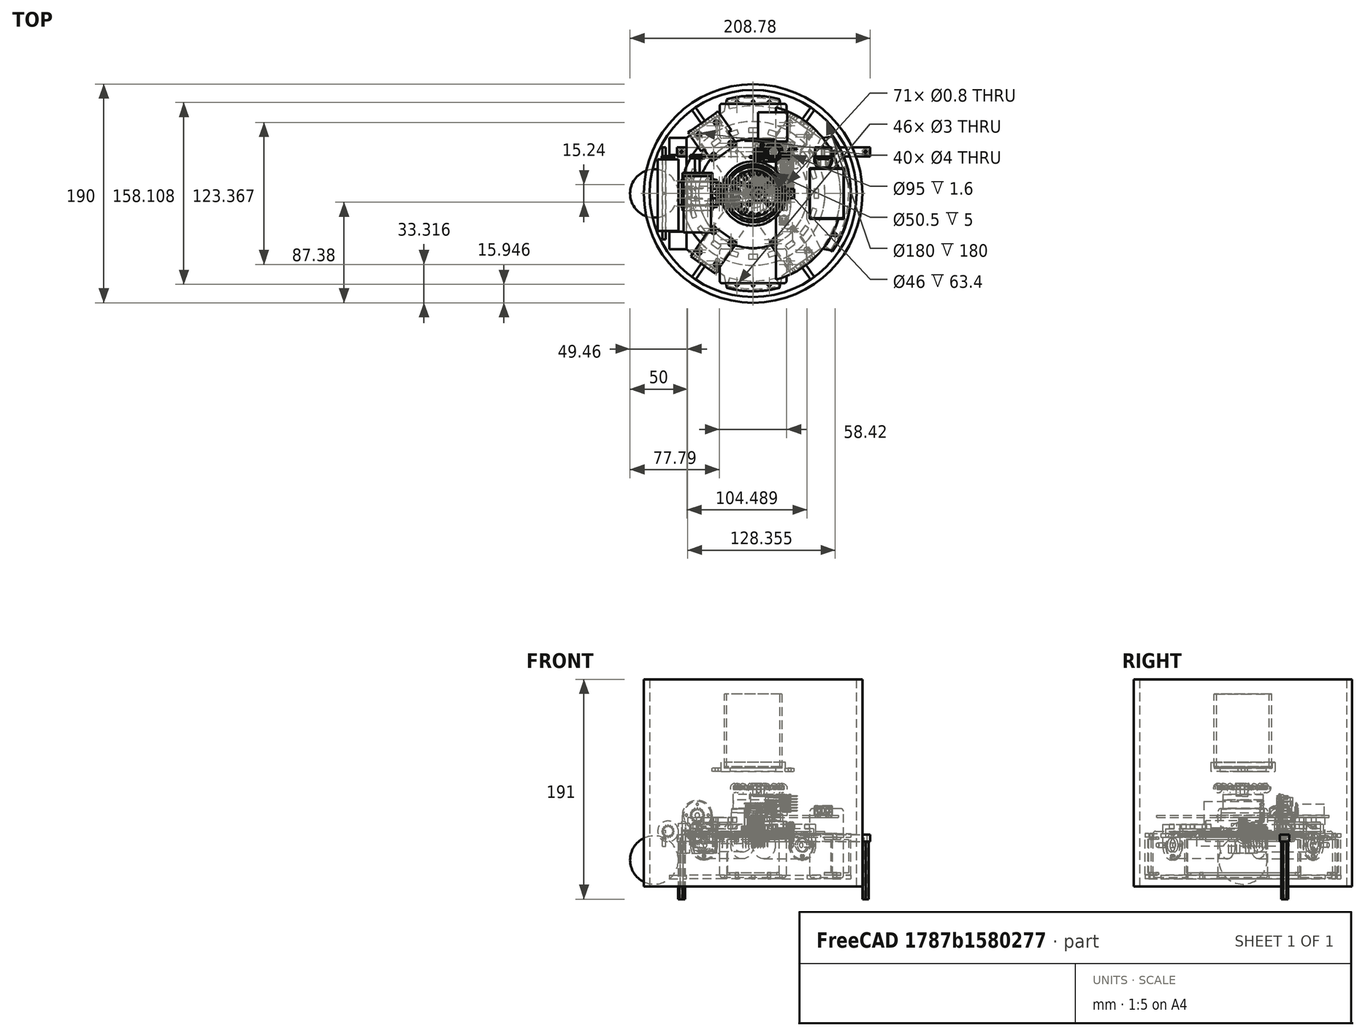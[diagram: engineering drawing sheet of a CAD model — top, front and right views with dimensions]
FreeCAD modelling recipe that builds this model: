
FCSTD DOCUMENT  (FreeCAD 0.21R33668 +7 (Git))
Label: SN8 model 3
License: All rights reserved
LicenseURL: https://en.wikipedia.org/wiki/All_rights_reserved
objects: Part::Feature×480, Sketcher::SketchObject×82, App::Part×79, PartDesign::Pad×55, PartDesign::Pocket×47, PartDesign::Body×37, PartDesign::SubShapeBinder×25, PartDesign::PolarPattern×12, PartDesign::Revolution×4, PartDesign::Fillet×3, Part::Part2DObjectPython×2, Part::Sphere×1
note: 857 computed .brp shape members not serialized (recipe doc carries the construction recipe); baked Part::Feature solids carry a one-line shape summary decoded from their .brp

FEATURE [Part::Feature] Part__Feature  label="base_® 㬮«砭¨"
  shape: bbox 35.56 x 44.45 x 1.6 mm, 428 faces (baked)
FEATURE [Part::Feature] Part__Feature022  label="960240-6202-AR Body8"
  Placement = pos=(10.16,-1.27,8.5) rot=(0,0,1;0rad)
  shape: bbox 20.32 x 2.54 x 8.5 mm, 114 faces (baked)
FEATURE [Part::Feature] Part__Feature023  label="960240-6202-AR Pin Long"
  Placement = pos=(8.89,0.039993,-0.757199) rot=(1,0,0;1.5708rad)
  shape: bbox 2 x 0.4 x 16.99 mm, 25 faces (baked)
FEATURE [Part::Feature] Part__Feature024  label="960240-6202-AR Pin Long001"
  Placement = pos=(6.35,0.039993,-0.757199) rot=(1,0,0;1.5708rad)
  shape: bbox 2 x 0.4 x 16.99 mm, 25 faces (baked)
FEATURE [Part::Feature] Part__Feature025  label="960240-6202-AR Pin Long002"
  Placement = pos=(3.81,0.039993,-0.757199) rot=(1,0,0;1.5708rad)
  shape: bbox 2 x 0.4 x 16.99 mm, 25 faces (baked)
FEATURE [Part::Feature] Part__Feature026  label="960240-6202-AR Pin Long003"
  Placement = pos=(1.27,0.039993,-0.757199) rot=(1,0,0;1.5708rad)
  shape: bbox 2 x 0.4 x 16.99 mm, 25 faces (baked)
FEATURE [Part::Feature] Part__Feature027  label="960240-6202-AR Pin Long004"
  Placement = pos=(-1.27,0.039993,-0.757199) rot=(1,0,0;1.5708rad)
  shape: bbox 2 x 0.4 x 16.99 mm, 25 faces (baked)
FEATURE [Part::Feature] Part__Feature028  label="960240-6202-AR Pin Long005"
  Placement = pos=(-3.81,0.039993,-0.757199) rot=(1,0,0;1.5708rad)
  shape: bbox 2 x 0.4 x 16.99 mm, 25 faces (baked)
FEATURE [Part::Feature] Part__Feature029  label="960240-6202-AR Pin Long006"
  Placement = pos=(-6.35,0.039993,-0.757199) rot=(1,0,0;1.5708rad)
  shape: bbox 2 x 0.4 x 16.99 mm, 25 faces (baked)
FEATURE [Part::Feature] Part__Feature030  label="960240-6202-AR Pin Long007"
  Placement = pos=(-8.89,0.039993,-0.757199) rot=(1,0,0;1.5708rad)
  shape: bbox 2 x 0.4 x 16.99 mm, 25 faces (baked)
FEATURE [App::Part] _60240_6202_AR_1x8_long  label="Right side I/O pins long"
  Group = -> [Part__Feature022,Part__Feature023,Part__Feature024,Part__Feature025,Part__Feature026,Part__Feature027,Part__Feature028,Part__Feature029,Part__Feature030]
  Origin = -> Origin
  Placement = pos=(33.909,10.414,1.6) rot=(0,0,1;1.5708rad)
FEATURE [Part::Feature] Part__Feature031  label="960240-6202-AR Body009"
  Placement = pos=(10.16,-1.27,8.5) rot=(0,0,1;0rad)
  shape: bbox 20.32 x 2.54 x 8.5 mm, 114 faces (baked)
FEATURE [Part::Feature] Part__Feature032  label="960240-6202-AR Pin Long008"
  Placement = pos=(8.89,0.039993,-0.757199) rot=(1,0,0;1.5708rad)
  shape: bbox 2 x 0.4 x 16.99 mm, 25 faces (baked)
FEATURE [Part::Feature] Part__Feature033  label="960240-6202-AR Pin Long009"
  Placement = pos=(6.35,0.039993,-0.757199) rot=(1,0,0;1.5708rad)
  shape: bbox 2 x 0.4 x 16.99 mm, 25 faces (baked)
FEATURE [Part::Feature] Part__Feature034  label="960240-6202-AR Pin Long010"
  Placement = pos=(3.81,0.039993,-0.757199) rot=(1,0,0;1.5708rad)
  shape: bbox 2 x 0.4 x 16.99 mm, 25 faces (baked)
FEATURE [Part::Feature] Part__Feature035  label="960240-6202-AR Pin Long011"
  Placement = pos=(1.27,0.039993,-0.757199) rot=(1,0,0;1.5708rad)
  shape: bbox 2 x 0.4 x 16.99 mm, 25 faces (baked)
FEATURE [Part::Feature] Part__Feature036  label="960240-6202-AR Pin Long012"
  Placement = pos=(-1.27,0.039993,-0.757199) rot=(1,0,0;1.5708rad)
  shape: bbox 2 x 0.4 x 16.99 mm, 25 faces (baked)
FEATURE [Part::Feature] Part__Feature037  label="960240-6202-AR Pin Long013"
  Placement = pos=(-3.81,0.039993,-0.757199) rot=(1,0,0;1.5708rad)
  shape: bbox 2 x 0.4 x 16.99 mm, 25 faces (baked)
FEATURE [Part::Feature] Part__Feature038  label="960240-6202-AR Pin Long014"
  Placement = pos=(-6.35,0.039993,-0.757199) rot=(1,0,0;1.5708rad)
  shape: bbox 2 x 0.4 x 16.99 mm, 25 faces (baked)
FEATURE [Part::Feature] Part__Feature039  label="960240-6202-AR Pin Long015"
  Placement = pos=(-8.89,0.039993,-0.757199) rot=(1,0,0;1.5708rad)
  shape: bbox 2 x 0.4 x 16.99 mm, 25 faces (baked)
FEATURE [App::Part] _60240_6202_AR_1x8_long001  label="Left side I/O pins"
  Group = -> [Part__Feature031,Part__Feature032,Part__Feature033,Part__Feature034,Part__Feature035,Part__Feature036,Part__Feature037,Part__Feature038,Part__Feature039]
  Origin = -> Origin001
  Placement = pos=(1.651,10.414,1.6) rot=(0,0,1;1.5708rad)
FEATURE [Part::Feature] Part__Feature040  label="960240-6202-AR Body6"
  Placement = pos=(7.62,-1.27,8.5) rot=(0,0,1;0rad)
  shape: bbox 15.24 x 2.54 x 8.5 mm, 88 faces (baked)
FEATURE [Part::Feature] Part__Feature041  label="960240-6202-AR Pin Long016"
  Placement = pos=(6.35,0.039993,-0.757199) rot=(1,0,0;1.5708rad)
  shape: bbox 2 x 0.4 x 16.99 mm, 25 faces (baked)
FEATURE [Part::Feature] Part__Feature042  label="960240-6202-AR Pin Long017"
  Placement = pos=(3.81,0.039993,-0.757199) rot=(1,0,0;1.5708rad)
  shape: bbox 2 x 0.4 x 16.99 mm, 25 faces (baked)
FEATURE [Part::Feature] Part__Feature043  label="960240-6202-AR Pin Long018"
  Placement = pos=(1.27,0.039993,-0.757199) rot=(1,0,0;1.5708rad)
  shape: bbox 2 x 0.4 x 16.99 mm, 25 faces (baked)
FEATURE [Part::Feature] Part__Feature044  label="960240-6202-AR Pin Long019"
  Placement = pos=(-1.27,0.039993,-0.757199) rot=(1,0,0;1.5708rad)
  shape: bbox 2 x 0.4 x 16.99 mm, 25 faces (baked)
FEATURE [Part::Feature] Part__Feature045  label="960240-6202-AR Pin Long020"
  Placement = pos=(-3.81,0.039993,-0.757199) rot=(1,0,0;1.5708rad)
  shape: bbox 2 x 0.4 x 16.99 mm, 25 faces (baked)
FEATURE [Part::Feature] Part__Feature046  label="960240-6202-AR Pin Long021"
  Placement = pos=(-6.35,0.039993,-0.757199) rot=(1,0,0;1.5708rad)
  shape: bbox 2 x 0.4 x 16.99 mm, 25 faces (baked)
FEATURE [App::Part] _60240_6202_AR_1x6_long  label="Right side I/O pins short"
  Group = -> [Part__Feature040,Part__Feature041,Part__Feature042,Part__Feature043,Part__Feature044,Part__Feature045,Part__Feature046]
  Origin = -> Origin002
  Placement = pos=(30.099,12.954,1.6) rot=(0,0,-1;1.5708rad)
FEATURE [Part::Feature] Part__Feature050  label="LED SMD RGB"
  Placement = pos=(3.559,28.499,1.75) rot=(0.57735,0.57735,0.57735;2.0944rad)
  shape: bbox 2.8 x 3.5 x 1.9 mm, 85 faces (baked)
FEATURE [Part::Feature] Part__Feature051  label="LED 1206 IR"
  Placement = pos=(28.321,41.91,1.6) rot=(0,0.707107,0.707107;3.14159rad)
  shape: bbox 1.6 x 3.2 x 1.095 mm, 42 faces, 2 solids (baked)
FEATURE [Part::Feature] Part__Feature052  label="LED 1206 IR001"
  Placement = pos=(7.239,41.91,1.6) rot=(1,0,0;1.5708rad)
  shape: bbox 1.6 x 3.2 x 1.095 mm, 42 faces, 2 solids (baked)
FEATURE [Part::Feature] Part__Feature053  label="SOT 23"
  Placement = pos=(3.429,25.019,2.15) rot=(0,0.707107,0.707107;3.14159rad)
  shape: bbox 3 x 2.5 x 1.1 mm, 49 faces (baked)
FEATURE [Part::Feature] Part__Feature054  label="SOT 024"
  Placement = pos=(20.193,4.064,2.15) rot=(0,0.707107,0.707107;3.14159rad)
  shape: bbox 3 x 2.5 x 1.1 mm, 49 faces (baked)
FEATURE [Part::Feature] Part__Feature062  label="EXBV8V"
  Placement = pos=(6.4748,30.1505,1.59) rot=(0,0,1;1.5708rad)
  shape: bbox 1.6 x 3.2 x 0.52 mm, 170 faces (baked)
FEATURE [Part::Feature] Part__Feature063  label="EXBV8V001"
  Placement = pos=(28.448,31.496,1.6) rot=(0,0,1;0rad)
  shape: bbox 3.2 x 1.6 x 0.52 mm, 170 faces (baked)
FEATURE [Part::Feature] Part__Feature064  label="EXBV8V002"
  Placement = pos=(28.448,25.019,1.6) rot=(0,0,1;0rad)
  shape: bbox 3.2 x 1.6 x 0.52 mm, 170 faces (baked)
FEATURE [Part::Feature] Part__Feature065  label="User Library-LQFP100-3_case"
  Placement = pos=(0,0.92,0) rot=(0,0,1;0rad)
  shape: bbox 13.97 x 1.4 x 13.97 mm, 31 faces (baked)
FEATURE [App::Part] User_Library_LQFP100_3  label="Microprocessor"
  Group = -> [Part__Feature065]
  Origin = -> Origin003
  Placement = pos=(17.78,16.383,1.6) rot=(1,0,0;1.5708rad)
FEATURE [Part::Feature] Part__Feature167  label="SOT 23-5"
  Placement = pos=(26.67,36.83,2.15) rot=(0.57735,-0.57735,-0.57735;2.0944rad)
  shape: bbox 2.5 x 3 x 1.1 mm, 75 faces (baked)
FEATURE [Part::Feature] Part__Feature168  label="SOT 23-006"
  Placement = pos=(15.113,4.572,2.15) rot=(0,0.707107,0.707107;3.14159rad)
  shape: bbox 3 x 2.5 x 1.1 mm, 75 faces (baked)
FEATURE [Part::Feature] Part__Feature169  label="UJ2-MIBH2-4-SMT_01_Defaut"
  shape: bbox 5.297 x 7.502 x 3.412 mm, 268 faces (baked)
FEATURE [App::Part] UJ2_MIBH2_4_SMT_Defaut  label="USB port"
  Group = -> [Part__Feature169]
  Origin = -> Origin004
  Placement = pos=(30.42,-1.4925,3.54996) rot=(0,0,1;1.5708rad)
FEATURE [Part::Feature] Part__Feature171  label="1040310811_USD1040310811_® 㬮«砭¨쥀«?"
  Placement = pos=(27.5125,71.8621,-0.6) rot=(0.707107,-0.707107,0;3.14159rad)
  shape: bbox 11.43 x 11.98 x 1.48 mm, 410 faces (baked)
FEATURE [Part::Feature] Part__Feature172  label="DF12-36DS-0.5V_® 㬮«砭¨"
  Placement = pos=(15.63,42.14,1.6) rot=(0,0,1;3.14159rad)
  shape: bbox 12.11 x 4.614 x 3.314 mm, 836 faces (baked)
FEATURE [Part::Feature] Part__Feature173  label="S2B-PH-K-S(LF)(SN)_® 㬮«砭¨"
  Placement = pos=(7.112,7.7,1.6) rot=(1,0,0;1.5708rad)
  shape: bbox 5.9 x 7.6 x 8.183 mm, 100 faces, 3 solids (baked)
FEATURE [Part::Feature] Part__Feature174  label="Crystal-SM2520-4"
  Placement = pos=(5.969,16.764,1.6) rot=(0,0,1;0rad)
  shape: bbox 2.5 x 2 x 0.825 mm, 72 faces, 5 solids (baked)
FEATURE [Part::Feature] Part__Feature175  label="Standoff metal 5x2.5mm_® 㬮«砭¨"
  Placement = pos=(33.02,36.2,1.6) rot=(1,0,0;1.5708rad)
  shape: bbox 5 x 5 x 5 mm, 6 faces (baked)
FEATURE [Part::Feature] Part__Feature176  label="Standoff metal 5x2.5mm_® 㬮«砭¨001"
  Placement = pos=(2.54,36.2,6.6) rot=(-1,0,0;1.5708rad)
  shape: bbox 5 x 5 x 5 mm, 6 faces (baked)
FEATURE [App::Part] openmv4_h7_base________________  label="PCB "
  Group = -> [Part__Feature,_60240_6202_AR_1x8_long,_60240_6202_AR_1x8_long001,_60240_6202_AR_1x6_long,Part__Feature050,Part__Feature051,Part__Feature052,Part__Feature053,Part__Feature054,Part__Feature062,Part__Feature063,Part__Feature064,User_Library_LQFP100_3,Part__Feature167,Part__Feature168,UJ2_MIBH2_4_SMT_Defaut,Part__Feature171,Part__Feature172,Part__Feature173,Part__Feature174,Part__Feature175,+1 more]
  Origin = -> Origin005
FEATURE [Part::Feature] Part__Feature177  label="ov7725_® 㬮«砭¨"
  shape: bbox 35.56 x 16.51 x 1.6 mm, 134 faces (baked)
FEATURE [Part::Feature] Part__Feature178  label="mount_lens"
  Placement = pos=(8.255,8.255,1.6) rot=(0,0,1;0rad)
  shape: bbox 23.8 x 17 x 14.3 mm, 58 faces (baked)
FEATURE [Part::Feature] Part__Feature179  label="DF1236"
  Placement = pos=(37.855,-65.4,0) rot=(0,1,0;3.14159rad)
  shape: bbox 12.1 x 4.6 x 4.9 mm, 1562 faces (baked)
FEATURE [App::Part] openmv4_ov7725________________  label="Lens mount"
  Group = -> [Part__Feature177,Part__Feature178,Part__Feature179]
  Origin = -> Origin006
  Placement = pos=(9.525,27.945,6.6) rot=(0,0,1;0rad)
FEATURE [Part::Feature] Part__Feature181  label="pan head cross recess screw_iso_ISO 7045 - M2.5 x 5 - Z - 5N"
  Placement = pos=(33.02,36.2,12.1) rot=(0,1,0;1.5708rad)
  shape: bbox 5.412 x 5.412 x 7.1 mm, 43 faces (baked)
FEATURE [Part::Feature] Part__Feature182  label="pan head cross recess screw_iso_ISO 7045 - M2.5 x 5 - Z - 5N001"
  Placement = pos=(2.54,36.2,12.1) rot=(0,1,0;1.5708rad)
  shape: bbox 5.412 x 5.412 x 7.1 mm, 43 faces (baked)
FEATURE [Part::Feature] Part__Feature183  label="microsd card"
  Placement = pos=(48.2048,51.1529,-0.388376) rot=(-0.707107,0.707107,0;3.14159rad)
  shape: bbox 15 x 11.07 x 1 mm, 19 faces (baked)
FEATURE [Part::Feature] Part__Feature184  label="LENS_Standard_® 㬮«砭¨"
  Placement = pos=(17.78,36.2,16.7534) rot=(1,0,0;1.5708rad)
  shape: bbox 14 x 14 x 16.7 mm, 16 faces (baked)
FEATURE [Part::Feature] Part__Feature186  label="Micro USB connector"
  Placement = pos=(26.6352,-11.6075,-1.10004) rot=(0.57735,0.57735,0.57735;4.18879rad)
  shape: bbox 12.26 x 29.6 x 16 mm, 326 faces (baked)
FEATURE [Part::Feature] Part__Feature187  label="pan head cross recess screw_iso_ISO 7045 - M1 x 4 - Z - 4S"
  Placement = pos=(17.78,47.3586,20.3) rot=(0.004126,-0.004126,-0.999983;1.57081rad)
  shape: bbox 2.165 x 5 x 2.165 mm, 92 faces (baked)
FEATURE [App::Part] openmv4_h7  label="OpenMV H7"
  Group = -> [openmv4_h7_base________________,openmv4_ov7725________________,Part__Feature181,Part__Feature182,Part__Feature183,Part__Feature184,Part__Feature186,Part__Feature187]
  Origin = -> Origin007
  Placement = pos=(36.22,-17.79,57) rot=(0,0,1;1.5708rad)
FEATURE [Sketcher::SketchObject] Sketch
  FullyConstrained = true
  MapMode = 5
  Support = -> [XY_Plane008]
  sketch-geometry (1):
    g0: Circle CenterX=0 CenterY=0 CenterZ=0 NormalX=0 NormalY=0 NormalZ=1 AngleXU=0 Radius=85
  constraints (2):
    c: Coincident(g0,g-1)
    c: Diameter(g0) = 170
FEATURE [Sketcher::SketchObject] Sketch005
  FullyConstrained = true
  MapMode = 5
  Placement = pos=(0,0,0) rot=(1,0,0;1.5708rad)
  Support = -> [XZ_Plane009]
  sketch-geometry (6):
    g0: ArcOfHyperbola CenterX=0 CenterY=94.5 CenterZ=0 NormalX=0 NormalY=0 NormalZ=1 MajorRadius=17.5 MinorRadius=15.6742 AngleXU=1.5708 StartAngle=0 EndAngle=1.02375
    g1: LineSegment StartX=5e-16 StartY=112 StartZ=0 EndX=-5e-16 EndY=77 EndZ=0
    g2: LineSegment StartX=-15.6742 StartY=112 StartZ=0 EndX=15.6742 EndY=112 EndZ=0
    g3: GeomPoint X=2.6e-15 Y=117.993 Z=0
    g4: LineSegment StartX=-19 StartY=122 StartZ=0 EndX=0 EndY=122 EndZ=0
    g5: LineSegment StartX=0 StartY=112 StartZ=0 EndX=0 EndY=122 EndZ=0
  constraints (15):
    c: InternalAlignment(g1,g0)
    c: InternalAlignment(g2,g0)
    c: InternalAlignment(g3,g0)
    c: Horizontal(g2)
    c: PointOnObject(g0,g-2)
    c: PointOnObject(g0,g-2)
    c: DistanceY(g0,g0) = 10
    c: DistanceX(g0,g0) = 19
    c: DistanceY(g1,g0) = 35
    c: Coincident(g4,g0)
    c: Coincident(g5,g0)
    c: Coincident(g5,g4)
    c: Vertical(g5)
    c: Horizontal(g4)
    c: DistanceY(g-1,g0) = 112
FEATURE [PartDesign::Pad] Pad  label="Structural layer"
  Direction = (0,0,1)
  Length = 3
  Length2 = 10
  Profile = -> Sketch
  ReferenceAxis = -> Sketch [N_Axis]
  Type = 0
FEATURE [Sketcher::SketchObject] Sketch001
  ExternalGeometry = -> [Pad]
  FullyConstrained = false
  MapMode = 5
  Placement = pos=(0,0,3) rot=(0,0,1;0rad)
  Support = -> [Pad]
  sketch-geometry (7):
    g0: LineSegment StartX=-10.6686 StartY=100.741 StartZ=0 EndX=44.4806 EndY=91.0164 EndZ=0
    g1: LineSegment StartX=44.4806 StartY=91.0164 StartZ=0 EndX=41.5109 EndY=74.1744 EndZ=0
    g2: LineSegment StartX=32.942 StartY=68.1744 StartZ=0 EndX=-7.63834 EndY=75.3298 EndZ=0
    g3: LineSegment StartX=-13.6383 StartY=83.8987 StartZ=0 EndX=-10.6686 EndY=100.741 EndZ=0
    g4: LineSegment StartX=32.942 StartY=68.1744 StartZ=0 EndX=41.5109 EndY=74.1744 EndZ=0
    g5: LineSegment StartX=-13.6383 StartY=83.8987 StartZ=0 EndX=-7.63834 EndY=75.3298 EndZ=0
    g6: LineSegment StartX=-98.5042 StartY=90.5189 StartZ=0 EndX=89.0462 EndY=57.4487 EndZ=0
  constraints (18):
    c: Coincident(g0,g1)
    c: Coincident(g3,g0)
    c: Coincident(g4,g2)
    c: Coincident(g4,g1)
    c: Coincident(g5,g3)
    c: Coincident(g5,g2)
    c: Angle(g4,g2) = 2.35619
    c: Angle(g2,g5) = 2.35619
    c: DistanceX(g3,g2) = 6
    c: Angle(g6,g-1) = 0.174533
    c: Parallel(g2,g6)
    c: Parallel(g0,g2)
    c: Perpendicular(g6,g1)
    c: Equal(g1,g3)
    c: Parallel(g1,g3)
    c: PointOnObject(g3,g-3)
    c: PointOnObject(g1,g-3)
    c: Distance(g0) = 56
FEATURE [PartDesign::Pocket] Pocket
  BaseFeature = -> Pad
  Direction = (0,0,-1)
  Length = 5
  Length2 = 5
  Profile = -> Sketch001
  ReferenceAxis = -> Sketch001 [N_Axis]
  Type = 1
FEATURE [PartDesign::PolarPattern] PolarPattern
  Angle = 110
  Axis = -> Sketch001 [N_Axis]
  BaseFeature = -> Pocket
  Occurrences = 2
  Originals = -> [Pocket]
FEATURE [PartDesign::Revolution] Revolution
  Angle = 360
  Axis = (0,-2e-16,1)
  Base = (0,0,0)
  Placement = pos=(0,0,0) rot=(1,0,0;1.5708rad)
  Profile = -> Sketch005
  ReferenceAxis = -> Sketch005 [V_Axis]
FEATURE [Sketcher::SketchObject] Sketch015
  FullyConstrained = true
  MapMode = 5
  Placement = pos=(0,0,3) rot=(0,0,1;0rad)
  Support = -> [PolarPattern]
  sketch-geometry (4):
    g0: LineSegment StartX=-111 StartY=31 StartZ=0 EndX=-31 EndY=111 EndZ=0
    g1: LineSegment StartX=-31 StartY=111 StartZ=0 EndX=-1 EndY=81 EndZ=0
    g2: LineSegment StartX=-1 StartY=81 StartZ=0 EndX=-81 EndY=1 EndZ=0
    g3: LineSegment StartX=-81 StartY=1 StartZ=0 EndX=-111 EndY=31 EndZ=0
  constraints (12):
    c: Coincident(g0,g1)
    c: Coincident(g1,g2)
    c: Coincident(g2,g3)
    c: Coincident(g3,g0)
    c: Equal(g3,g1)
    c: Equal(g0,g2)
    c: Angle(g3,g0) = 1.5708
    c: DistanceX(g2,g-1) = 81
    c: DistanceY(g-1,g1) = 81
    c: DistanceX(g0,g1) = 30
    c: DistanceX(g2,g1) = 80
    c: Angle(g-1,g2) = 0.785398
FEATURE [PartDesign::Pocket] Pocket004
  BaseFeature = -> PolarPattern
  Direction = (0,0,-1)
  Length = 5
  Length2 = 5
  Profile = -> Sketch015
  ReferenceAxis = -> Sketch015 [N_Axis]
  Type = 1
FEATURE [Sketcher::SketchObject] Sketch016
  FullyConstrained = true
  MapMode = 5
  Placement = pos=(0,0,0) rot=(1,0,0;1.5708rad)
  Support = -> [XZ_Plane016]
  sketch-geometry (8):
    g0: LineSegment StartX=-88 StartY=-1 StartZ=0 EndX=-79 EndY=-1 EndZ=0
    g1: LineSegment StartX=-79 StartY=-34 StartZ=0 EndX=-88 EndY=-34 EndZ=0
    g2: LineSegment StartX=-88 StartY=-34 StartZ=0 EndX=-88 EndY=-1 EndZ=0
    g3: LineSegment StartX=-79 StartY=-1 StartZ=0 EndX=-79 EndY=-3 EndZ=0
    g4: LineSegment StartX=-79 StartY=-3 StartZ=0 EndX=-86 EndY=-3 EndZ=0
    g5: LineSegment StartX=-86 StartY=-3 StartZ=0 EndX=-86 EndY=-32 EndZ=0
    g6: LineSegment StartX=-86 StartY=-32 StartZ=0 EndX=-79 EndY=-32 EndZ=0
    g7: LineSegment StartX=-79 StartY=-32 StartZ=0 EndX=-79 EndY=-34 EndZ=0
  constraints (24):
    c: Coincident(g1,g2)
    c: Coincident(g2,g0)
    c: Horizontal(g0)
    c: Horizontal(g1)
    c: Vertical(g2)
    c: DistanceY(g1,g0) = 33
    c: DistanceX(g1,g1) = 9
    c: DistanceX(g0,g-1) = 88
    c: DistanceY(g1,g-1) = 34
    c: Equal(g1,g0)
    c: Coincident(g3,g0)
    c: Vertical(g3)
    c: Coincident(g4,g3)
    c: Horizontal(g4)
    c: Coincident(g5,g4)
    c: Vertical(g5)
    c: Coincident(g6,g5)
    c: Horizontal(g6)
    c: Coincident(g7,g6)
    c: Coincident(g7,g1)
    c: Vertical(g7)
    c: Equal(g3,g7)
    c: DistanceY(g3,g3) = 2
    c: DistanceX(g0,g4) = 2
FEATURE [PartDesign::Revolution] Revolution001
  Angle = 30
  Axis = (1e-16,1e-16,1)
  Base = (0,0,0)
  Midplane = true
  Placement = pos=(0,0,0) rot=(1,0,0;1.5708rad)
  Profile = -> Sketch016
  ReferenceAxis = -> Z_Axis016
  Reversed = true
FEATURE [Part::Feature] Part__Feature268  label="OmniBase_Predeterminado004"
  Placement = pos=(4.80373,-0.638646,40.5) rot=(0,0,1;0rad)
  shape: bbox 44 x 43.9 x 9 mm, 104 faces (baked)
FEATURE [Part::Feature] Part__Feature269  label="Roller_Predeterminado072"
  Placement = pos=(4.80373,20.3614,41.6192) rot=(0,0,1;0rad)
  shape: bbox 2.6 x 8.659 x 8.659 mm, 10 faces (baked)
FEATURE [Part::Feature] Part__Feature270  label="Roller_Predeterminado073"
  Placement = pos=(-2.3787,19.0949,41.6192) rot=(0,0,1;0.349066rad)
  shape: bbox 4.664 x 8.342 x 8.659 mm, 10 faces (baked)
FEATURE [Part::Feature] Part__Feature271  label="Roller_Predeterminado074"
  Placement = pos=(-8.69481,15.4483,41.6192) rot=(0,0,1;0.698132rad)
  shape: bbox 6.71 x 7.451 x 8.659 mm, 10 faces (baked)
FEATURE [Part::Feature] Part__Feature272  label="Roller_Predeterminado075"
  Placement = pos=(-13.3828,9.86135,41.6192) rot=(0,0,1;1.0472rad)
  shape: bbox 7.965 x 5.765 x 8.659 mm, 10 faces (baked)
FEATURE [Part::Feature] Part__Feature273  label="Roller_Predeterminado076"
  Placement = pos=(-15.8772,3.00797,41.6192) rot=(0,0,1;1.39626rad)
  shape: bbox 8.632 x 3.688 x 8.659 mm, 10 faces (baked)
FEATURE [Part::Feature] Part__Feature274  label="Roller_Predeterminado077"
  Placement = pos=(-15.8772,-4.28526,41.6192) rot=(0,0,1;1.74533rad)
  shape: bbox 8.632 x 3.688 x 8.659 mm, 10 faces (baked)
FEATURE [Part::Feature] Part__Feature275  label="Roller_Predeterminado078"
  Placement = pos=(-13.3828,-11.1386,41.6192) rot=(0,0,1;2.0944rad)
  shape: bbox 7.965 x 5.765 x 8.659 mm, 10 faces (baked)
FEATURE [Part::Feature] Part__Feature276  label="Roller_Predeterminado079"
  Placement = pos=(-8.69481,-16.7256,41.6192) rot=(0,0,1;2.44346rad)
  shape: bbox 6.71 x 7.451 x 8.659 mm, 10 faces (baked)
FEATURE [Part::Feature] Part__Feature277  label="Roller_Predeterminado080"
  Placement = pos=(-2.3787,-20.3722,41.6192) rot=(0,0,1;2.79253rad)
  shape: bbox 4.664 x 8.342 x 8.659 mm, 10 faces (baked)
FEATURE [Part::Feature] Part__Feature278  label="Roller_Predeterminado081"
  Placement = pos=(4.80373,-21.6386,41.6192) rot=(0,0,1;3.14159rad)
  shape: bbox 2.6 x 8.659 x 8.659 mm, 10 faces (baked)
FEATURE [Part::Feature] Part__Feature279  label="Roller_Predeterminado082"
  Placement = pos=(11.9862,-20.3722,41.6192) rot=(0,0,1;3.49066rad)
  shape: bbox 4.664 x 8.342 x 8.659 mm, 10 faces (baked)
FEATURE [Part::Feature] Part__Feature280  label="Roller_Predeterminado083"
  Placement = pos=(18.3023,-16.7256,41.6192) rot=(0,0,1;3.83972rad)
  shape: bbox 6.71 x 7.451 x 8.659 mm, 10 faces (baked)
FEATURE [Part::Feature] Part__Feature281  label="Roller_Predeterminado084"
  Placement = pos=(22.9903,-11.1386,41.6192) rot=(0,0,-1;2.0944rad)
  shape: bbox 7.965 x 5.765 x 8.659 mm, 10 faces (baked)
FEATURE [Part::Feature] Part__Feature282  label="Roller_Predeterminado085"
  Placement = pos=(25.4847,-4.28526,41.6192) rot=(0,0,-1;1.74533rad)
  shape: bbox 8.632 x 3.688 x 8.659 mm, 10 faces (baked)
FEATURE [Part::Feature] Part__Feature283  label="Roller_Predeterminado086"
  Placement = pos=(25.4847,3.00797,41.6192) rot=(0,0,-1;1.39626rad)
  shape: bbox 8.632 x 3.688 x 8.659 mm, 10 faces (baked)
FEATURE [Part::Feature] Part__Feature284  label="Roller_Predeterminado087"
  Placement = pos=(22.9903,9.86135,41.6192) rot=(0,0,-1;1.0472rad)
  shape: bbox 7.965 x 5.765 x 8.659 mm, 10 faces (baked)
FEATURE [Part::Feature] Part__Feature285  label="Roller_Predeterminado088"
  Placement = pos=(18.3023,15.4483,41.6192) rot=(0,0,-1;0.698132rad)
  shape: bbox 6.71 x 7.451 x 8.659 mm, 10 faces (baked)
FEATURE [Part::Feature] Part__Feature286  label="Roller_Predeterminado089"
  Placement = pos=(11.9862,19.0949,41.6192) rot=(0,0,-1;0.349066rad)
  shape: bbox 4.664 x 8.342 x 8.659 mm, 10 faces (baked)
FEATURE [Part::Feature] Part__Feature287  label="Nut_Predeterminado004"
  Placement = pos=(4.80373,-0.638646,43.5) rot=(0,0,1;1.0472rad)
  shape: bbox 13.86 x 12.93 x 2 mm, 24 faces (baked)
FEATURE [App::Part] OmniWheel054  label="OmniWheel 1"
  Group = -> [Part__Feature268,Part__Feature269,Part__Feature270,Part__Feature271,Part__Feature272,Part__Feature273,Part__Feature274,Part__Feature275,Part__Feature276,Part__Feature277,Part__Feature278,Part__Feature279,Part__Feature280,Part__Feature281,Part__Feature282,Part__Feature283,Part__Feature284,Part__Feature285,Part__Feature286,Part__Feature287]
  Origin = -> Origin019
  Placement = pos=(-23.8855,35.1581,-6.8) rot=(-0.419215,-0.805305,-0.419215;1.78566rad)
FEATURE [Sketcher::SketchObject] Sketch023
  FullyConstrained = true
  MapMode = 5
  Support = -> [XY_Plane024]
  sketch-geometry (9):
    g0: Circle CenterX=0 CenterY=0 CenterZ=0 NormalX=0 NormalY=0 NormalZ=1 AngleXU=0 Radius=20
    g1: LineSegment StartX=27.7128 StartY=-4 StartZ=0 EndX=35.7128 EndY=-4 EndZ=0
    g2: LineSegment StartX=35.7128 StartY=-4 StartZ=0 EndX=35.7128 EndY=4 EndZ=0
    g3: LineSegment StartX=35.7128 StartY=4 StartZ=0 EndX=27.7128 EndY=4 EndZ=0
    g4: LineSegment StartX=-27.7128 StartY=-4 StartZ=0 EndX=-35.7128 EndY=-4 EndZ=0
    g5: LineSegment StartX=-35.7128 StartY=-4 StartZ=0 EndX=-35.7128 EndY=4 EndZ=0
    g6: LineSegment StartX=-35.7128 StartY=4 StartZ=0 EndX=-27.7128 EndY=4 EndZ=0
    g7: ArcOfCircle CenterX=0 CenterY=0 CenterZ=0 NormalX=0 NormalY=0 NormalZ=1 AngleXU=0 Radius=28 StartAngle=0.143348 EndAngle=2.99825
    g8: ArcOfCircle CenterX=0 CenterY=0 CenterZ=0 NormalX=0 NormalY=0 NormalZ=1 AngleXU=0 Radius=28 StartAngle=3.28494 EndAngle=6.13984
  constraints (25):
    c: Coincident(g0,g-1)
    c: Diameter(g0) = 40
    c: Horizontal(g1)
    c: Coincident(g2,g1)
    c: Coincident(g3,g2)
    c: Horizontal(g3)
    c: Horizontal(g4)
    c: Coincident(g5,g4)
    c: Vertical(g5)
    c: Coincident(g6,g5)
    c: Horizontal(g6)
    c: Coincident(g7,g0)
    c: Coincident(g7,g6)
    c: Coincident(g7,g3)
    c: Coincident(g8,g0)
    c: Coincident(g8,g4)
    c: Coincident(g8,g1)
    c: Diameter(g7) = 56
    c: Diameter(g8) = 56
    c: Symmetric(g1,g2,g-1)
    c: Equal(g5,g2)
    c: Equal(g6,g3)
    c: Equal(g4,g1)
    c: DistanceY(g2,g2) = 8
    c: DistanceX(g6,g6) = 8
FEATURE [PartDesign::Pad] Pad007
  Direction = (0,0,1)
  Length = 3
  Length2 = 10
  Profile = -> Sketch023
  ReferenceAxis = -> Sketch023 [N_Axis]
  Type = 0
FEATURE [Sketcher::SketchObject] Sketch025
  FullyConstrained = true
  MapMode = 5
  Support = -> [XY_Plane026]
  sketch-geometry (2):
    g0: Circle CenterX=0 CenterY=0 CenterZ=0 NormalX=0 NormalY=0 NormalZ=1 AngleXU=0 Radius=90
    g1: Circle CenterX=0 CenterY=0 CenterZ=0 NormalX=0 NormalY=0 NormalZ=1 AngleXU=0 Radius=95
  constraints (4):
    c: Diameter(g0) = 180
    c: Coincident(g1,g-1)
    c: Diameter(g1) = 190
    c: Coincident(g0,g-1)
FEATURE [PartDesign::Pad] Pad008
  Direction = (0,0,1)
  Length = 180
  Length2 = 10
  Profile = -> Sketch025
  ReferenceAxis = -> Sketch025 [N_Axis]
  Type = 0
FEATURE [PartDesign::Body] Body008  label="Cylinder"
  Group = -> [Sketch025,Pad008]
  Origin = -> Origin026
  Placement = pos=(0,0,-44) rot=(0,0,1;0rad)
  Tip = -> Pad008
FEATURE [Sketcher::SketchObject] Sketch030
  FullyConstrained = true
  MapMode = 5
  Support = -> [XY_Plane032]
  sketch-geometry (4):
    g0: LineSegment StartX=-29 StartY=-50 StartZ=0 EndX=29 EndY=-50 EndZ=0
    g1: LineSegment StartX=29 StartY=-50 StartZ=0 EndX=29 EndY=-80 EndZ=0
    g2: LineSegment StartX=29 StartY=-80 StartZ=0 EndX=-29 EndY=-80 EndZ=0
    g3: LineSegment StartX=-29 StartY=-80 StartZ=0 EndX=-29 EndY=-50 EndZ=0
  constraints (11):
    c: Coincident(g0,g1)
    c: Coincident(g1,g2)
    c: Coincident(g2,g3)
    c: Coincident(g3,g0)
    c: Horizontal(g0)
    c: Vertical(g1)
    c: Vertical(g3)
    c: DistanceX(g0,g0) = 58
    c: DistanceY(g1,g1) = 30
    c: Symmetric(g2,g1,g-2)
    c: DistanceY(g0,g-1) = 50
FEATURE [PartDesign::Pad] Pad013
  Direction = (0,0,1)
  Length = 40
  Length2 = 10
  Profile = -> Sketch030
  ReferenceAxis = -> Sketch030 [N_Axis]
  Type = 0
FEATURE [PartDesign::Fillet] Fillet001
  Base = -> Pad013 [Edge4,Edge12,Edge10,Edge7,Edge2,Edge3,Edge1,Edge11,Edge8,Edge5,Edge6,Edge9]
  BaseFeature = -> Pad013
  Radius = 2
  SupportTransform = false
  UseAllEdges = false
FEATURE [PartDesign::Body] Body013  label="Battery 1"
  Group = -> [Sketch030,Pad013,Fillet001]
  Origin = -> Origin032
  Placement = pos=(0,2,-36) rot=(0,0,1;0rad)
  Tip = -> Fillet001
FEATURE [Sketcher::SketchObject] Sketch031
  FullyConstrained = true
  MapMode = 5
  Support = -> [XY_Plane033]
  sketch-geometry (4):
    g0: LineSegment StartX=-29 StartY=80 StartZ=0 EndX=29 EndY=80 EndZ=0
    g1: LineSegment StartX=29 StartY=80 StartZ=0 EndX=29 EndY=50 EndZ=0
    g2: LineSegment StartX=29 StartY=50 StartZ=0 EndX=-29 EndY=50 EndZ=0
    g3: LineSegment StartX=-29 StartY=50 StartZ=0 EndX=-29 EndY=80 EndZ=0
  constraints (11):
    c: Coincident(g0,g1)
    c: Coincident(g1,g2)
    c: Coincident(g2,g3)
    c: Coincident(g3,g0)
    c: Horizontal(g0)
    c: Vertical(g1)
    c: Vertical(g3)
    c: DistanceX(g0,g0) = 58
    c: DistanceY(g1,g1) = 30
    c: Symmetric(g2,g1,g-2)
    c: DistanceY(g-1,g1) = 50
FEATURE [PartDesign::Pad] Pad014
  Direction = (0,0,1)
  Length = 40
  Length2 = 10
  Profile = -> Sketch031
  ReferenceAxis = -> Sketch031 [N_Axis]
  Type = 0
FEATURE [PartDesign::Fillet] Fillet002
  Base = -> Pad014 [Edge4,Edge12,Edge10,Edge7,Edge2,Edge3,Edge1,Edge11,Edge8,Edge5,Edge6,Edge9]
  BaseFeature = -> Pad014
  Radius = 2
  SupportTransform = false
  UseAllEdges = false
FEATURE [PartDesign::Body] Body014  label="Battery 2"
  Group = -> [Sketch031,Pad014,Fillet002]
  Origin = -> Origin033
  Placement = pos=(0,-2,-36) rot=(0,0,1;0rad)
  Tip = -> Fillet002
FEATURE [Sketcher::SketchObject] Sketch061
  FullyConstrained = true
  MapMode = 5
  Placement = pos=(0,0,2) rot=(0,0,1;0rad)
  sketch-geometry (1):
    g0: Circle CenterX=0 CenterY=0 CenterZ=0 NormalX=0 NormalY=0 NormalZ=1 AngleXU=0 Radius=12.5
  constraints (2):
    c: Coincident(g0,g-1)
    c: Diameter(g0) = 25
FEATURE [PartDesign::Pocket] Pocket019
  BaseFeature = -> Pocket004
  Direction = (0,0,-1)
  Length = 5
  Length2 = 5
  Profile = -> Sketch061
  ReferenceAxis = -> Sketch061 [N_Axis]
  Type = 4
FEATURE [Part::Feature] Part__Feature439  label="114-00841-68--3DModel-STEP-56544 v1"
  Placement = pos=(24.0935,-0.00012972,0.814608) rot=(0.57735,0.57735,0.57735;2.0944rad)
  shape: bbox 11.35 x 11.95 x 1.68 mm, 239 faces (baked)
FEATURE [Part::Feature] Part__Feature440  label="114-00841-68--3DModel-STEP-56544 v002"
  Placement = pos=(24.0935,-0.00012972,0.814608) rot=(0.57735,0.57735,0.57735;2.0944rad)
  shape: bbox 0.7165 x 3.441 x 0.555 mm, 26 faces (baked)
FEATURE [Part::Feature] Part__Feature441  label="114-00841-68--3DModel-STEP-56544 v003"
  Placement = pos=(24.0935,-0.00012972,0.814608) rot=(0.57735,0.57735,0.57735;2.0944rad)
  shape: bbox 1.24 x 4.945 x 0.625 mm, 28 faces (baked)
FEATURE [Part::Feature] Part__Feature442  label="114-00841-68--3DModel-STEP-56544 v004"
  Placement = pos=(24.0935,-0.00012972,0.814608) rot=(0.57735,0.57735,0.57735;2.0944rad)
  shape: bbox 10 x 11.95 x 1.48 mm, 267 faces (baked)
FEATURE [Part::Feature] Part__Feature443  label="114-00841-68--3DModel-STEP-56544 v005"
  Placement = pos=(24.0935,-0.00012972,0.814608) rot=(0.57735,0.57735,0.57735;2.0944rad)
  shape: bbox 1.25 x 0.5 x 0.6 mm, 14 faces (baked)
FEATURE [Part::Feature] Part__Feature444  label="114-00841-68--3DModel-STEP-56544 v006"
  Placement = pos=(24.0935,-0.00012972,0.814608) rot=(0.57735,0.57735,0.57735;2.0944rad)
  shape: bbox 0.5 x 0.55 x 0.6 mm, 14 faces (baked)
FEATURE [Part::Feature] Part__Feature445  label="114-00841-68--3DModel-STEP-56544 v007"
  Placement = pos=(24.0935,-0.00012972,0.814608) rot=(0.57735,0.57735,0.57735;2.0944rad)
  shape: bbox 8.245 x 0.8521 x 1.179 mm, 52 faces (baked)
FEATURE [Part::Feature] Part__Feature446  label="114-00841-68--3DModel-STEP-56544 v008"
  Placement = pos=(24.0935,-0.00012972,0.814608) rot=(0.57735,0.57735,0.57735;2.0944rad)
  shape: bbox 8.254 x 0.8613 x 1.188 mm, 52 faces (baked)
FEATURE [Part::Feature] Part__Feature447  label="114-00841-68--3DModel-STEP-56544 v009"
  Placement = pos=(24.0935,-0.00012972,0.814608) rot=(0.57735,0.57735,0.57735;2.0944rad)
  shape: bbox 8.245 x 0.8521 x 1.179 mm, 52 faces (baked)
FEATURE [Part::Feature] Part__Feature448  label="114-00841-68--3DModel-STEP-56544 v010"
  Placement = pos=(24.0935,-0.00012972,0.814608) rot=(0.57735,0.57735,0.57735;2.0944rad)
  shape: bbox 8.245 x 0.8521 x 1.179 mm, 52 faces (baked)
FEATURE [Part::Feature] Part__Feature449  label="114-00841-68--3DModel-STEP-56544 v011"
  Placement = pos=(24.0935,-0.00012972,0.814608) rot=(0.57735,0.57735,0.57735;2.0944rad)
  shape: bbox 8.245 x 0.8521 x 1.179 mm, 52 faces (baked)
FEATURE [Part::Feature] Part__Feature450  label="114-00841-68--3DModel-STEP-56544 v012"
  Placement = pos=(24.0935,-0.00012972,0.814608) rot=(0.57735,0.57735,0.57735;2.0944rad)
  shape: bbox 8.065 x 0.8522 x 1.179 mm, 52 faces (baked)
FEATURE [Part::Feature] Part__Feature451  label="114-00841-68--3DModel-STEP-56544 v013"
  Placement = pos=(24.0935,-0.00012972,0.814608) rot=(0.57735,0.57735,0.57735;2.0944rad)
  shape: bbox 8.065 x 0.8521 x 1.179 mm, 52 faces (baked)
FEATURE [Part::Feature] Part__Feature452  label="114-00841-68--3DModel-STEP-56544 v014"
  Placement = pos=(24.0935,-0.00012972,0.814608) rot=(0.57735,0.57735,0.57735;2.0944rad)
  shape: bbox 8.665 x 0.8521 x 1.179 mm, 52 faces (baked)
FEATURE [App::Part] _14_00841_68__3DModel_STEP_56544_v1  label="114-00841-68--3DModel-STEP-56544 v015"
  Group = -> [Part__Feature439,Part__Feature440,Part__Feature441,Part__Feature442,Part__Feature443,Part__Feature444,Part__Feature445,Part__Feature446,Part__Feature447,Part__Feature448,Part__Feature449,Part__Feature450,Part__Feature451,Part__Feature452]
  Origin = -> Origin052
FEATURE [Part::Feature] Part__Feature453  label="MIMXRT1052CVJ5B v1"
  Placement = pos=(1.30183,-0.0809243,0.815) rot=(0,0.707107,0.707107;3.14159rad)
  shape: bbox 12 x 12 x 1.27 mm, 6 faces (baked)
FEATURE [App::Part] MIMXRT1052CVJ5B_v1  label="MIMXRT1052CVJ5B v198"
  Group = -> [Part__Feature453]
  Origin = -> Origin053
FEATURE [Part::Feature] Part__Feature589  label="MicroUSB Molex 473460001 v1"
  Placement = pos=(-28.9499,0.13174,2.07033) rot=(0.57735,-0.57735,-0.57735;2.0944rad)
  shape: bbox 5.43 x 7.98 x 2.94 mm, 406 faces (baked)
FEATURE [Part::Feature] Part__Feature590  label="COMPOUND"
  shape: bbox 2.54 x 2.54 x 2.799 mm, 22 faces, 0 solids (baked)
FEATURE [Part::Feature] Part__Feature591  label="COMPOUND001"
  shape: bbox 2.54 x 2.54 x 2.799 mm, 22 faces, 0 solids (baked)
FEATURE [Part::Feature] Part__Feature592  label="COMPOUND002"
  shape: bbox 2.54 x 2.54 x 2.799 mm, 23 faces, 0 solids (baked)
FEATURE [Part::Feature] Part__Feature593  label="COMPOUND003"
  shape: bbox 2.54 x 2.54 x 2.799 mm, 22 faces, 0 solids (baked)
FEATURE [Part::Feature] Part__Feature594  label="COMPOUND004"
  shape: bbox 2.54 x 2.54 x 2.799 mm, 22 faces, 0 solids (baked)
FEATURE [Part::Feature] Part__Feature595  label="COMPOUND005"
  shape: bbox 2.54 x 2.54 x 2.799 mm, 23 faces, 0 solids (baked)
FEATURE [App::Part] COMPOUND  label="COMPOUND006"
  Group = -> [Part__Feature590,Part__Feature591,Part__Feature592,Part__Feature593,Part__Feature594,Part__Feature595]
  Origin = -> Origin055
FEATURE [Part::Feature] Part__Feature596  label="COMPOUND007"
  shape: bbox 0.6304 x 0.63 x 12.7 mm, 14 faces (baked)
FEATURE [Part::Feature] Part__Feature597  label="COMPOUND008"
  shape: bbox 0.6304 x 0.63 x 12.7 mm, 14 faces (baked)
FEATURE [Part::Feature] Part__Feature598  label="COMPOUND009"
  shape: bbox 0.6304 x 0.63 x 12.7 mm, 14 faces (baked)
FEATURE [Part::Feature] Part__Feature599  label="COMPOUND010"
  shape: bbox 0.6304 x 0.63 x 12.7 mm, 14 faces (baked)
FEATURE [Part::Feature] Part__Feature600  label="COMPOUND011"
  shape: bbox 0.6304 x 0.63 x 12.7 mm, 14 faces (baked)
FEATURE [Part::Feature] Part__Feature601  label="COMPOUND012"
  shape: bbox 0.6304 x 0.63 x 12.7 mm, 14 faces (baked)
FEATURE [App::Part] COMPOUND001  label="COMPOUND013"
  Group = -> [Part__Feature596,Part__Feature597,Part__Feature598,Part__Feature599,Part__Feature600,Part__Feature601]
  Origin = -> Origin056
FEATURE [App::Part] Pin_Header_1x6_TH_Pitch_2_54mm_v1  label="Pin Header 1x6 TH Pitch 2.54mm v1"
  Group = -> [COMPOUND,COMPOUND001]
  Origin = -> Origin054
  Placement = pos=(-16.51,-7.62,-0.814) rot=(0,1,0;3.14159rad)
FEATURE [Part::Feature] Part__Feature602  label="COMPOUND014"
  shape: bbox 2.54 x 2.54 x 2.799 mm, 22 faces, 0 solids (baked)
FEATURE [Part::Feature] Part__Feature603  label="COMPOUND015"
  shape: bbox 2.54 x 2.54 x 2.799 mm, 22 faces, 0 solids (baked)
FEATURE [Part::Feature] Part__Feature604  label="COMPOUND016"
  shape: bbox 2.54 x 2.54 x 2.799 mm, 23 faces, 0 solids (baked)
FEATURE [Part::Feature] Part__Feature605  label="COMPOUND017"
  shape: bbox 2.54 x 2.54 x 2.799 mm, 22 faces, 0 solids (baked)
FEATURE [Part::Feature] Part__Feature606  label="COMPOUND018"
  shape: bbox 2.54 x 2.54 x 2.799 mm, 22 faces, 0 solids (baked)
FEATURE [Part::Feature] Part__Feature607  label="COMPOUND019"
  shape: bbox 2.54 x 2.54 x 2.799 mm, 23 faces, 0 solids (baked)
FEATURE [App::Part] COMPOUND002  label="COMPOUND020"
  Group = -> [Part__Feature602,Part__Feature603,Part__Feature604,Part__Feature605,Part__Feature606,Part__Feature607]
  Origin = -> Origin058
FEATURE [Part::Feature] Part__Feature608  label="COMPOUND021"
  shape: bbox 0.6304 x 0.63 x 12.7 mm, 14 faces (baked)
FEATURE [Part::Feature] Part__Feature609  label="COMPOUND022"
  shape: bbox 0.6304 x 0.63 x 12.7 mm, 14 faces (baked)
FEATURE [Part::Feature] Part__Feature610  label="COMPOUND023"
  shape: bbox 0.6304 x 0.63 x 12.7 mm, 14 faces (baked)
FEATURE [Part::Feature] Part__Feature611  label="COMPOUND024"
  shape: bbox 0.6304 x 0.63 x 12.7 mm, 14 faces (baked)
FEATURE [Part::Feature] Part__Feature612  label="COMPOUND025"
  shape: bbox 0.6304 x 0.63 x 12.7 mm, 14 faces (baked)
FEATURE [Part::Feature] Part__Feature613  label="COMPOUND026"
  shape: bbox 0.6304 x 0.63 x 12.7 mm, 14 faces (baked)
FEATURE [App::Part] COMPOUND003  label="COMPOUND027"
  Group = -> [Part__Feature608,Part__Feature609,Part__Feature610,Part__Feature611,Part__Feature612,Part__Feature613]
  Origin = -> Origin059
FEATURE [App::Part] Pin_Header_1x6_TH_Pitch_2_54mm_v002  label="Pin Header 1x6 TH Pitch 2.54mm v002"
  Group = -> [COMPOUND002,COMPOUND003]
  Origin = -> Origin057
  Placement = pos=(-1.27,-7.62,-0.814) rot=(0,1,0;3.14159rad)
FEATURE [Part::Feature] Part__Feature614  label="COMPOUND028"
  shape: bbox 2.54 x 2.54 x 2.799 mm, 22 faces, 0 solids (baked)
FEATURE [Part::Feature] Part__Feature615  label="COMPOUND029"
  shape: bbox 2.54 x 2.54 x 2.799 mm, 22 faces, 0 solids (baked)
FEATURE [Part::Feature] Part__Feature616  label="COMPOUND030"
  shape: bbox 2.54 x 2.54 x 2.799 mm, 23 faces, 0 solids (baked)
FEATURE [Part::Feature] Part__Feature617  label="COMPOUND031"
  shape: bbox 2.54 x 2.54 x 2.799 mm, 22 faces, 0 solids (baked)
FEATURE [Part::Feature] Part__Feature618  label="COMPOUND032"
  shape: bbox 2.54 x 2.54 x 2.799 mm, 22 faces, 0 solids (baked)
FEATURE [Part::Feature] Part__Feature619  label="COMPOUND033"
  shape: bbox 2.54 x 2.54 x 2.799 mm, 23 faces, 0 solids (baked)
FEATURE [App::Part] COMPOUND004  label="COMPOUND034"
  Group = -> [Part__Feature614,Part__Feature615,Part__Feature616,Part__Feature617,Part__Feature618,Part__Feature619]
  Origin = -> Origin060
FEATURE [Part::Feature] Part__Feature620  label="COMPOUND035"
  shape: bbox 0.6304 x 0.63 x 12.7 mm, 14 faces (baked)
FEATURE [Part::Feature] Part__Feature621  label="COMPOUND036"
  shape: bbox 0.6304 x 0.63 x 12.7 mm, 14 faces (baked)
FEATURE [Part::Feature] Part__Feature622  label="COMPOUND037"
  shape: bbox 0.6304 x 0.63 x 12.7 mm, 14 faces (baked)
FEATURE [Part::Feature] Part__Feature623  label="COMPOUND038"
  shape: bbox 0.6304 x 0.63 x 12.7 mm, 14 faces (baked)
FEATURE [Part::Feature] Part__Feature624  label="COMPOUND039"
  shape: bbox 0.6304 x 0.63 x 12.7 mm, 14 faces (baked)
FEATURE [Part::Feature] Part__Feature625  label="COMPOUND040"
  shape: bbox 0.6304 x 0.63 x 12.7 mm, 14 faces (baked)
FEATURE [App::Part] COMPOUND005  label="COMPOUND041"
  Group = -> [Part__Feature620,Part__Feature621,Part__Feature622,Part__Feature623,Part__Feature624,Part__Feature625]
  Origin = -> Origin010
FEATURE [App::Part] Pin_Header_1x6_TH_Pitch_2_54mm_v003  label="Pin Header 1x6 TH Pitch 2.54mm v003"
  Group = -> [COMPOUND004,COMPOUND005]
  Origin = -> Origin011
  Placement = pos=(13.97,-7.62,-0.814) rot=(0,1,0;3.14159rad)
FEATURE [Part::Feature] Part__Feature626  label="COMPOUND042"
  shape: bbox 2.54 x 2.54 x 2.799 mm, 22 faces, 0 solids (baked)
FEATURE [Part::Feature] Part__Feature627  label="COMPOUND043"
  shape: bbox 2.54 x 2.54 x 2.799 mm, 22 faces, 0 solids (baked)
FEATURE [Part::Feature] Part__Feature628  label="COMPOUND044"
  shape: bbox 2.54 x 2.54 x 2.799 mm, 23 faces, 0 solids (baked)
FEATURE [Part::Feature] Part__Feature629  label="COMPOUND045"
  shape: bbox 2.54 x 2.54 x 2.799 mm, 22 faces, 0 solids (baked)
FEATURE [Part::Feature] Part__Feature630  label="COMPOUND046"
  shape: bbox 2.54 x 2.54 x 2.799 mm, 22 faces, 0 solids (baked)
FEATURE [Part::Feature] Part__Feature631  label="COMPOUND047"
  shape: bbox 2.54 x 2.54 x 2.799 mm, 23 faces, 0 solids (baked)
FEATURE [App::Part] COMPOUND006  label="COMPOUND048"
  Group = -> [Part__Feature626,Part__Feature627,Part__Feature628,Part__Feature629,Part__Feature630,Part__Feature631]
  Origin = -> Origin012
FEATURE [Part::Feature] Part__Feature632  label="COMPOUND049"
  shape: bbox 0.6304 x 0.63 x 12.7 mm, 14 faces (baked)
FEATURE [Part::Feature] Part__Feature633  label="COMPOUND050"
  shape: bbox 0.6304 x 0.63 x 12.7 mm, 14 faces (baked)
FEATURE [Part::Feature] Part__Feature634  label="COMPOUND051"
  shape: bbox 0.6304 x 0.63 x 12.7 mm, 14 faces (baked)
FEATURE [Part::Feature] Part__Feature635  label="COMPOUND052"
  shape: bbox 0.6304 x 0.63 x 12.7 mm, 14 faces (baked)
FEATURE [Part::Feature] Part__Feature636  label="COMPOUND053"
  shape: bbox 0.6304 x 0.63 x 12.7 mm, 14 faces (baked)
FEATURE [Part::Feature] Part__Feature637  label="COMPOUND054"
  shape: bbox 0.6304 x 0.63 x 12.7 mm, 14 faces (baked)
FEATURE [App::Part] COMPOUND007  label="COMPOUND055"
  Group = -> [Part__Feature632,Part__Feature633,Part__Feature634,Part__Feature635,Part__Feature636,Part__Feature637]
  Origin = -> Origin013
FEATURE [App::Part] Pin_Header_1x6_TH_Pitch_2_54mm_v004  label="Pin Header 1x6 TH Pitch 2.54mm v004"
  Group = -> [COMPOUND006,COMPOUND007]
  Origin = -> Origin014
  Placement = pos=(29.21,-7.62,-0.814) rot=(0,1,0;3.14159rad)
FEATURE [Part::Feature] Part__Feature638  label="COMPOUND056"
  shape: bbox 2.54 x 2.54 x 2.799 mm, 22 faces, 0 solids (baked)
FEATURE [Part::Feature] Part__Feature639  label="COMPOUND057"
  shape: bbox 2.54 x 2.54 x 2.799 mm, 22 faces, 0 solids (baked)
FEATURE [Part::Feature] Part__Feature640  label="COMPOUND058"
  shape: bbox 2.54 x 2.54 x 2.799 mm, 23 faces, 0 solids (baked)
FEATURE [Part::Feature] Part__Feature641  label="COMPOUND059"
  shape: bbox 2.54 x 2.54 x 2.799 mm, 22 faces, 0 solids (baked)
FEATURE [Part::Feature] Part__Feature642  label="COMPOUND060"
  shape: bbox 2.54 x 2.54 x 2.799 mm, 22 faces, 0 solids (baked)
FEATURE [Part::Feature] Part__Feature643  label="COMPOUND061"
  shape: bbox 2.54 x 2.54 x 2.799 mm, 23 faces, 0 solids (baked)
FEATURE [App::Part] COMPOUND008  label="COMPOUND062"
  Group = -> [Part__Feature638,Part__Feature639,Part__Feature640,Part__Feature641,Part__Feature642,Part__Feature643]
  Origin = -> Origin061
FEATURE [Part::Feature] Part__Feature644  label="COMPOUND063"
  shape: bbox 0.6304 x 0.63 x 12.7 mm, 14 faces (baked)
FEATURE [Part::Feature] Part__Feature645  label="COMPOUND064"
  shape: bbox 0.6304 x 0.63 x 12.7 mm, 14 faces (baked)
FEATURE [Part::Feature] Part__Feature646  label="COMPOUND065"
  shape: bbox 0.6304 x 0.63 x 12.7 mm, 14 faces (baked)
FEATURE [Part::Feature] Part__Feature647  label="COMPOUND066"
  shape: bbox 0.6304 x 0.63 x 12.7 mm, 14 faces (baked)
FEATURE [Part::Feature] Part__Feature648  label="COMPOUND067"
  shape: bbox 0.6304 x 0.63 x 12.7 mm, 14 faces (baked)
FEATURE [Part::Feature] Part__Feature649  label="COMPOUND068"
  shape: bbox 0.6304 x 0.63 x 12.7 mm, 14 faces (baked)
FEATURE [App::Part] COMPOUND009  label="COMPOUND069"
  Group = -> [Part__Feature644,Part__Feature645,Part__Feature646,Part__Feature647,Part__Feature648,Part__Feature649]
  Origin = -> Origin062
FEATURE [App::Part] Pin_Header_1x6_TH_Pitch_2_54mm_v1_Mirror_  label="Pin Header 1x6 TH Pitch 2.54mm v1(Mirror)"
  Group = -> [COMPOUND008,COMPOUND009]
  Origin = -> Origin017
  Placement = pos=(-16.51,7.62,-0.814) rot=(0,0,1;3.14159rad)
FEATURE [Part::Feature] Part__Feature650  label="COMPOUND070"
  shape: bbox 2.54 x 2.54 x 2.799 mm, 22 faces, 0 solids (baked)
FEATURE [Part::Feature] Part__Feature651  label="COMPOUND071"
  shape: bbox 2.54 x 2.54 x 2.799 mm, 22 faces, 0 solids (baked)
FEATURE [Part::Feature] Part__Feature652  label="COMPOUND072"
  shape: bbox 2.54 x 2.54 x 2.799 mm, 23 faces, 0 solids (baked)
FEATURE [Part::Feature] Part__Feature653  label="COMPOUND073"
  shape: bbox 2.54 x 2.54 x 2.799 mm, 22 faces, 0 solids (baked)
FEATURE [Part::Feature] Part__Feature654  label="COMPOUND074"
  shape: bbox 2.54 x 2.54 x 2.799 mm, 22 faces, 0 solids (baked)
FEATURE [Part::Feature] Part__Feature655  label="COMPOUND075"
  shape: bbox 2.54 x 2.54 x 2.799 mm, 23 faces, 0 solids (baked)
FEATURE [App::Part] COMPOUND010  label="COMPOUND076"
  Group = -> [Part__Feature650,Part__Feature651,Part__Feature652,Part__Feature653,Part__Feature654,Part__Feature655]
  Origin = -> Origin064
FEATURE [Part::Feature] Part__Feature656  label="COMPOUND077"
  shape: bbox 0.6304 x 0.63 x 12.7 mm, 14 faces (baked)
FEATURE [Part::Feature] Part__Feature657  label="COMPOUND078"
  shape: bbox 0.6304 x 0.63 x 12.7 mm, 14 faces (baked)
FEATURE [Part::Feature] Part__Feature658  label="COMPOUND079"
  shape: bbox 0.6304 x 0.63 x 12.7 mm, 14 faces (baked)
FEATURE [Part::Feature] Part__Feature659  label="COMPOUND080"
  shape: bbox 0.6304 x 0.63 x 12.7 mm, 14 faces (baked)
FEATURE [Part::Feature] Part__Feature660  label="COMPOUND081"
  shape: bbox 0.6304 x 0.63 x 12.7 mm, 14 faces (baked)
FEATURE [Part::Feature] Part__Feature661  label="COMPOUND082"
  shape: bbox 0.6304 x 0.63 x 12.7 mm, 14 faces (baked)
FEATURE [App::Part] COMPOUND011  label="COMPOUND083"
  Group = -> [Part__Feature656,Part__Feature657,Part__Feature658,Part__Feature659,Part__Feature660,Part__Feature661]
  Origin = -> Origin065
FEATURE [App::Part] Pin_Header_1x6_TH_Pitch_2_54mm_v1_Mirror_001  label="Pin Header 1x6 TH Pitch 2.54mm v1(Mirror)001"
  Group = -> [COMPOUND010,COMPOUND011]
  Origin = -> Origin063
  Placement = pos=(-1.27,7.62,-0.814) rot=(0,0,1;3.14159rad)
FEATURE [Part::Feature] Part__Feature662  label="COMPOUND084"
  shape: bbox 2.54 x 2.54 x 2.799 mm, 22 faces, 0 solids (baked)
FEATURE [Part::Feature] Part__Feature663  label="COMPOUND085"
  shape: bbox 2.54 x 2.54 x 2.799 mm, 22 faces, 0 solids (baked)
FEATURE [Part::Feature] Part__Feature664  label="COMPOUND086"
  shape: bbox 2.54 x 2.54 x 2.799 mm, 23 faces, 0 solids (baked)
FEATURE [Part::Feature] Part__Feature665  label="COMPOUND087"
  shape: bbox 2.54 x 2.54 x 2.799 mm, 22 faces, 0 solids (baked)
FEATURE [Part::Feature] Part__Feature666  label="COMPOUND088"
  shape: bbox 2.54 x 2.54 x 2.799 mm, 22 faces, 0 solids (baked)
FEATURE [Part::Feature] Part__Feature667  label="COMPOUND089"
  shape: bbox 2.54 x 2.54 x 2.799 mm, 23 faces, 0 solids (baked)
FEATURE [App::Part] COMPOUND012  label="COMPOUND090"
  Group = -> [Part__Feature662,Part__Feature663,Part__Feature664,Part__Feature665,Part__Feature666,Part__Feature667]
  Origin = -> Origin067
FEATURE [Part::Feature] Part__Feature668  label="COMPOUND091"
  shape: bbox 0.6304 x 0.63 x 12.7 mm, 14 faces (baked)
FEATURE [Part::Feature] Part__Feature669  label="COMPOUND092"
  shape: bbox 0.6304 x 0.63 x 12.7 mm, 14 faces (baked)
FEATURE [Part::Feature] Part__Feature670  label="COMPOUND093"
  shape: bbox 0.6304 x 0.63 x 12.7 mm, 14 faces (baked)
FEATURE [Part::Feature] Part__Feature671  label="COMPOUND094"
  shape: bbox 0.6304 x 0.63 x 12.7 mm, 14 faces (baked)
FEATURE [Part::Feature] Part__Feature672  label="COMPOUND095"
  shape: bbox 0.6304 x 0.63 x 12.7 mm, 14 faces (baked)
FEATURE [Part::Feature] Part__Feature673  label="COMPOUND096"
  shape: bbox 0.6304 x 0.63 x 12.7 mm, 14 faces (baked)
FEATURE [App::Part] COMPOUND013  label="COMPOUND097"
  Group = -> [Part__Feature668,Part__Feature669,Part__Feature670,Part__Feature671,Part__Feature672,Part__Feature673]
  Origin = -> Origin022
FEATURE [App::Part] Pin_Header_1x6_TH_Pitch_2_54mm_v1_Mirror_002  label="Pin Header 1x6 TH Pitch 2.54mm v1(Mirror)002"
  Group = -> [COMPOUND012,COMPOUND013]
  Origin = -> Origin066
  Placement = pos=(13.97,7.62,-0.814) rot=(0,0,1;3.14159rad)
FEATURE [Part::Feature] Part__Feature674  label="COMPOUND098"
  shape: bbox 2.54 x 2.54 x 2.799 mm, 22 faces, 0 solids (baked)
FEATURE [Part::Feature] Part__Feature675  label="COMPOUND099"
  shape: bbox 2.54 x 2.54 x 2.799 mm, 22 faces, 0 solids (baked)
FEATURE [Part::Feature] Part__Feature676  label="COMPOUND100"
  shape: bbox 2.54 x 2.54 x 2.799 mm, 23 faces, 0 solids (baked)
FEATURE [Part::Feature] Part__Feature677  label="COMPOUND101"
  shape: bbox 2.54 x 2.54 x 2.799 mm, 22 faces, 0 solids (baked)
FEATURE [Part::Feature] Part__Feature678  label="COMPOUND102"
  shape: bbox 2.54 x 2.54 x 2.799 mm, 22 faces, 0 solids (baked)
FEATURE [Part::Feature] Part__Feature679  label="COMPOUND103"
  shape: bbox 2.54 x 2.54 x 2.799 mm, 23 faces, 0 solids (baked)
FEATURE [App::Part] COMPOUND014  label="COMPOUND104"
  Group = -> [Part__Feature674,Part__Feature675,Part__Feature676,Part__Feature677,Part__Feature678,Part__Feature679]
  Origin = -> Origin069
FEATURE [Part::Feature] Part__Feature680  label="COMPOUND105"
  shape: bbox 0.6304 x 0.63 x 12.7 mm, 14 faces (baked)
FEATURE [Part::Feature] Part__Feature681  label="COMPOUND106"
  shape: bbox 0.6304 x 0.63 x 12.7 mm, 14 faces (baked)
FEATURE [Part::Feature] Part__Feature682  label="COMPOUND107"
  shape: bbox 0.6304 x 0.63 x 12.7 mm, 14 faces (baked)
FEATURE [Part::Feature] Part__Feature683  label="COMPOUND108"
  shape: bbox 0.6304 x 0.63 x 12.7 mm, 14 faces (baked)
FEATURE [Part::Feature] Part__Feature684  label="COMPOUND109"
  shape: bbox 0.6304 x 0.63 x 12.7 mm, 14 faces (baked)
FEATURE [Part::Feature] Part__Feature685  label="COMPOUND110"
  shape: bbox 0.6304 x 0.63 x 12.7 mm, 14 faces (baked)
FEATURE [App::Part] COMPOUND015  label="COMPOUND111"
  Group = -> [Part__Feature680,Part__Feature681,Part__Feature682,Part__Feature683,Part__Feature684,Part__Feature685]
  Origin = -> Origin070
FEATURE [App::Part] Pin_Header_1x6_TH_Pitch_2_54mm_v1_Mirror_003  label="Pin Header 1x6 TH Pitch 2.54mm v1(Mirror)003"
  Group = -> [COMPOUND014,COMPOUND015]
  Origin = -> Origin068
  Placement = pos=(29.21,7.62,-0.814) rot=(0,0,1;3.14159rad)
FEATURE [Part::Feature] Part__Feature686  label="COMPOUND112"
  shape: bbox 2.54 x 2.54 x 2.799 mm, 22 faces, 0 solids (baked)
FEATURE [Part::Feature] Part__Feature687  label="COMPOUND113"
  shape: bbox 2.54 x 2.54 x 2.799 mm, 22 faces, 0 solids (baked)
FEATURE [Part::Feature] Part__Feature688  label="COMPOUND114"
  shape: bbox 2.54 x 2.54 x 2.799 mm, 23 faces, 0 solids (baked)
FEATURE [Part::Feature] Part__Feature689  label="COMPOUND115"
  shape: bbox 2.54 x 2.54 x 2.799 mm, 22 faces, 0 solids (baked)
FEATURE [Part::Feature] Part__Feature690  label="COMPOUND116"
  shape: bbox 2.54 x 2.54 x 2.799 mm, 23 faces, 0 solids (baked)
FEATURE [App::Part] COMPOUND016  label="COMPOUND117"
  Group = -> [Part__Feature686,Part__Feature687,Part__Feature688,Part__Feature689,Part__Feature690]
  Origin = -> Origin027
FEATURE [Part::Feature] Part__Feature691  label="COMPOUND118"
  shape: bbox 0.6304 x 0.63 x 12.7 mm, 14 faces (baked)
FEATURE [Part::Feature] Part__Feature692  label="COMPOUND119"
  shape: bbox 0.6304 x 0.63 x 12.7 mm, 14 faces (baked)
FEATURE [Part::Feature] Part__Feature693  label="COMPOUND120"
  shape: bbox 0.6304 x 0.63 x 12.7 mm, 14 faces (baked)
FEATURE [Part::Feature] Part__Feature694  label="COMPOUND121"
  shape: bbox 0.6304 x 0.63 x 12.7 mm, 14 faces (baked)
FEATURE [Part::Feature] Part__Feature695  label="COMPOUND122"
  shape: bbox 0.6304 x 0.63 x 12.7 mm, 14 faces (baked)
FEATURE [App::Part] COMPOUND017  label="COMPOUND123"
  Group = -> [Part__Feature691,Part__Feature692,Part__Feature693,Part__Feature694,Part__Feature695]
  Origin = -> Origin028
FEATURE [App::Part] Pin_Header_1x5_TH_Pitch_2_54mm_v1  label="Pin Header 1x5 TH Pitch 2.54mm v1"
  Group = -> [COMPOUND016,COMPOUND017]
  Origin = -> Origin029
  Placement = pos=(-22.86,-4.7,-0.814) rot=(1,0,0;3.14159rad)
FEATURE [Part::Feature] Part__Feature696  label="COMPOUND124"
  shape: bbox 2.54 x 2.54 x 2.799 mm, 22 faces, 0 solids (baked)
FEATURE [Part::Feature] Part__Feature697  label="COMPOUND125"
  shape: bbox 2.54 x 2.54 x 2.799 mm, 22 faces, 0 solids (baked)
FEATURE [Part::Feature] Part__Feature698  label="COMPOUND126"
  shape: bbox 2.54 x 2.54 x 2.799 mm, 23 faces, 0 solids (baked)
FEATURE [Part::Feature] Part__Feature699  label="COMPOUND127"
  shape: bbox 2.54 x 2.54 x 2.799 mm, 22 faces, 0 solids (baked)
FEATURE [Part::Feature] Part__Feature700  label="COMPOUND128"
  shape: bbox 2.54 x 2.54 x 2.799 mm, 23 faces, 0 solids (baked)
FEATURE [App::Part] COMPOUND018  label="COMPOUND129"
  Group = -> [Part__Feature696,Part__Feature697,Part__Feature698,Part__Feature699,Part__Feature700]
  Origin = -> Origin030
FEATURE [Part::Feature] Part__Feature701  label="COMPOUND130"
  shape: bbox 0.6304 x 0.63 x 12.7 mm, 14 faces (baked)
FEATURE [Part::Feature] Part__Feature702  label="COMPOUND131"
  shape: bbox 0.6304 x 0.63 x 12.7 mm, 14 faces (baked)
FEATURE [Part::Feature] Part__Feature703  label="COMPOUND132"
  shape: bbox 0.6304 x 0.63 x 12.7 mm, 14 faces (baked)
FEATURE [Part::Feature] Part__Feature704  label="COMPOUND133"
  shape: bbox 0.6304 x 0.63 x 12.7 mm, 14 faces (baked)
FEATURE [Part::Feature] Part__Feature705  label="COMPOUND134"
  shape: bbox 0.6304 x 0.63 x 12.7 mm, 14 faces (baked)
FEATURE [App::Part] COMPOUND019  label="COMPOUND135"
  Group = -> [Part__Feature701,Part__Feature702,Part__Feature703,Part__Feature704,Part__Feature705]
  Origin = -> Origin031
FEATURE [App::Part] Pin_Header_1x5_TH_Pitch_2_54mm_v002  label="Pin Header 1x5 TH Pitch 2.54mm v002"
  Group = -> [COMPOUND018,COMPOUND019]
  Origin = -> Origin071
  Placement = pos=(16.51,-5.08,-0.814) rot=(0.707107,0.707107,0;3.14159rad)
FEATURE [Part::Feature] Part__Feature706  label="Pin Header 1x1 TH Pitch 2.54mm v1"
  Placement = pos=(-26.67,5.08,-0.814) rot=(0,1,0;3.14159rad)
  shape: bbox 2.54 x 2.54 x 2.799 mm, 24 faces (baked)
FEATURE [Part::Feature] Part__Feature707  label="Pin Header 1x1 TH Pitch 2.54mm v002"
  Placement = pos=(-26.67,5.08,-0.814) rot=(0,1,0;3.14159rad)
  shape: bbox 0.6304 x 0.63 x 12.7 mm, 14 faces (baked)
FEATURE [App::Part] Pin_Header_1x1_TH_Pitch_2_54mm_v1  label="Pin Header 1x1 TH Pitch 2.54mm v003"
  Group = -> [Part__Feature706,Part__Feature707]
  Origin = -> Origin072
FEATURE [Part::Feature] Part__Feature708  label="pin header 1x3 pitch 2mm heigth 5mm v1"
  Placement = pos=(128.76,5.04,-0.805) rot=(0.707107,-0.707107,0;3.14159rad)
  shape: bbox 0.5 x 0.5 x 8.7 mm, 14 faces (baked)
FEATURE [Part::Feature] Part__Feature709  label="pin header 1x3 pitch 2mm heigth 5mm v002"
  Placement = pos=(128.76,5.04,-0.805) rot=(0.707107,-0.707107,0;3.14159rad)
  shape: bbox 0.5 x 0.5 x 8.7 mm, 14 faces (baked)
FEATURE [Part::Feature] Part__Feature710  label="pin header 1x3 pitch 2mm heigth 5mm v003"
  Placement = pos=(128.76,5.04,-0.805) rot=(0.707107,-0.707107,0;3.14159rad)
  shape: bbox 0.5 x 0.5 x 8.7 mm, 14 faces (baked)
FEATURE [Part::Feature] Part__Feature711  label="pin header 1x3 pitch 2mm heigth 5mm v004"
  Placement = pos=(128.76,5.04,-0.805) rot=(0.707107,-0.707107,0;3.14159rad)
  shape: bbox 2 x 6 x 2 mm, 44 faces (baked)
FEATURE [App::Part] pin_header_1x3_pitch_2mm_heigth_5mm_v1  label="pin header 1x3 pitch 2mm heigth 5mm v005"
  Group = -> [Part__Feature708,Part__Feature709,Part__Feature710,Part__Feature711]
  Origin = -> Origin073
FEATURE [Part::Feature] Part__Feature712  label="pin header 1x3 pitch 2mm heigth 5mm v006"
  Placement = pos=(130.76,5.04,-0.805) rot=(0.707107,-0.707107,0;3.14159rad)
  shape: bbox 0.5 x 0.5 x 8.7 mm, 14 faces (baked)
FEATURE [Part::Feature] Part__Feature713  label="pin header 1x3 pitch 2mm heigth 5mm v007"
  Placement = pos=(130.76,5.04,-0.805) rot=(0.707107,-0.707107,0;3.14159rad)
  shape: bbox 0.5 x 0.5 x 8.7 mm, 14 faces (baked)
FEATURE [Part::Feature] Part__Feature714  label="pin header 1x3 pitch 2mm heigth 5mm v008"
  Placement = pos=(130.76,5.04,-0.805) rot=(0.707107,-0.707107,0;3.14159rad)
  shape: bbox 0.5 x 0.5 x 8.7 mm, 14 faces (baked)
FEATURE [Part::Feature] Part__Feature715  label="pin header 1x3 pitch 2mm heigth 5mm v009"
  Placement = pos=(130.76,5.04,-0.805) rot=(0.707107,-0.707107,0;3.14159rad)
  shape: bbox 2 x 6 x 2 mm, 44 faces (baked)
FEATURE [App::Part] pin_header_1x3_pitch_2mm_heigth_5mm_v002  label="pin header 1x3 pitch 2mm heigth 5mm v010"
  Group = -> [Part__Feature712,Part__Feature713,Part__Feature714,Part__Feature715]
  Origin = -> Origin074
FEATURE [Part::Feature] Part__Feature716  label="PTS810 SJK 250 SMTR LFS v1"
  Placement = pos=(12.85,-0.068585,1.06859) rot=(1,0,0;1.5708rad)
  shape: bbox 4.2 x 3.2 x 2 mm, 27 faces (baked)
FEATURE [Part::Feature] Part__Feature717  label="PTS810 SJK 250 SMTR LFS v002"
  Placement = pos=(12.85,-0.068585,1.06859) rot=(1,0,0;1.5708rad)
  shape: bbox 3.181 x 2.381 x 1.2 mm, 10 faces (baked)
FEATURE [Part::Feature] Part__Feature718  label="PTS810 SJK 250 SMTR LFS v003"
  Placement = pos=(12.85,-0.068585,1.06859) rot=(1,0,0;1.5708rad)
  shape: bbox 0.2 x 0.55 x 0.5 mm, 7 faces (baked)
FEATURE [Part::Feature] Part__Feature719  label="PTS810 SJK 250 SMTR LFS v004"
  Placement = pos=(12.85,-0.068585,1.06859) rot=(1,0,0;1.5708rad)
  shape: bbox 0.2 x 0.55 x 0.5 mm, 7 faces (baked)
FEATURE [Part::Feature] Part__Feature720  label="PTS810 SJK 250 SMTR LFS v005"
  Placement = pos=(12.85,-0.068585,1.06859) rot=(1,0,0;1.5708rad)
  shape: bbox 0.2 x 0.55 x 0.5 mm, 7 faces (baked)
FEATURE [Part::Feature] Part__Feature721  label="PTS810 SJK 250 SMTR LFS v006"
  Placement = pos=(12.85,-0.068585,1.06859) rot=(1,0,0;1.5708rad)
  shape: bbox 0.2 x 0.55 x 0.5 mm, 7 faces (baked)
FEATURE [App::Part] PTS810_SJK_250_SMTR_LFS_v1  label="PTS810 SJK 250 SMTR LFS v007"
  Group = -> [Part__Feature716,Part__Feature717,Part__Feature718,Part__Feature719,Part__Feature720,Part__Feature721]
  Origin = -> Origin075
FEATURE [Part::Feature] Part__Feature722  label="COMPOUND136"
  shape: bbox 60.96 x 17.78 x 1.63 mm, 71 faces (baked)
FEATURE [Part::Feature] Part__Feature723  label="COMPOUND137"
  shape: bbox 1.31 x 1.31 x 0.035 mm, 4 faces (baked)
FEATURE [Part::Feature] Part__Feature724  label="COMPOUND138"
  shape: bbox 1.31 x 1.31 x 0.035 mm, 4 faces (baked)
FEATURE [Part::Feature] Part__Feature725  label="COMPOUND139"
  shape: bbox 1.31 x 1.31 x 0.035 mm, 4 faces (baked)
FEATURE [Part::Feature] Part__Feature726  label="COMPOUND140"
  shape: bbox 1.31 x 1.31 x 0.035 mm, 4 faces (baked)
FEATURE [Part::Feature] Part__Feature727  label="COMPOUND141"
  shape: bbox 1.31 x 1.31 x 0.035 mm, 4 faces (baked)
FEATURE [Part::Feature] Part__Feature728  label="COMPOUND142"
  shape: bbox 1.31 x 1.31 x 0.035 mm, 4 faces (baked)
FEATURE [Part::Feature] Part__Feature729  label="COMPOUND143"
  shape: bbox 1.31 x 1.31 x 0.035 mm, 4 faces (baked)
FEATURE [Part::Feature] Part__Feature730  label="COMPOUND144"
  shape: bbox 1.31 x 1.31 x 0.035 mm, 4 faces (baked)
FEATURE [Part::Feature] Part__Feature731  label="COMPOUND145"
  shape: bbox 1.31 x 1.31 x 0.035 mm, 4 faces (baked)
FEATURE [Part::Feature] Part__Feature732  label="COMPOUND146"
  shape: bbox 1.31 x 1.31 x 0.035 mm, 4 faces (baked)
FEATURE [Part::Feature] Part__Feature733  label="COMPOUND147"
  shape: bbox 1.21 x 1.21 x 0.035 mm, 4 faces (baked)
FEATURE [Part::Feature] Part__Feature734  label="COMPOUND148"
  shape: bbox 1.21 x 1.21 x 0.035 mm, 4 faces (baked)
FEATURE [Part::Feature] Part__Feature735  label="COMPOUND149"
  shape: bbox 1.21 x 1.21 x 0.035 mm, 4 faces (baked)
FEATURE [Part::Feature] Part__Feature736  label="COMPOUND150"
  shape: bbox 1.21 x 1.21 x 0.035 mm, 4 faces (baked)
FEATURE [Part::Feature] Part__Feature737  label="COMPOUND151"
  shape: bbox 1.21 x 1.21 x 0.035 mm, 4 faces (baked)
FEATURE [Part::Feature] Part__Feature738  label="COMPOUND152"
  shape: bbox 1.21 x 1.21 x 0.035 mm, 4 faces (baked)
FEATURE [Part::Feature] Part__Feature739  label="COMPOUND153"
  shape: bbox 1.21 x 1.21 x 0.035 mm, 4 faces (baked)
FEATURE [Part::Feature] Part__Feature740  label="COMPOUND154"
  shape: bbox 1.21 x 1.21 x 0.035 mm, 4 faces (baked)
FEATURE [Part::Feature] Part__Feature741  label="COMPOUND155"
  shape: bbox 1.21 x 1.21 x 0.035 mm, 4 faces (baked)
FEATURE [Part::Feature] Part__Feature742  label="COMPOUND156"
  shape: bbox 1.21 x 1.21 x 0.035 mm, 4 faces (baked)
FEATURE [Part::Feature] Part__Feature743  label="COMPOUND157"
  shape: bbox 1.21 x 1.21 x 0.035 mm, 4 faces (baked)
FEATURE [Part::Feature] Part__Feature744  label="COMPOUND158"
  shape: bbox 1.21 x 1.21 x 0.035 mm, 4 faces (baked)
FEATURE [App::Part] COMPOUND020  label="COMPOUND159"
  Group = -> [Part__Feature722,Part__Feature723,Part__Feature724,Part__Feature725,Part__Feature726,Part__Feature727,Part__Feature728,Part__Feature729,Part__Feature730,Part__Feature731,Part__Feature732,Part__Feature733,Part__Feature734,Part__Feature735,Part__Feature736,Part__Feature737,Part__Feature738,Part__Feature739,Part__Feature740,Part__Feature741,Part__Feature742,Part__Feature743,Part__Feature744]
  Origin = -> Origin076
FEATURE [App::Part] Teensy4_1_v22  label="Teensy 4.1 "
  Group = -> [_14_00841_68__3DModel_STEP_56544_v1,MIMXRT1052CVJ5B_v1,Part__Feature589,Pin_Header_1x6_TH_Pitch_2_54mm_v1,Pin_Header_1x6_TH_Pitch_2_54mm_v002,Pin_Header_1x6_TH_Pitch_2_54mm_v003,Pin_Header_1x6_TH_Pitch_2_54mm_v004,Pin_Header_1x6_TH_Pitch_2_54mm_v1_Mirror_,Pin_Header_1x6_TH_Pitch_2_54mm_v1_Mirror_001,Pin_Header_1x6_TH_Pitch_2_54mm_v1_Mirror_002,Pin_Header_1x6_TH_Pitch_2_54mm_v1_Mirror_003,+7 more]
  Origin = -> Origin050
  Placement = pos=(33.7332,-0.281902,31) rot=(0,0,-1;4.71239rad)
FEATURE [Part::Sphere] Sphere  label="Ball"
  Angle1 = -90
  Angle2 = 90
  Angle3 = 360
  AttacherType = Attacher::AttachEngine3D
  Placement = pos=(-86,0,-21) rot=(0,1,0;1.5708rad)
  Radius = 21
FEATURE [Sketcher::SketchObject] Sketch065
  FullyConstrained = true
  MapMode = 5
  Support = -> [XY_Plane226]
  sketch-geometry (12):
    g0: LineSegment StartX=101.78 StartY=40.22 StartZ=0 EndX=101.78 EndY=32.22 EndZ=0
    g1: LineSegment StartX=-66.22 StartY=32.22 StartZ=0 EndX=-66.22 EndY=40.22 EndZ=0
    g2: LineSegment StartX=-66.22 StartY=32.22 StartZ=0 EndX=7.78 EndY=32.22 EndZ=0
    g3: LineSegment StartX=7.78 StartY=32.22 StartZ=0 EndX=7.78 EndY=0 EndZ=0
    g4: LineSegment StartX=7.78 StartY=0 StartZ=0 EndX=27.78 EndY=0 EndZ=0
    g5: LineSegment StartX=27.78 StartY=0 StartZ=0 EndX=27.78 EndY=32.22 EndZ=0
    g6: LineSegment StartX=27.78 StartY=32.22 StartZ=0 EndX=101.78 EndY=32.22 EndZ=0
    g7: LineSegment StartX=-66.22 StartY=40.22 StartZ=0 EndX=0 EndY=40.22 EndZ=0
    g8: LineSegment StartX=101.78 StartY=40.22 StartZ=0 EndX=35.56 EndY=40.22 EndZ=0
    g9: LineSegment StartX=0 StartY=40.22 StartZ=0 EndX=0 EndY=44.52 EndZ=0
    g10: LineSegment StartX=0 StartY=44.52 StartZ=0 EndX=35.56 EndY=44.52 EndZ=0
    g11: LineSegment StartX=35.56 StartY=44.52 StartZ=0 EndX=35.56 EndY=40.22 EndZ=0
  constraints (36):
    c: Vertical(g0)
    c: Vertical(g1)
    c: DistanceY(g0,g0) = 8
    c: Coincident(g2,g1)
    c: Horizontal(g2)
    c: Vertical(g3)
    c: Coincident(g4,g3)
    c: Horizontal(g4)
    c: Coincident(g5,g4)
    c: Vertical(g5)
    c: Coincident(g6,g5)
    c: Coincident(g6,g0)
    c: Horizontal(g6)
    c: Equal(g2,g6)
    c: Horizontal(g2,g5)
    c: DistanceX(g1,g0) = 168
    c: Coincident(g7,g1)
    c: PointOnObject(g7,g-2)
    c: Horizontal(g7)
    c: Coincident(g8,g0)
    c: Horizontal(g8)
    c: DistanceX(g7,g8) = 35.56
    c: Equal(g1,g0)
    c: Coincident(g9,g7)
    c: Vertical(g9)
    c: Coincident(g10,g9)
    c: Horizontal(g10)
    c: Coincident(g11,g10)
    c: Coincident(g11,g8)
    c: Vertical(g11)
    c: DistanceY(g11,g11) = 4.3
    c: PointOnObject(g4,g-1)
    c: Coincident(g2,g3)
    c: DistanceX(g6,g6) = 74
    c: DistanceX(g1,g-1) = 66.22
    c: DistanceY(g-1,g1) = 32.22
FEATURE [PartDesign::Pad] Pad044
  Direction = (0,0,1)
  Length = 6
  Length2 = 10
  Profile = -> Sketch065
  ReferenceAxis = -> Sketch065 [N_Axis]
  Reversed = true
  Type = 0
FEATURE [Sketcher::SketchObject] Sketch074
  FullyConstrained = true
  MapMode = 5
  Support = -> [XY_Plane229]
  sketch-geometry (1):
    g0: Circle CenterX=0 CenterY=0 CenterZ=0 NormalX=0 NormalY=0 NormalZ=1 AngleXU=0 Radius=12
  constraints (2):
    c: Diameter(g0) = 24
    c: Coincident(g0,g-1)
FEATURE [PartDesign::Pad] Pad051
  Direction = (0,0,1)
  Length = 56.5
  Length2 = 10
  Profile = -> Sketch074
  ReferenceAxis = -> Sketch074 [N_Axis]
  Type = 0
FEATURE [Sketcher::SketchObject] Sketch075
  FullyConstrained = true
  MapMode = 5
  Support = -> [XY_Plane230]
  sketch-geometry (1):
    g0: Circle CenterX=0 CenterY=0 CenterZ=0 NormalX=0 NormalY=0 NormalZ=1 AngleXU=0 Radius=12
  constraints (2):
    c: Diameter(g0) = 24
    c: Coincident(g0,g-1)
FEATURE [PartDesign::Pad] Pad052
  Direction = (0,0,1)
  Length = 56.5
  Length2 = 10
  Profile = -> Sketch075
  ReferenceAxis = -> Sketch075 [N_Axis]
  Type = 0
FEATURE [Sketcher::SketchObject] Sketch079
  FullyConstrained = true
  MapMode = 5
  Support = -> [XY_Plane234]
  sketch-geometry (2):
    g0: Circle CenterX=0 CenterY=0 CenterZ=0 NormalX=0 NormalY=0 NormalZ=1 AngleXU=0 Radius=62.5
    g1: Circle CenterX=0 CenterY=0 CenterZ=0 NormalX=0 NormalY=0 NormalZ=1 AngleXU=0 Radius=47.5
  constraints (4):
    c: Coincident(g0,g-1)
    c: Coincident(g1,g0)
    c: Diameter(g1) = 95
    c: Diameter(g0) = 125
FEATURE [PartDesign::Pad] Pad055
  Direction = (0,0,1)
  Length = 1.6
  Length2 = 10
  Profile = -> Sketch079
  ReferenceAxis = -> Sketch079 [N_Axis]
  Type = 0
FEATURE [Sketcher::SketchObject] Sketch080
  FullyConstrained = true
  MapMode = 5
  Placement = pos=(0,0,0) rot=(1,0,0;3.14159rad)
  Support = -> [Pad055]
  sketch-geometry (4):
    g0: LineSegment StartX=-57 StartY=4 StartZ=0 EndX=-53 EndY=4 EndZ=0
    g1: LineSegment StartX=-53 StartY=4 StartZ=0 EndX=-53 EndY=-4 EndZ=0
    g2: LineSegment StartX=-53 StartY=-4 StartZ=0 EndX=-57 EndY=-4 EndZ=0
    g3: LineSegment StartX=-57 StartY=-4 StartZ=0 EndX=-57 EndY=4 EndZ=0
  constraints (11):
    c: Coincident(g0,g1)
    c: Coincident(g1,g2)
    c: Coincident(g2,g3)
    c: Coincident(g3,g0)
    c: Horizontal(g0)
    c: Horizontal(g2)
    c: Vertical(g3)
    c: DistanceX(g0,g0) = 4
    c: DistanceY(g3,g3) = 8
    c: Symmetric(g1,g0,g-1)
    c: DistanceX(g1,g-1) = 53
FEATURE [PartDesign::Pad] Pad056
  BaseFeature = -> Pad055
  Direction = (0,0,-1)
  Length = 1.5
  Length2 = 10
  Profile = -> Sketch080
  ReferenceAxis = -> Sketch080 [N_Axis]
  Type = 0
FEATURE [PartDesign::PolarPattern] PolarPattern011
  Angle = 360
  Axis = -> Sketch080 [N_Axis]
  BaseFeature = -> Pad056
  Occurrences = 20
  Originals = -> [Pad056]
FEATURE [PartDesign::Body] Body032  label="Line board"
  Group = -> [Sketch079,Pad055,Sketch080,Pad056,PolarPattern011]
  Origin = -> Origin234
  Placement = pos=(0,0,2) rot=(0,0,1;0rad)
  Tip = -> PolarPattern011
FEATURE [App::Part] Part010  label="Line PCB"
  Group = -> [Body032]
  Origin = -> Origin233
  Placement = pos=(0,0,-38) rot=(0,0,1;0rad)
FEATURE [Sketcher::SketchObject] Sketch081
  FullyConstrained = true
  MapMode = 5
  Support = -> [XY_Plane235]
  sketch-geometry (1):
    g0: Circle CenterX=0 CenterY=0 CenterZ=0 NormalX=0 NormalY=0 NormalZ=1 AngleXU=0 Radius=12
  constraints (2):
    c: Diameter(g0) = 24
    c: Coincident(g0,g-1)
FEATURE [PartDesign::Pad] Pad057
  Direction = (0,0,1)
  Length = 56.5
  Length2 = 10
  Profile = -> Sketch081
  ReferenceAxis = -> Sketch081 [N_Axis]
  Type = 0
FEATURE [Sketcher::SketchObject] Sketch082
  FullyConstrained = true
  MapMode = 5
  Placement = pos=(0,0,0) rot=(1,0,0;1.5708rad)
  Support = -> [XZ_Plane237]
  sketch-geometry (1):
    g0: Circle CenterX=0 CenterY=0 CenterZ=0 NormalX=0 NormalY=0 NormalZ=1 AngleXU=0 Radius=12
  constraints (2):
    c: Coincident(g0,g-1)
    c: Diameter(g0) = 24
FEATURE [PartDesign::Pad] Pad058
  Direction = (0,-1,-2e-16)
  Length = 50
  Length2 = 10
  Placement = pos=(0,0,0) rot=(1,0,0;1.5708rad)
  Profile = -> Sketch082
  ReferenceAxis = -> Sketch082 [N_Axis]
  Reversed = true
  Type = 0
FEATURE [Sketcher::SketchObject] Sketch083
  FullyConstrained = true
  MapMode = 5
  Placement = pos=(0,0,0) rot=(1,0,0;1.5708rad)
  Support = -> [XZ_Plane238]
  sketch-geometry (1):
    g0: Circle CenterX=0 CenterY=0 CenterZ=0 NormalX=0 NormalY=0 NormalZ=1 AngleXU=0 Radius=9
  constraints (2):
    c: Coincident(g0,g-1)
    c: Diameter(g0) = 18
FEATURE [PartDesign::Pad] Pad059
  Direction = (0,-1,-2e-16)
  Length = 62
  Length2 = 10
  Placement = pos=(0,0,0) rot=(1,0,0;1.5708rad)
  Profile = -> Sketch083
  ReferenceAxis = -> Sketch083 [N_Axis]
  Reversed = true
  Type = 0
FEATURE [PartDesign::Body] Body035  label="Dribbler roll"
  Group = -> [Sketch083,Pad059]
  Origin = -> Origin238
  Placement = pos=(-74,-32.5,4) rot=(0,1,0;3.14159rad)
  Tip = -> Pad059
FEATURE [Part::Part2DObjectPython] InvoluteGear009  # Draft 2D object (typed FeaturePython)
  AddendumCoefficient = 1
  DedendumCoefficient = 1.25
  ExternalGear = true
  HighPrecision = true
  Modules = 0.6
  NumberOfTeeth = 16
  PressureAngle = 20
  ProfileShiftCoefficient = 0
  RootFilletCoefficient = 0.38
FEATURE [PartDesign::Pad] Pad060
  Direction = (0,0,1)
  Length = 3
  Length2 = 10
  Profile = -> InvoluteGear009
  ReferenceAxis = -> InvoluteGear009 [N_Axis]
  Reversed = true
  Type = 0
FEATURE [PartDesign::Body] Body036  label="Dribbler gear 1"
  Group = -> [InvoluteGear009,Pad060]
  Origin = -> Origin239
  Placement = pos=(-74,29.5,4) rot=(1,0,0;1.5708rad)
  Tip = -> Pad060
FEATURE [Part::Part2DObjectPython] InvoluteGear010  # Draft 2D object (typed FeaturePython)
  AddendumCoefficient = 1
  DedendumCoefficient = 1.25
  ExternalGear = true
  HighPrecision = true
  Modules = 0.7
  NumberOfTeeth = 16
  PressureAngle = 20
  ProfileShiftCoefficient = 0
  RootFilletCoefficient = 0.38
FEATURE [PartDesign::Pad] Pad061
  Direction = (0,0,1)
  Length = 3
  Length2 = 10
  Profile = -> InvoluteGear010
  ReferenceAxis = -> InvoluteGear010 [N_Axis]
  Reversed = true
  Type = 0
FEATURE [PartDesign::Body] Body037  label="Dribbler gear 2"
  Group = -> [InvoluteGear010,Pad061]
  Origin = -> Origin240
  Placement = pos=(-48.5,30.5,17.9) rot=(1,0,0;1.5708rad)
  Tip = -> Pad061
FEATURE [Sketcher::SketchObject] Sketch084
  FullyConstrained = true
  MapMode = 5
  Placement = pos=(0,0,0) rot=(1,0,0;1.5708rad)
  Support = -> [XZ_Plane241]
  sketch-geometry (5):
    g0: Circle CenterX=0 CenterY=0 CenterZ=0 NormalX=0 NormalY=0 NormalZ=1 AngleXU=0 Radius=5
    g1: LineSegment StartX=-13 StartY=18 StartZ=0 EndX=13 EndY=18 EndZ=0
    g2: LineSegment StartX=-13 StartY=18 StartZ=0 EndX=-13 EndY=-3.6e-15 EndZ=0
    g3: LineSegment StartX=13 StartY=18 StartZ=0 EndX=13 EndY=-3.6e-15 EndZ=0
    g4: ArcOfCircle CenterX=0 CenterY=0 CenterZ=0 NormalX=0 NormalY=0 NormalZ=1 AngleXU=0 Radius=13 StartAngle=3.14159 EndAngle=6.28319
  constraints (13):
    c: Coincident(g0,g-1)
    c: Diameter(g0) = 10
    c: DistanceX(g1,g1) = 26
    c: Symmetric(g1,g1,g-2)
    c: DistanceY(g0,g1) = 18
    c: Coincident(g2,g1)
    c: PointOnObject(g2,g-1)
    c: Vertical(g2)
    c: Coincident(g3,g1)
    c: PointOnObject(g3,g-1)
    c: Coincident(g4,g0)
    c: Coincident(g4,g2)
    c: Coincident(g4,g3)
FEATURE [PartDesign::Pad] Pad062
  Direction = (0,-1,-2e-16)
  Length = 3
  Length2 = 10
  Placement = pos=(0,0,0) rot=(1,0,0;1.5708rad)
  Profile = -> Sketch084
  ReferenceAxis = -> Sketch084 [N_Axis]
  Type = 0
FEATURE [Sketcher::SketchObject] Sketch085
  ExternalGeometry = -> [Pad062]
  FullyConstrained = true
  MapMode = 5
  Placement = pos=(0,-3,0) rot=(1,0,0;1.5708rad)
  Support = -> [Pad062]
  sketch-geometry (4):
    g0: LineSegment StartX=-13 StartY=18 StartZ=0 EndX=-13 EndY=14 EndZ=0
    g1: LineSegment StartX=-13 StartY=14 StartZ=0 EndX=13 EndY=14 EndZ=0
    g2: LineSegment StartX=13 StartY=14 StartZ=0 EndX=13 EndY=18 EndZ=0
    g3: LineSegment StartX=13 StartY=18 StartZ=0 EndX=-13 EndY=18 EndZ=0
  constraints (10):
    c: Coincident(g0,g-3)
    c: Vertical(g0)
    c: Coincident(g1,g0)
    c: Horizontal(g1)
    c: Coincident(g2,g1)
    c: Coincident(g2,g-3)
    c: Vertical(g2)
    c: Coincident(g3,g2)
    c: Coincident(g3,g0)
    c: DistanceY(g0,g0) = 4
FEATURE [PartDesign::Pad] Pad063
  BaseFeature = -> Pad062
  Direction = (0,-1,-2e-16)
  Length = 30
  Length2 = 10
  Placement = pos=(0,0,0) rot=(1,0,0;1.5708rad)
  Profile = -> Sketch085
  ReferenceAxis = -> Sketch085 [N_Axis]
  Type = 0
FEATURE [Sketcher::SketchObject] Sketch086
  ExternalGeometry = -> [Pad063]
  FullyConstrained = true
  MapMode = 5
  Placement = pos=(0,4e-15,18) rot=(0,0,1;3.14159rad)
  Support = -> [Pad063]
  sketch-geometry (4):
    g0: Circle CenterX=-9 CenterY=7 CenterZ=0 NormalX=0 NormalY=0 NormalZ=1 AngleXU=0 Radius=2
    g1: Circle CenterX=9 CenterY=7 CenterZ=0 NormalX=0 NormalY=0 NormalZ=1 AngleXU=0 Radius=2
    g2: Circle CenterX=-9 CenterY=29 CenterZ=0 NormalX=0 NormalY=0 NormalZ=1 AngleXU=0 Radius=2
    g3: Circle CenterX=9 CenterY=29 CenterZ=0 NormalX=0 NormalY=0 NormalZ=1 AngleXU=0 Radius=2
  constraints (10):
    c: Diameter(g2) = 4
    c: Diameter(g3) = 4
    c: Diameter(g1) = 4
    c: Diameter(g0) = 4
    c: Symmetric(g2,g3,g-2)
    c: Symmetric(g0,g1,g-2)
    c: Vertical(g2,g0)
    c: DistanceX(g-4,g2) = 4
    c: DistanceY(g2,g-4) = 4
    c: DistanceY(g-4,g0) = 4
FEATURE [PartDesign::Pocket] Pocket029
  BaseFeature = -> Pad063
  Direction = (0,2e-16,-1)
  Length = 5
  Length2 = 5
  Placement = pos=(0,0,0) rot=(1,0,0;1.5708rad)
  Profile = -> Sketch086
  ReferenceAxis = -> Sketch086 [N_Axis]
  Type = 1
FEATURE [Sketcher::SketchObject] Sketch087
  FullyConstrained = true
  MapMode = 5
  Placement = pos=(0,0,0) rot=(-1,0,0;1.5708rad)
  Support = -> [Pocket029]
  sketch-geometry (1):
    g0: Circle CenterX=0 CenterY=9.5 CenterZ=0 NormalX=0 NormalY=0 NormalZ=1 AngleXU=0 Radius=1
  constraints (3):
    c: PointOnObject(g0,g-2)
    c: Diameter(g0) = 2
    c: DistanceY(g-1,g0) = 9.5
FEATURE [PartDesign::Pocket] Pocket030
  BaseFeature = -> Pocket029
  Direction = (0,-1,-2e-16)
  Length = 5
  Length2 = 5
  Placement = pos=(0,0,0) rot=(1,0,0;1.5708rad)
  Profile = -> Sketch087
  ReferenceAxis = -> Sketch087 [N_Axis]
  Type = 1
FEATURE [PartDesign::PolarPattern] PolarPattern012
  Angle = 360
  Axis = -> Sketch087 [N_Axis]
  BaseFeature = -> Pocket030
  Occurrences = 4
  Originals = -> [Pocket030]
  Placement = pos=(0,0,0) rot=(1,0,0;1.5708rad)
FEATURE [PartDesign::SubShapeBinder] Binder
  BindCopyOnChange = 0
  BindMode = 0
  ClaimChildren = false
  Context = -> Body [Binder.]
  Fuse = false
  MakeFace = true
  OffsetFill = false
  OffsetIntersection = false
  OffsetJoinType = 0
  OffsetOpenResult = false
  PartialLoad = false
  Relative = true
  Support = -> [Part003[Part005.Body038.Pocket029.Sketch086.]]
  _Version = 2
FEATURE [Sketcher::SketchObject] Sketch088
  FullyConstrained = true
  MapMode = 5
  Placement = pos=(0,0,0) rot=(1,0,0;1.5708rad)
  Support = -> [XZ_Plane242]
  sketch-geometry (5):
    g0: Circle CenterX=0 CenterY=0 CenterZ=0 NormalX=0 NormalY=0 NormalZ=1 AngleXU=0 Radius=6
    g1: LineSegment StartX=-13 StartY=18 StartZ=0 EndX=13 EndY=18 EndZ=0
    g2: LineSegment StartX=-13 StartY=18 StartZ=0 EndX=-13 EndY=0 EndZ=0
    g3: LineSegment StartX=13 StartY=18 StartZ=0 EndX=13 EndY=-3.6e-15 EndZ=0
    g4: ArcOfCircle CenterX=0 CenterY=0 CenterZ=0 NormalX=0 NormalY=0 NormalZ=1 AngleXU=0 Radius=13 StartAngle=3.14159 EndAngle=6.28319
  constraints (13):
    c: Coincident(g0,g-1)
    c: Diameter(g0) = 12
    c: DistanceX(g1,g1) = 26
    c: Symmetric(g1,g1,g-2)
    c: DistanceY(g0,g1) = 18
    c: Coincident(g2,g1)
    c: PointOnObject(g2,g-1)
    c: Vertical(g2)
    c: Coincident(g3,g1)
    c: PointOnObject(g3,g-1)
    c: Coincident(g4,g0)
    c: Coincident(g4,g2)
    c: Coincident(g4,g3)
FEATURE [PartDesign::Pad] Pad064
  Direction = (0,-1,-2e-16)
  Length = 3
  Length2 = 10
  Placement = pos=(0,0,0) rot=(1,0,0;1.5708rad)
  Profile = -> Sketch088
  ReferenceAxis = -> Sketch088 [N_Axis]
  Type = 0
FEATURE [Sketcher::SketchObject] Sketch089
  ExternalGeometry = -> [Pad064]
  FullyConstrained = true
  MapMode = 5
  Placement = pos=(0,-3,0) rot=(1,0,0;1.5708rad)
  Support = -> [Pad064]
  sketch-geometry (4):
    g0: LineSegment StartX=-13 StartY=18 StartZ=0 EndX=-13 EndY=14 EndZ=0
    g1: LineSegment StartX=-13 StartY=14 StartZ=0 EndX=13 EndY=14 EndZ=0
    g2: LineSegment StartX=13 StartY=14 StartZ=0 EndX=13 EndY=18 EndZ=0
    g3: LineSegment StartX=13 StartY=18 StartZ=0 EndX=-13 EndY=18 EndZ=0
  constraints (10):
    c: Coincident(g0,g-3)
    c: Vertical(g0)
    c: Coincident(g1,g0)
    c: Horizontal(g1)
    c: Coincident(g2,g1)
    c: Coincident(g2,g-3)
    c: Vertical(g2)
    c: Coincident(g3,g2)
    c: Coincident(g3,g0)
    c: DistanceY(g0,g0) = 4
FEATURE [PartDesign::Pad] Pad065
  BaseFeature = -> Pad064
  Direction = (0,-1,-2e-16)
  Length = 30
  Length2 = 10
  Placement = pos=(0,0,0) rot=(1,0,0;1.5708rad)
  Profile = -> Sketch089
  ReferenceAxis = -> Sketch089 [N_Axis]
  Type = 0
FEATURE [Sketcher::SketchObject] Sketch090
  ExternalGeometry = -> [Pad065]
  FullyConstrained = true
  MapMode = 5
  Placement = pos=(0,4e-15,18) rot=(0,0,1;3.14159rad)
  Support = -> [Pad065]
  sketch-geometry (4):
    g0: Circle CenterX=-9 CenterY=7 CenterZ=0 NormalX=0 NormalY=0 NormalZ=1 AngleXU=0 Radius=2
    g1: Circle CenterX=9 CenterY=7 CenterZ=0 NormalX=0 NormalY=0 NormalZ=1 AngleXU=0 Radius=2
    g2: Circle CenterX=-9 CenterY=29 CenterZ=0 NormalX=0 NormalY=0 NormalZ=1 AngleXU=0 Radius=2
    g3: Circle CenterX=9 CenterY=29 CenterZ=0 NormalX=0 NormalY=0 NormalZ=1 AngleXU=0 Radius=2
  constraints (10):
    c: Diameter(g2) = 4
    c: Diameter(g3) = 4
    c: Diameter(g1) = 4
    c: Diameter(g0) = 4
    c: Symmetric(g2,g3,g-2)
    c: Symmetric(g0,g1,g-2)
    c: Vertical(g2,g0)
    c: DistanceX(g-4,g2) = 4
    c: DistanceY(g2,g-4) = 4
    c: DistanceY(g-4,g0) = 4
FEATURE [PartDesign::Pocket] Pocket032
  BaseFeature = -> Pad065
  Direction = (0,2e-16,-1)
  Length = 5
  Length2 = 5
  Placement = pos=(0,0,0) rot=(1,0,0;1.5708rad)
  Profile = -> Sketch090
  ReferenceAxis = -> Sketch090 [N_Axis]
  Type = 1
FEATURE [Sketcher::SketchObject] Sketch091
  FullyConstrained = true
  MapMode = 5
  Placement = pos=(0,0,0) rot=(-1,0,0;1.5708rad)
  Support = -> [Pocket032]
  sketch-geometry (1):
    g0: Circle CenterX=0 CenterY=9.5 CenterZ=0 NormalX=0 NormalY=0 NormalZ=1 AngleXU=0 Radius=1
  constraints (3):
    c: PointOnObject(g0,g-2)
    c: Diameter(g0) = 2
    c: DistanceY(g-1,g0) = 9.5
FEATURE [PartDesign::Pocket] Pocket033
  BaseFeature = -> Pocket032
  Direction = (0,-1,-2e-16)
  Length = 5
  Length2 = 5
  Placement = pos=(0,0,0) rot=(1,0,0;1.5708rad)
  Profile = -> Sketch091
  ReferenceAxis = -> Sketch091 [N_Axis]
  Type = 1
FEATURE [PartDesign::PolarPattern] PolarPattern013
  Angle = 360
  Axis = -> Sketch091 [N_Axis]
  BaseFeature = -> Pocket033
  Occurrences = 4
  Originals = -> [Pocket033]
  Placement = pos=(0,0,0) rot=(1,0,0;1.5708rad)
FEATURE [PartDesign::Body] Body039  label="Moteur support 2"
  Group = -> [Sketch088,Pad064,Sketch089,Pad065,Sketch090,Pocket032,Sketch091,Pocket033,PolarPattern013]
  Origin = -> Origin242
  Placement = pos=(43.5918,62.2556,-8) rot=(0,0,-1;0.610865rad)
  Tip = -> PolarPattern013
FEATURE [Sketcher::SketchObject] Sketch092
  FullyConstrained = true
  MapMode = 5
  Placement = pos=(0,0,0) rot=(1,0,0;1.5708rad)
  Support = -> [XZ_Plane243]
  sketch-geometry (5):
    g0: Circle CenterX=0 CenterY=0 CenterZ=0 NormalX=0 NormalY=0 NormalZ=1 AngleXU=0 Radius=6
    g1: LineSegment StartX=-13 StartY=18 StartZ=0 EndX=13 EndY=18 EndZ=0
    g2: LineSegment StartX=-13 StartY=18 StartZ=0 EndX=-13 EndY=0 EndZ=0
    g3: LineSegment StartX=13 StartY=18 StartZ=0 EndX=13 EndY=-3.6e-15 EndZ=0
    g4: ArcOfCircle CenterX=0 CenterY=0 CenterZ=0 NormalX=0 NormalY=0 NormalZ=1 AngleXU=0 Radius=13 StartAngle=3.14159 EndAngle=6.28319
  constraints (13):
    c: Coincident(g0,g-1)
    c: Diameter(g0) = 12
    c: DistanceX(g1,g1) = 26
    c: Symmetric(g1,g1,g-2)
    c: DistanceY(g0,g1) = 18
    c: Coincident(g2,g1)
    c: PointOnObject(g2,g-1)
    c: Vertical(g2)
    c: Coincident(g3,g1)
    c: PointOnObject(g3,g-1)
    c: Coincident(g4,g0)
    c: Coincident(g4,g2)
    c: Coincident(g4,g3)
FEATURE [PartDesign::Pad] Pad066
  Direction = (0,-1,-2e-16)
  Length = 3
  Length2 = 10
  Placement = pos=(0,0,0) rot=(1,0,0;1.5708rad)
  Profile = -> Sketch092
  ReferenceAxis = -> Sketch092 [N_Axis]
  Type = 0
FEATURE [Sketcher::SketchObject] Sketch093
  ExternalGeometry = -> [Pad066]
  FullyConstrained = true
  MapMode = 5
  Placement = pos=(0,-3,0) rot=(1,0,0;1.5708rad)
  Support = -> [Pad066]
  sketch-geometry (4):
    g0: LineSegment StartX=-13 StartY=18 StartZ=0 EndX=-13 EndY=14 EndZ=0
    g1: LineSegment StartX=-13 StartY=14 StartZ=0 EndX=13 EndY=14 EndZ=0
    g2: LineSegment StartX=13 StartY=14 StartZ=0 EndX=13 EndY=18 EndZ=0
    g3: LineSegment StartX=13 StartY=18 StartZ=0 EndX=-13 EndY=18 EndZ=0
  constraints (10):
    c: Coincident(g0,g-3)
    c: Vertical(g0)
    c: Coincident(g1,g0)
    c: Horizontal(g1)
    c: Coincident(g2,g1)
    c: Coincident(g2,g-3)
    c: Vertical(g2)
    c: Coincident(g3,g2)
    c: Coincident(g3,g0)
    c: DistanceY(g0,g0) = 4
FEATURE [PartDesign::Pad] Pad067
  BaseFeature = -> Pad066
  Direction = (0,-1,-2e-16)
  Length = 30
  Length2 = 10
  Placement = pos=(0,0,0) rot=(1,0,0;1.5708rad)
  Profile = -> Sketch093
  ReferenceAxis = -> Sketch093 [N_Axis]
  Type = 0
FEATURE [Sketcher::SketchObject] Sketch094
  ExternalGeometry = -> [Pad067]
  FullyConstrained = true
  MapMode = 5
  Placement = pos=(0,4e-15,18) rot=(0,0,1;3.14159rad)
  Support = -> [Pad067]
  sketch-geometry (4):
    g0: Circle CenterX=-9 CenterY=7 CenterZ=0 NormalX=0 NormalY=0 NormalZ=1 AngleXU=0 Radius=2
    g1: Circle CenterX=9 CenterY=7 CenterZ=0 NormalX=0 NormalY=0 NormalZ=1 AngleXU=0 Radius=2
    g2: Circle CenterX=-9 CenterY=29 CenterZ=0 NormalX=0 NormalY=0 NormalZ=1 AngleXU=0 Radius=2
    g3: Circle CenterX=9 CenterY=29 CenterZ=0 NormalX=0 NormalY=0 NormalZ=1 AngleXU=0 Radius=2
  constraints (10):
    c: Diameter(g2) = 4
    c: Diameter(g3) = 4
    c: Diameter(g1) = 4
    c: Diameter(g0) = 4
    c: Symmetric(g2,g3,g-2)
    c: Symmetric(g0,g1,g-2)
    c: Vertical(g2,g0)
    c: DistanceX(g-4,g2) = 4
    c: DistanceY(g2,g-4) = 4
    c: DistanceY(g-4,g0) = 4
FEATURE [PartDesign::Pocket] Pocket034
  BaseFeature = -> Pad067
  Direction = (0,2e-16,-1)
  Length = 5
  Length2 = 5
  Placement = pos=(0,0,0) rot=(1,0,0;1.5708rad)
  Profile = -> Sketch094
  ReferenceAxis = -> Sketch094 [N_Axis]
  Type = 1
FEATURE [Sketcher::SketchObject] Sketch095
  FullyConstrained = true
  MapMode = 5
  Placement = pos=(0,0,0) rot=(-1,0,0;1.5708rad)
  Support = -> [Pocket034]
  sketch-geometry (1):
    g0: Circle CenterX=0 CenterY=9.5 CenterZ=0 NormalX=0 NormalY=0 NormalZ=1 AngleXU=0 Radius=1
  constraints (3):
    c: PointOnObject(g0,g-2)
    c: Diameter(g0) = 2
    c: DistanceY(g-1,g0) = 9.5
FEATURE [PartDesign::Pocket] Pocket035
  BaseFeature = -> Pocket034
  Direction = (0,-1,-2e-16)
  Length = 5
  Length2 = 5
  Placement = pos=(0,0,0) rot=(1,0,0;1.5708rad)
  Profile = -> Sketch095
  ReferenceAxis = -> Sketch095 [N_Axis]
  Type = 1
FEATURE [PartDesign::PolarPattern] PolarPattern014
  Angle = 360
  Axis = -> Sketch095 [N_Axis]
  BaseFeature = -> Pocket035
  Occurrences = 4
  Originals = -> [Pocket035]
  Placement = pos=(0,0,0) rot=(1,0,0;1.5708rad)
FEATURE [PartDesign::Body] Body040  label="Moteur support 3"
  Group = -> [Sketch092,Pad066,Sketch093,Pad067,Sketch094,Pocket034,Sketch095,Pocket035,PolarPattern014]
  Origin = -> Origin243
  Placement = pos=(43.5918,-62.2556,-8) rot=(0,0,1;3.75246rad)
  Tip = -> PolarPattern014
FEATURE [Sketcher::SketchObject] Sketch096
  FullyConstrained = true
  MapMode = 5
  Placement = pos=(0,0,0) rot=(1,0,0;1.5708rad)
  Support = -> [XZ_Plane244]
  sketch-geometry (5):
    g0: Circle CenterX=0 CenterY=0 CenterZ=0 NormalX=0 NormalY=0 NormalZ=1 AngleXU=0 Radius=6
    g1: LineSegment StartX=-13 StartY=18 StartZ=0 EndX=13 EndY=18 EndZ=0
    g2: LineSegment StartX=-13 StartY=18 StartZ=0 EndX=-13 EndY=0 EndZ=0
    g3: LineSegment StartX=13 StartY=18 StartZ=0 EndX=13 EndY=-3.6e-15 EndZ=0
    g4: ArcOfCircle CenterX=0 CenterY=0 CenterZ=0 NormalX=0 NormalY=0 NormalZ=1 AngleXU=0 Radius=13 StartAngle=3.14159 EndAngle=6.28319
  constraints (13):
    c: Coincident(g0,g-1)
    c: Diameter(g0) = 12
    c: DistanceX(g1,g1) = 26
    c: Symmetric(g1,g1,g-2)
    c: DistanceY(g0,g1) = 18
    c: Coincident(g2,g1)
    c: PointOnObject(g2,g-1)
    c: Vertical(g2)
    c: Coincident(g3,g1)
    c: PointOnObject(g3,g-1)
    c: Coincident(g4,g0)
    c: Coincident(g4,g2)
    c: Coincident(g4,g3)
FEATURE [PartDesign::Pad] Pad068
  Direction = (0,-1,-2e-16)
  Length = 3
  Length2 = 10
  Placement = pos=(0,0,0) rot=(1,0,0;1.5708rad)
  Profile = -> Sketch096
  ReferenceAxis = -> Sketch096 [N_Axis]
  Type = 0
FEATURE [Sketcher::SketchObject] Sketch097
  ExternalGeometry = -> [Pad068]
  FullyConstrained = true
  MapMode = 5
  Placement = pos=(0,-3,0) rot=(1,0,0;1.5708rad)
  Support = -> [Pad068]
  sketch-geometry (4):
    g0: LineSegment StartX=-13 StartY=18 StartZ=0 EndX=-13 EndY=14 EndZ=0
    g1: LineSegment StartX=-13 StartY=14 StartZ=0 EndX=13 EndY=14 EndZ=0
    g2: LineSegment StartX=13 StartY=14 StartZ=0 EndX=13 EndY=18 EndZ=0
    g3: LineSegment StartX=13 StartY=18 StartZ=0 EndX=-13 EndY=18 EndZ=0
  constraints (10):
    c: Coincident(g0,g-3)
    c: Vertical(g0)
    c: Coincident(g1,g0)
    c: Horizontal(g1)
    c: Coincident(g2,g1)
    c: Coincident(g2,g-3)
    c: Vertical(g2)
    c: Coincident(g3,g2)
    c: Coincident(g3,g0)
    c: DistanceY(g0,g0) = 4
FEATURE [PartDesign::Pad] Pad069
  BaseFeature = -> Pad068
  Direction = (0,-1,-2e-16)
  Length = 30
  Length2 = 10
  Placement = pos=(0,0,0) rot=(1,0,0;1.5708rad)
  Profile = -> Sketch097
  ReferenceAxis = -> Sketch097 [N_Axis]
  Type = 0
FEATURE [Sketcher::SketchObject] Sketch098
  ExternalGeometry = -> [Pad069]
  FullyConstrained = true
  MapMode = 5
  Placement = pos=(0,4e-15,18) rot=(0,0,1;3.14159rad)
  Support = -> [Pad069]
  sketch-geometry (4):
    g0: Circle CenterX=-9 CenterY=7 CenterZ=0 NormalX=0 NormalY=0 NormalZ=1 AngleXU=0 Radius=2
    g1: Circle CenterX=9 CenterY=7 CenterZ=0 NormalX=0 NormalY=0 NormalZ=1 AngleXU=0 Radius=2
    g2: Circle CenterX=-9 CenterY=29 CenterZ=0 NormalX=0 NormalY=0 NormalZ=1 AngleXU=0 Radius=2
    g3: Circle CenterX=9 CenterY=29 CenterZ=0 NormalX=0 NormalY=0 NormalZ=1 AngleXU=0 Radius=2
  constraints (10):
    c: Diameter(g2) = 4
    c: Diameter(g3) = 4
    c: Diameter(g1) = 4
    c: Diameter(g0) = 4
    c: Symmetric(g2,g3,g-2)
    c: Symmetric(g0,g1,g-2)
    c: Vertical(g2,g0)
    c: DistanceX(g-4,g2) = 4
    c: DistanceY(g2,g-4) = 4
    c: DistanceY(g-4,g0) = 4
FEATURE [PartDesign::Pocket] Pocket036
  BaseFeature = -> Pad069
  Direction = (0,2e-16,-1)
  Length = 5
  Length2 = 5
  Placement = pos=(0,0,0) rot=(1,0,0;1.5708rad)
  Profile = -> Sketch098
  ReferenceAxis = -> Sketch098 [N_Axis]
  Type = 1
FEATURE [Sketcher::SketchObject] Sketch099
  FullyConstrained = true
  MapMode = 5
  Placement = pos=(0,0,0) rot=(-1,0,0;1.5708rad)
  Support = -> [Pocket036]
  sketch-geometry (1):
    g0: Circle CenterX=0 CenterY=9.5 CenterZ=0 NormalX=0 NormalY=0 NormalZ=1 AngleXU=0 Radius=1
  constraints (3):
    c: PointOnObject(g0,g-2)
    c: Diameter(g0) = 2
    c: DistanceY(g-1,g0) = 9.5
FEATURE [PartDesign::Pocket] Pocket037
  BaseFeature = -> Pocket036
  Direction = (0,-1,-2e-16)
  Length = 5
  Length2 = 5
  Placement = pos=(0,0,0) rot=(1,0,0;1.5708rad)
  Profile = -> Sketch099
  ReferenceAxis = -> Sketch099 [N_Axis]
  Type = 1
FEATURE [PartDesign::PolarPattern] PolarPattern015
  Angle = 360
  Axis = -> Sketch099 [N_Axis]
  BaseFeature = -> Pocket037
  Occurrences = 4
  Originals = -> [Pocket037]
  Placement = pos=(0,0,0) rot=(1,0,0;1.5708rad)
FEATURE [PartDesign::Body] Body041  label="Moteur support 4"
  Group = -> [Sketch096,Pad068,Sketch097,Pad069,Sketch098,Pocket036,Sketch099,Pocket037,PolarPattern015]
  Origin = -> Origin244
  Placement = pos=(-43.5918,-62.2556,-8) rot=(0,0,1;2.53073rad)
  Tip = -> PolarPattern015
FEATURE [PartDesign::SubShapeBinder] Binder005
  BindCopyOnChange = 0
  BindMode = 0
  ClaimChildren = false
  Context = -> Body [Binder005.]
  Fuse = false
  MakeFace = true
  OffsetFill = false
  OffsetIntersection = false
  OffsetJoinType = 0
  OffsetOpenResult = false
  PartialLoad = false
  Relative = true
  Support = -> [Part003[Part006.Body039.Pocket032.Sketch090.]]
  _Version = 2
FEATURE [PartDesign::Pocket] Pocket031
  BaseFeature = -> Pocket019
  Direction = (0,-2e-16,-1)
  Length = 5
  Length2 = 5
  Profile = -> Binder
  Reversed = true
  Type = 1
FEATURE [PartDesign::Pocket] Pocket038
  BaseFeature = -> Pocket031
  Direction = (-2e-16,0,-1)
  Length = 5
  Length2 = 5
  Profile = -> Binder005
  Reversed = true
  Type = 1
FEATURE [PartDesign::SubShapeBinder] Binder006
  BindCopyOnChange = 0
  BindMode = 0
  ClaimChildren = false
  Context = -> Body [Binder006.]
  Fuse = false
  MakeFace = true
  OffsetFill = false
  OffsetIntersection = false
  OffsetJoinType = 0
  OffsetOpenResult = false
  PartialLoad = false
  Relative = true
  Support = -> [Part003[Part007.Body040.Pocket034.Sketch094.]]
  _Version = 2
FEATURE [PartDesign::Pocket] Pocket039
  BaseFeature = -> Pocket038
  Direction = (0,2e-16,-1)
  Length = 5
  Length2 = 5
  Profile = -> Binder006
  Reversed = true
  Type = 1
FEATURE [PartDesign::SubShapeBinder] Binder007
  BindCopyOnChange = 0
  BindMode = 0
  ClaimChildren = false
  Context = -> Body [Binder007.]
  Fuse = false
  MakeFace = true
  OffsetFill = false
  OffsetIntersection = false
  OffsetJoinType = 0
  OffsetOpenResult = false
  PartialLoad = false
  Relative = true
  Support = -> [Part003[Part008.Body041.Pocket036.Sketch098.]]
  _Version = 2
FEATURE [PartDesign::Pocket] Pocket040
  BaseFeature = -> Pocket039
  Direction = (2e-16,0,-1)
  Length = 5
  Length2 = 5
  Profile = -> Binder007
  Reversed = true
  Type = 1
FEATURE [Sketcher::SketchObject] Sketch102
  FullyConstrained = true
  MapMode = 5
  Support = -> [XY_Plane248]
  sketch-geometry (1):
    g0: Circle CenterX=0 CenterY=0 CenterZ=0 NormalX=0 NormalY=0 NormalZ=1 AngleXU=0 Radius=85
  constraints (2):
    c: Coincident(g0,g-1)
    c: Diameter(g0) = 170
FEATURE [PartDesign::Pad] Pad070  label="Structural layer001"
  Direction = (0,0,1)
  Length = 3
  Length2 = 10
  Profile = -> Sketch102
  ReferenceAxis = -> Sketch102 [N_Axis]
  Type = 0
FEATURE [Sketcher::SketchObject] Sketch106
  FullyConstrained = true
  MapMode = 5
  Placement = pos=(0,0,0) rot=(0.57735,0.57735,0.57735;2.0944rad)
  Support = -> [YZ_Plane250]
  sketch-geometry (2):
    g0: Circle CenterX=0 CenterY=0 CenterZ=0 NormalX=0 NormalY=0 NormalZ=1 AngleXU=0 Radius=5
    g1: Circle CenterX=0 CenterY=0 CenterZ=0 NormalX=0 NormalY=0 NormalZ=1 AngleXU=0 Radius=6.5
  constraints (4):
    c: Coincident(g0,g-1)
    c: Diameter(g0) = 10
    c: Coincident(g1,g0)
    c: Diameter(g1) = 13
FEATURE [PartDesign::Pad] Pad071
  Direction = (1,-2e-16,3e-16)
  Length = 30
  Length2 = 10
  Placement = pos=(0,0,0) rot=(0.57735,0.57735,0.57735;2.0944rad)
  Profile = -> Sketch106
  ReferenceAxis = -> Sketch106 [N_Axis]
  Type = 0
FEATURE [Sketcher::SketchObject] Sketch107
  ExternalGeometry = -> [Pad071]
  FullyConstrained = true
  MapMode = 5
  Placement = pos=(0,0,0) rot=(0.57735,0.57735,-0.57735;4.18879rad)
  Support = -> [Pad071]
  sketch-geometry (5):
    g0: LineSegment StartX=-12.5 StartY=15 StartZ=0 EndX=12.5 EndY=15 EndZ=0
    g1: LineSegment StartX=-12.5 StartY=1.5e-15 StartZ=0 EndX=-12.5 EndY=15 EndZ=0
    g2: Circle CenterX=0 CenterY=0 CenterZ=0 NormalX=0 NormalY=0 NormalZ=1 AngleXU=0 Radius=6.5
    g3: LineSegment StartX=12.5 StartY=15 StartZ=0 EndX=12.5 EndY=-3.6e-15 EndZ=0
    g4: ArcOfCircle CenterX=0 CenterY=0 CenterZ=0 NormalX=0 NormalY=0 NormalZ=1 AngleXU=0 Radius=12.5 StartAngle=3.14159 EndAngle=6.28319
  constraints (14):
    c: Coincident(g1,g0)
    c: Horizontal(g0)
    c: Coincident(g2,g-3)
    c: Tangent(g2,g-3)
    c: PointOnObject(g1,g-1)
    c: DistanceX(g0,g0) = 25
    c: Vertical(g1)
    c: DistanceY(g1,g1) = 15
    c: Coincident(g3,g0)
    c: Vertical(g3)
    c: Coincident(g4,g2)
    c: Coincident(g4,g1)
    c: Coincident(g4,g3)
    c: PointOnObject(g3,g-1)
FEATURE [PartDesign::Pad] Pad074
  BaseFeature = -> Pad071
  Direction = (-1,4e-16,-4e-16)
  Length = 3
  Length2 = 10
  Placement = pos=(0,0,0) rot=(0.57735,0.57735,0.57735;2.0944rad)
  Profile = -> Sketch107
  ReferenceAxis = -> Sketch107 [N_Axis]
  Reversed = true
  Type = 0
FEATURE [Sketcher::SketchObject] Sketch108
  ExternalGeometry = -> [Pad074]
  FullyConstrained = true
  MapMode = 5
  Placement = pos=(30,-6.6e-15,6.6e-15) rot=(0.57735,0.57735,0.57735;2.0944rad)
  Support = -> [Pad074]
  sketch-geometry (5):
    g0: Circle CenterX=-5.6e-15 CenterY=1.4e-15 CenterZ=0 NormalX=0 NormalY=0 NormalZ=1 AngleXU=0 Radius=6.5
    g1: LineSegment StartX=-12.5 StartY=-15 StartZ=0 EndX=-12.5 EndY=3.6e-15 EndZ=0
    g2: LineSegment StartX=12.5 StartY=1.4e-15 StartZ=0 EndX=12.5 EndY=-15 EndZ=0
    g3: LineSegment StartX=12.5 StartY=-15 StartZ=0 EndX=-12.5 EndY=-15 EndZ=0
    g4: ArcOfCircle CenterX=-5.6e-15 CenterY=1.4e-15 CenterZ=0 NormalX=0 NormalY=0 NormalZ=1 AngleXU=0 Radius=12.5 StartAngle=0 EndAngle=3.14159
  constraints (11):
    c: Coincident(g0,g-6)
    c: Tangent(g0,g-6)
    c: Coincident(g1,g-7)
    c: Coincident(g1,g-4)
    c: Coincident(g2,g-5)
    c: Coincident(g2,g-7)
    c: Coincident(g3,g2)
    c: Coincident(g3,g1)
    c: Coincident(g4,g0)
    c: Coincident(g4,g1)
    c: Coincident(g4,g2)
FEATURE [PartDesign::Pad] Pad075
  BaseFeature = -> Pad074
  Direction = (1,-9e-16,6e-16)
  Length = 3
  Length2 = 10
  Placement = pos=(0,0,0) rot=(0.57735,0.57735,0.57735;2.0944rad)
  Profile = -> Sketch108
  ReferenceAxis = -> Sketch108 [N_Axis]
  Reversed = true
  Type = 0
FEATURE [PartDesign::Body] Body045  label="Kicker body"
  Group = -> [Sketch106,Pad071,Sketch107,Pad074,Sketch108,Pad075]
  Origin = -> Origin250
  Placement = pos=(-62,0,0) rot=(0,0,1;0rad)
  Tip = -> Pad075
FEATURE [Sketcher::SketchObject] Sketch109
  FullyConstrained = true
  MapMode = 5
  Placement = pos=(0,0,0) rot=(0.57735,0.57735,0.57735;2.0944rad)
  Support = -> [YZ_Plane251]
  sketch-geometry (4):
    g0: LineSegment StartX=-40 StartY=7 StartZ=0 EndX=40 EndY=7 EndZ=0
    g1: LineSegment StartX=40 StartY=7 StartZ=0 EndX=40 EndY=-7 EndZ=0
    g2: LineSegment StartX=40 StartY=-7 StartZ=0 EndX=-40 EndY=-7 EndZ=0
    g3: LineSegment StartX=-40 StartY=-7 StartZ=0 EndX=-40 EndY=7 EndZ=0
  constraints (10):
    c: Coincident(g0,g1)
    c: Coincident(g1,g2)
    c: Coincident(g2,g3)
    c: Coincident(g3,g0)
    c: Horizontal(g2)
    c: Vertical(g1)
    c: Symmetric(g2,g0,g-1)
    c: Symmetric(g0,g0,g-2)
    c: DistanceX(g0,g0) = 80
    c: DistanceY(g1,g1) = 14
FEATURE [PartDesign::Pad] Pad076
  Direction = (1,-2e-16,3e-16)
  Length = 3
  Length2 = 10
  Placement = pos=(0,0,0) rot=(0.57735,0.57735,0.57735;2.0944rad)
  Profile = -> Sketch109
  ReferenceAxis = -> Sketch109 [N_Axis]
  Type = 0
FEATURE [Sketcher::SketchObject] Sketch119
  FullyConstrained = true
  MapMode = 5
  Support = -> [XY_Plane254]
  sketch-geometry (4):
    g0: LineSegment StartX=-64 StartY=10 StartZ=0 EndX=-28 EndY=10 EndZ=0
    g1: LineSegment StartX=-28 StartY=10 StartZ=0 EndX=-28 EndY=-10 EndZ=0
    g2: LineSegment StartX=-28 StartY=-10 StartZ=0 EndX=-64 EndY=-10 EndZ=0
    g3: LineSegment StartX=-64 StartY=-10 StartZ=0 EndX=-64 EndY=10 EndZ=0
  constraints (11):
    c: Coincident(g0,g1)
    c: Coincident(g1,g2)
    c: Coincident(g2,g3)
    c: Coincident(g3,g0)
    c: Horizontal(g0)
    c: Horizontal(g2)
    c: Vertical(g1)
    c: DistanceY(g1,g1) = 20
    c: DistanceX(g0,g0) = 36
    c: DistanceX(g1,g-1) = 28
    c: Symmetric(g2,g0,g-1)
FEATURE [PartDesign::Pad] Pad083
  Direction = (0,0,1)
  Length = 26
  Length2 = 10
  Profile = -> Sketch119
  ReferenceAxis = -> Sketch119 [N_Axis]
  Type = 0
FEATURE [Sketcher::SketchObject] Sketch120
  ExternalGeometry = -> [Pad083]
  FullyConstrained = true
  MapMode = 5
  Placement = pos=(-28,0,0) rot=(0.57735,0.57735,0.57735;2.0944rad)
  Support = -> [Pad083]
  sketch-geometry (1):
    g0: Circle CenterX=0 CenterY=13 CenterZ=0 NormalX=0 NormalY=0 NormalZ=1 AngleXU=0 Radius=5
  constraints (3):
    c: PointOnObject(g0,g-2)
    c: Diameter(g0) = 10
    c: DistanceY(g0,g-3) = 13
FEATURE [PartDesign::Pad] Pad084
  BaseFeature = -> Pad083
  Direction = (1,0,0)
  Length = 20
  Length2 = 10
  Profile = -> Sketch120
  ReferenceAxis = -> Sketch120 [N_Axis]
  Type = 0
FEATURE [Sketcher::SketchObject] Sketch121
  FullyConstrained = true
  MapMode = 5
  Placement = pos=(0,0,0) rot=(1,0,0;1.5708rad)
  Support = -> [XZ_Plane255]
  sketch-geometry (5):
    g0: Circle CenterX=0 CenterY=0 CenterZ=0 NormalX=0 NormalY=0 NormalZ=1 AngleXU=0 Radius=6
    g1: LineSegment StartX=-13 StartY=17 StartZ=0 EndX=13 EndY=17 EndZ=0
    g2: LineSegment StartX=-13 StartY=17 StartZ=0 EndX=-13 EndY=0 EndZ=0
    g3: LineSegment StartX=13 StartY=17 StartZ=0 EndX=13 EndY=-3.6e-15 EndZ=0
    g4: ArcOfCircle CenterX=0 CenterY=0 CenterZ=0 NormalX=0 NormalY=0 NormalZ=1 AngleXU=0 Radius=13 StartAngle=3.14159 EndAngle=6.28319
  constraints (13):
    c: Coincident(g0,g-1)
    c: Diameter(g0) = 12
    c: DistanceX(g1,g1) = 26
    c: Symmetric(g1,g1,g-2)
    c: DistanceY(g0,g1) = 17
    c: Coincident(g2,g1)
    c: PointOnObject(g2,g-1)
    c: Vertical(g2)
    c: Coincident(g3,g1)
    c: PointOnObject(g3,g-1)
    c: Coincident(g4,g0)
    c: Coincident(g4,g2)
    c: Coincident(g4,g3)
FEATURE [PartDesign::Pad] Pad085
  Direction = (0,-1,2e-16)
  Length = 3
  Length2 = 10
  Placement = pos=(0,0,0) rot=(1,0,0;1.5708rad)
  Profile = -> Sketch121
  ReferenceAxis = -> Sketch121 [N_Axis]
  Type = 0
FEATURE [Sketcher::SketchObject] Sketch122
  ExternalGeometry = -> [Pad085]
  FullyConstrained = true
  MapMode = 5
  Placement = pos=(0,-3,1.3e-15) rot=(1,0,0;1.5708rad)
  Support = -> [Pad085]
  sketch-geometry (4):
    g0: LineSegment StartX=-13 StartY=17 StartZ=0 EndX=-13 EndY=14 EndZ=0
    g1: LineSegment StartX=-13 StartY=14 StartZ=0 EndX=13 EndY=14 EndZ=0
    g2: LineSegment StartX=13 StartY=14 StartZ=0 EndX=13 EndY=17 EndZ=0
    g3: LineSegment StartX=13 StartY=17 StartZ=0 EndX=-13 EndY=17 EndZ=0
  constraints (10):
    c: Coincident(g0,g-3)
    c: Vertical(g0)
    c: Coincident(g1,g0)
    c: Horizontal(g1)
    c: Coincident(g2,g1)
    c: Coincident(g2,g-3)
    c: Vertical(g2)
    c: Coincident(g3,g2)
    c: Coincident(g3,g0)
    c: DistanceY(g0,g0) = 3
FEATURE [PartDesign::Pad] Pad086
  BaseFeature = -> Pad085
  Direction = (0,-1,2e-16)
  Length = 30
  Length2 = 10
  Placement = pos=(0,0,0) rot=(1,0,0;1.5708rad)
  Profile = -> Sketch122
  ReferenceAxis = -> Sketch122 [N_Axis]
  Type = 0
FEATURE [Sketcher::SketchObject] Sketch123
  ExternalGeometry = -> [Pad086]
  FullyConstrained = true
  MapMode = 5
  Placement = pos=(2.4e-15,1.13e-14,17) rot=(0,0,1;3.14159rad)
  Support = -> [Pad086]
  sketch-geometry (4):
    g0: Circle CenterX=-9 CenterY=7 CenterZ=0 NormalX=0 NormalY=0 NormalZ=1 AngleXU=0 Radius=2
    g1: Circle CenterX=9 CenterY=7 CenterZ=0 NormalX=0 NormalY=0 NormalZ=1 AngleXU=0 Radius=2
    g2: Circle CenterX=-9 CenterY=29 CenterZ=0 NormalX=0 NormalY=0 NormalZ=1 AngleXU=0 Radius=2
    g3: Circle CenterX=9 CenterY=29 CenterZ=0 NormalX=0 NormalY=0 NormalZ=1 AngleXU=0 Radius=2
  constraints (10):
    c: Diameter(g2) = 4
    c: Diameter(g3) = 4
    c: Diameter(g1) = 4
    c: Diameter(g0) = 4
    c: Symmetric(g2,g3,g-2)
    c: Symmetric(g0,g1,g-2)
    c: Vertical(g2,g0)
    c: DistanceX(g-4,g2) = 4
    c: DistanceY(g2,g-4) = 4
    c: DistanceY(g-4,g0) = 4
FEATURE [PartDesign::Pocket] Pocket048
  BaseFeature = -> Pad086
  Direction = (-1e-16,-2e-16,-1)
  Length = 5
  Length2 = 5
  Placement = pos=(0,0,0) rot=(1,0,0;1.5708rad)
  Profile = -> Sketch123
  ReferenceAxis = -> Sketch123 [N_Axis]
  Type = 1
FEATURE [Sketcher::SketchObject] Sketch124
  FullyConstrained = true
  MapMode = 5
  Placement = pos=(0,0,0) rot=(-1,0,0;1.5708rad)
  Support = -> [Pocket048]
  sketch-geometry (1):
    g0: Circle CenterX=0 CenterY=9.5 CenterZ=0 NormalX=0 NormalY=0 NormalZ=1 AngleXU=0 Radius=1
  constraints (3):
    c: PointOnObject(g0,g-2)
    c: Diameter(g0) = 2
    c: DistanceY(g-1,g0) = 9.5
FEATURE [PartDesign::Pocket] Pocket049
  BaseFeature = -> Pocket048
  Direction = (0,-1,2e-16)
  Length = 5
  Length2 = 5
  Placement = pos=(0,0,0) rot=(1,0,0;1.5708rad)
  Profile = -> Sketch124
  ReferenceAxis = -> Sketch124 [N_Axis]
  Type = 1
FEATURE [PartDesign::PolarPattern] PolarPattern018
  Angle = 360
  Axis = -> Sketch124 [N_Axis]
  BaseFeature = -> Pocket049
  Occurrences = 4
  Originals = -> [Pocket049]
  Placement = pos=(0,0,0) rot=(1,0,0;1.5708rad)
FEATURE [PartDesign::SubShapeBinder] Binder008
  BindCopyOnChange = 0
  BindMode = 0
  ClaimChildren = false
  Context = -> Body [Binder008.]
  Fuse = false
  MakeFace = true
  OffsetFill = false
  OffsetIntersection = false
  OffsetJoinType = 0
  OffsetOpenResult = false
  PartialLoad = false
  Relative = true
  Support = -> [Part011[Body050.Pocket048.Sketch123.]]
  _Version = 2
FEATURE [PartDesign::Pocket] Pocket050
  BaseFeature = -> Pocket040
  Direction = (4e-16,6e-16,-1)
  Length = 5
  Length2 = 5
  Profile = -> Binder008
  Type = 1
FEATURE [PartDesign::SubShapeBinder] Binder010
  BindCopyOnChange = 0
  BindMode = 0
  ClaimChildren = false
  Context = -> openmv4_h7 [Body025.Binder010.]
  Fuse = false
  MakeFace = true
  OffsetFill = false
  OffsetIntersection = false
  OffsetJoinType = 0
  OffsetOpenResult = false
  PartialLoad = false
  Relative = true
  Support = -> [openmv4_h7_base________________[Part__Feature.Edge64,Part__Feature.Edge872,Part__Feature.Edge120,Part__Feature.Edge886]]
  _Version = 2
FEATURE [PartDesign::Pocket] Pocket052
  BaseFeature = -> Pad044
  Direction = (0,0,-1)
  Length = 5
  Length2 = 5
  Profile = -> Binder010
  Type = 1
FEATURE [Sketcher::SketchObject] Sketch126
  FullyConstrained = false
  MapMode = 5
  Placement = pos=(0,0,2) rot=(0,0,1;0rad)
  sketch-geometry (8):
    g0: Circle CenterX=-65.799 CenterY=-46 CenterZ=0 NormalX=0 NormalY=0 NormalZ=1 AngleXU=0 Radius=1.5
    g1: Circle CenterX=-46 CenterY=-65.799 CenterZ=0 NormalX=0 NormalY=0 NormalZ=1 AngleXU=0 Radius=1.5
    g2: LineSegment StartX=103.375 StartY=103.375 StartZ=0 EndX=-110.971 EndY=-110.971 EndZ=0
    g3: LineSegment StartX=0 StartY=0 StartZ=0 EndX=106.113 EndY=-106.113 EndZ=0
    g4: Circle CenterX=25 CenterY=-75.9117 CenterZ=0 NormalX=0 NormalY=0 NormalZ=1 AngleXU=0 Radius=1.5
    g5: Circle CenterX=75.9117 CenterY=-25 CenterZ=0 NormalX=0 NormalY=0 NormalZ=1 AngleXU=0 Radius=1.5
    g6: Circle CenterX=65.799 CenterY=46 CenterZ=0 NormalX=0 NormalY=0 NormalZ=1 AngleXU=0 Radius=1.5
    g7: Circle CenterX=46 CenterY=65.799 CenterZ=0 NormalX=0 NormalY=0 NormalZ=1 AngleXU=0 Radius=1.5
  constraints (19):
    c: Diameter(g1) = 3
    c: Diameter(g0) = 3
    c: Angle(g2,g-1) = 2.35619
    c: Symmetric(g1,g0,g2)
    c: Distance(g1,g2) = 14
    c: Distance(g1,g-2) = 46
    c: PointOnObject(g-1,g2)
    c: Coincident(g3,g-1)
    c: Perpendicular(g2,g3)
    c: Diameter(g7) = 3
    c: Diameter(g6) = 3
    c: Diameter(g5) = 3
    c: Diameter(g4) = 3
    c: Symmetric(g4,g5,g3)
    c: Symmetric(g7,g6,g2)
    c: Distance(g4,g3) = 36
    c: Distance(g6,g2) = 14
    c: Distance(g4,g-2) = 25
    c: Distance(g7,g-2) = 46
FEATURE [PartDesign::Pocket] Pocket055
  BaseFeature = -> Pocket050
  Direction = (0,0,-1)
  Length = 50
  Length2 = 5
  Profile = -> Sketch126
  ReferenceAxis = -> Sketch126 [N_Axis]
  Type = 4
FEATURE [PartDesign::SubShapeBinder] Binder013
  BindCopyOnChange = 0
  BindMode = 0
  ClaimChildren = false
  Context = -> Part014 [Body044.Binder013.]
  Fuse = false
  MakeFace = true
  OffsetFill = false
  OffsetIntersection = false
  OffsetJoinType = 0
  OffsetOpenResult = false
  PartialLoad = false
  Relative = true
  Support = -> [Body[Pocket055.Sketch126.]]
  _Version = 2
FEATURE [PartDesign::Pocket] Pocket094
  BaseFeature = -> Pad070
  Direction = (0,0,-1)
  Length = 5
  Length2 = 5
  Profile = -> Binder013
  Type = 1
FEATURE [PartDesign::PolarPattern] PolarPattern021
  Angle = 70
  Axis = -> Sketch001 [N_Axis]
  BaseFeature = -> Pocket055
  Occurrences = 2
  Originals = -> [Pocket]
  Reversed = true
FEATURE [PartDesign::PolarPattern] PolarPattern022
  Angle = 360
  Axis = -> Sketch001 [N_Axis]
  BaseFeature = -> PolarPattern021
  Occurrences = 2
  Originals = -> [Pocket]
FEATURE [PartDesign::SubShapeBinder] Binder027
  BindCopyOnChange = 0
  BindMode = 0
  ClaimChildren = false
  Context = -> Part014 [Body044.Binder027.]
  Fuse = false
  MakeFace = true
  OffsetFill = false
  OffsetIntersection = false
  OffsetJoinType = 0
  OffsetOpenResult = false
  PartialLoad = false
  Relative = true
  Support = -> [Body[Pocket.Sketch001.]]
  _Version = 2
FEATURE [PartDesign::Pocket] Pocket096
  BaseFeature = -> Pocket094
  Direction = (0,0,-1)
  Length = 5
  Length2 = 5
  Profile = -> Binder027
  Type = 1
FEATURE [PartDesign::PolarPattern] PolarPattern023
  Angle = 110
  Axis = -> Z_Axis248
  BaseFeature = -> Pocket096
  Occurrences = 2
  Originals = -> [Pocket096]
FEATURE [PartDesign::PolarPattern] PolarPattern024
  Angle = 70
  Axis = -> Z_Axis248
  BaseFeature = -> PolarPattern023
  Occurrences = 2
  Originals = -> [Pocket096]
  Reversed = true
FEATURE [PartDesign::PolarPattern] PolarPattern025
  Angle = 180
  Axis = -> Z_Axis248
  BaseFeature = -> PolarPattern024
  Occurrences = 2
  Originals = -> [Pocket096]
FEATURE [PartDesign::SubShapeBinder] Binder028
  BindCopyOnChange = 0
  BindMode = 0
  ClaimChildren = false
  Context = -> Part014 [Body044.Binder028.]
  Fuse = false
  MakeFace = true
  OffsetFill = false
  OffsetIntersection = false
  OffsetJoinType = 0
  OffsetOpenResult = false
  PartialLoad = false
  Relative = true
  Support = -> [Body[Pocket004.Sketch015.]]
  _Version = 2
FEATURE [PartDesign::Pocket] Pocket097
  BaseFeature = -> PolarPattern025
  Direction = (0,0,-1)
  Length = 5
  Length2 = 5
  Profile = -> Binder028
  Type = 1
FEATURE [Sketcher::SketchObject] Sketch127
  FullyConstrained = true
  MapMode = 5
  Placement = pos=(0,0,0) rot=(1,0,0;1.5708rad)
  Support = -> [XZ_Plane256]
  sketch-geometry (8):
    g0: LineSegment StartX=-88 StartY=-1 StartZ=0 EndX=-79 EndY=-1 EndZ=0
    g1: LineSegment StartX=-79 StartY=-34 StartZ=0 EndX=-88 EndY=-34 EndZ=0
    g2: LineSegment StartX=-88 StartY=-34 StartZ=0 EndX=-88 EndY=-1 EndZ=0
    g3: LineSegment StartX=-79 StartY=-1 StartZ=0 EndX=-79 EndY=-3 EndZ=0
    g4: LineSegment StartX=-79 StartY=-3 StartZ=0 EndX=-86 EndY=-3 EndZ=0
    g5: LineSegment StartX=-86 StartY=-3 StartZ=0 EndX=-86 EndY=-32 EndZ=0
    g6: LineSegment StartX=-86 StartY=-32 StartZ=0 EndX=-79 EndY=-32 EndZ=0
    g7: LineSegment StartX=-79 StartY=-32 StartZ=0 EndX=-79 EndY=-34 EndZ=0
  constraints (24):
    c: Coincident(g1,g2)
    c: Coincident(g2,g0)
    c: Horizontal(g0)
    c: Horizontal(g1)
    c: Vertical(g2)
    c: DistanceY(g1,g0) = 33
    c: DistanceX(g1,g1) = 9
    c: DistanceX(g0,g-1) = 88
    c: DistanceY(g1,g-1) = 34
    c: Equal(g1,g0)
    c: Coincident(g3,g0)
    c: Vertical(g3)
    c: Coincident(g4,g3)
    c: Horizontal(g4)
    c: Coincident(g5,g4)
    c: Vertical(g5)
    c: Coincident(g6,g5)
    c: Horizontal(g6)
    c: Coincident(g7,g6)
    c: Coincident(g7,g1)
    c: Vertical(g7)
    c: Equal(g3,g7)
    c: DistanceY(g3,g3) = 2
    c: DistanceX(g0,g4) = 2
FEATURE [PartDesign::Revolution] Revolution002
  Angle = 70
  Axis = (1e-16,1e-16,1)
  Base = (0,0,0)
  Midplane = true
  Placement = pos=(0,0,0) rot=(1,0,0;1.5708rad)
  Profile = -> Sketch127
  ReferenceAxis = -> Z_Axis256
  Reversed = true
FEATURE [Sketcher::SketchObject] Sketch128
  FullyConstrained = true
  MapMode = 5
  Placement = pos=(0,0,0) rot=(1,0,0;1.5708rad)
  Support = -> [XZ_Plane257]
  sketch-geometry (8):
    g0: LineSegment StartX=-88 StartY=-1 StartZ=0 EndX=-79 EndY=-1 EndZ=0
    g1: LineSegment StartX=-79 StartY=-34 StartZ=0 EndX=-88 EndY=-34 EndZ=0
    g2: LineSegment StartX=-88 StartY=-34 StartZ=0 EndX=-88 EndY=-1 EndZ=0
    g3: LineSegment StartX=-79 StartY=-1 StartZ=0 EndX=-79 EndY=-3 EndZ=0
    g4: LineSegment StartX=-79 StartY=-3 StartZ=0 EndX=-86 EndY=-3 EndZ=0
    g5: LineSegment StartX=-86 StartY=-3 StartZ=0 EndX=-86 EndY=-32 EndZ=0
    g6: LineSegment StartX=-86 StartY=-32 StartZ=0 EndX=-79 EndY=-32 EndZ=0
    g7: LineSegment StartX=-79 StartY=-32 StartZ=0 EndX=-79 EndY=-34 EndZ=0
  constraints (24):
    c: Coincident(g1,g2)
    c: Coincident(g2,g0)
    c: Horizontal(g0)
    c: Horizontal(g1)
    c: Vertical(g2)
    c: DistanceY(g1,g0) = 33
    c: DistanceX(g1,g1) = 9
    c: DistanceX(g0,g-1) = 88
    c: DistanceY(g1,g-1) = 34
    c: Equal(g1,g0)
    c: Coincident(g3,g0)
    c: Vertical(g3)
    c: Coincident(g4,g3)
    c: Horizontal(g4)
    c: Coincident(g5,g4)
    c: Vertical(g5)
    c: Coincident(g6,g5)
    c: Horizontal(g6)
    c: Coincident(g7,g6)
    c: Coincident(g7,g1)
    c: Vertical(g7)
    c: Equal(g3,g7)
    c: DistanceY(g3,g3) = 2
    c: DistanceX(g0,g4) = 2
FEATURE [PartDesign::Revolution] Revolution003
  Angle = 30
  Axis = (1e-16,1e-16,1)
  Base = (0,0,0)
  Midplane = true
  Placement = pos=(0,0,0) rot=(1,0,0;1.5708rad)
  Profile = -> Sketch128
  ReferenceAxis = -> Z_Axis257
  Reversed = true
FEATURE [Part::Feature] Part__Feature1464  label="LD19_BASE"
  Placement = pos=(-9e-15,-8.62399,0) rot=(0,0,1;0rad)
  shape: bbox 53.95 x 46.29 x 3.551 mm, 34 faces (baked)
FEATURE [Part::Feature] Part__Feature1465  label="LD19_EMITTER"
  Placement = pos=(5.47382e-06,-8.59716,0) rot=(0,0,1;0rad)
  shape: bbox 39.74 x 39.74 x 11.25 mm, 29 faces (baked)
FEATURE [Part::Feature] Part__Feature1466  label="LD19_BODY"
  Placement = pos=(5.47382e-06,-8.59716,-2e-15) rot=(0,0,1;0rad)
  shape: bbox 38.52 x 38.52 x 18.7 mm, 15 faces (baked)
FEATURE [PartDesign::SubShapeBinder] Binder032
  BindCopyOnChange = 0
  BindMode = 0
  ClaimChildren = false
  Context = -> Body [Binder032.]
  Fuse = false
  MakeFace = true
  OffsetFill = false
  OffsetIntersection = false
  OffsetJoinType = 0
  OffsetOpenResult = false
  PartialLoad = false
  Relative = true
  Support = -> [LD19[Part__Feature1464.Edge77,Part__Feature1464.Edge78,Part__Feature1464.Edge73,Part__Feature1464.Edge74,Part__Feature1464.Edge75,Part__Feature1464.Edge76]]
  _Version = 2
FEATURE [PartDesign::Pocket] Pocket101
  BaseFeature = -> PolarPattern022
  Direction = (0,0,-1)
  Length = 5
  Length2 = 5
  Profile = -> Binder032
  Type = 1
FEATURE [Sketcher::SketchObject] Sketch130
  FullyConstrained = false
  MapMode = 5
  Support = -> [XY_Plane049]
  sketch-geometry (6):
    g0: ArcOfCircle CenterX=0 CenterY=0 CenterZ=0 NormalX=0 NormalY=0 NormalZ=1 AngleXU=0 Radius=77.5 StartAngle=4.97117 EndAngle=7.5952
    g1: LineSegment StartX=19.8431 StartY=-22.5 StartZ=0 EndX=19.8431 EndY=22.5 EndZ=0
    g2: ArcOfCircle CenterX=0 CenterY=0 CenterZ=0 NormalX=0 NormalY=0 NormalZ=1 AngleXU=0 Radius=30 StartAngle=5.43464 EndAngle=5.43512
    g3: ArcOfCircle CenterX=0 CenterY=0 CenterZ=0 NormalX=0 NormalY=0 NormalZ=1 AngleXU=0 Radius=30 StartAngle=0.848062 EndAngle=0.848549
    g4: LineSegment StartX=19.8322 StartY=-74.9195 StartZ=0 EndX=19.8322 EndY=-22.5097 EndZ=0
    g5: LineSegment StartX=19.8322 StartY=22.5097 StartZ=0 EndX=19.8322 EndY=74.9195 EndZ=0
  constraints (16):
    c: Coincident(g0,g-1)
    c: Symmetric(g1,g1,g-1)
    c: Diameter(g0) = 155
    c: DistanceY(g1,g1) = 45
    c: Coincident(g2,g0)
    c: Coincident(g2,g1)
    c: Coincident(g3,g0)
    c: Coincident(g3,g1)
    c: Diameter(g3) = 60
    c: Coincident(g4,g0)
    c: Coincident(g4,g2)
    c: Coincident(g5,g3)
    c: Coincident(g5,g0)
    c: Vertical(g0,g0)
    c: Vertical(g2,g3)
    c: Vertical(g4)
FEATURE [PartDesign::Pad] Pad088
  Direction = (0,0,1)
  Length = 2
  Length2 = 10
  Profile = -> Sketch130
  ReferenceAxis = -> Sketch130 [N_Axis]
  Type = 0
FEATURE [Sketcher::SketchObject] Sketch131
  FullyConstrained = true
  MapMode = 5
  Placement = pos=(0,0,0) rot=(1,0,0;1.5708rad)
  Support = -> [XZ_Plane259]
  sketch-geometry (4):
    g0: LineSegment StartX=-22 StartY=15 StartZ=0 EndX=22 EndY=15 EndZ=0
    g1: LineSegment StartX=22 StartY=15 StartZ=0 EndX=22 EndY=-15 EndZ=0
    g2: LineSegment StartX=22 StartY=-15 StartZ=0 EndX=-22 EndY=-15 EndZ=0
    g3: LineSegment StartX=-22 StartY=-15 StartZ=0 EndX=-22 EndY=15 EndZ=0
  constraints (10):
    c: Coincident(g0,g1)
    c: Coincident(g1,g2)
    c: Coincident(g2,g3)
    c: Coincident(g3,g0)
    c: Horizontal(g2)
    c: Vertical(g3)
    c: DistanceY(g1,g1) = 30
    c: Symmetric(g1,g0,g-1)
    c: Symmetric(g0,g0,g-2)
    c: DistanceX(g0,g0) = 44
FEATURE [PartDesign::SubShapeBinder] Binder034
  BindCopyOnChange = 0
  BindMode = 0
  ClaimChildren = false
  Context = -> Body [Binder034.]
  Fuse = false
  MakeFace = true
  OffsetFill = false
  OffsetIntersection = false
  OffsetJoinType = 0
  OffsetOpenResult = false
  PartialLoad = false
  Relative = true
  Support = -> [Part004[Body053.Pad089.Sketch131.]]
  _Version = 2
FEATURE [PartDesign::Pocket] Pocket103
  BaseFeature = -> Pocket101
  Direction = (-6e-16,-1e-15,-1)
  Length = 5
  Length2 = 5
  Profile = -> Binder034
  Reversed = true
  Type = 1
FEATURE [PartDesign::SubShapeBinder] Binder035
  BindCopyOnChange = 0
  BindMode = 0
  ClaimChildren = false
  Context = -> Part [Body024.Binder035.]
  Fuse = false
  MakeFace = true
  OffsetFill = false
  OffsetIntersection = false
  OffsetJoinType = 0
  OffsetOpenResult = false
  PartialLoad = false
  Relative = true
  Support = -> [Part004[Body053.Pad089.Sketch131.]]
  _Version = 2
FEATURE [PartDesign::Pocket] Pocket104
  BaseFeature = -> Pad088
  Direction = (2e-16,-1.1e-15,-1)
  Length = 5
  Length2 = 5
  Profile = -> Binder035
  Reversed = true
  Type = 1
FEATURE [PartDesign::Body] Body024  label="PCB board"
  Group = -> [Sketch130,Pad088,Binder035,Pocket104]
  Origin = -> Origin049
  Placement = pos=(0,0,16) rot=(0,0,1;0rad)
  Tip = -> Pocket104
FEATURE [Sketcher::SketchObject] Sketch133
  FullyConstrained = true
  MapMode = 5
  Placement = pos=(0,0,0) rot=(1,0,0;1.5708rad)
  Support = -> [XZ_Plane259]
  sketch-geometry (4):
    g0: LineSegment StartX=-21.5 StartY=14.5 StartZ=0 EndX=21.5 EndY=14.5 EndZ=0
    g1: LineSegment StartX=21.5 StartY=14.5 StartZ=0 EndX=21.5 EndY=-14.5 EndZ=0
    g2: LineSegment StartX=21.5 StartY=-14.5 StartZ=0 EndX=-21.5 EndY=-14.5 EndZ=0
    g3: LineSegment StartX=-21.5 StartY=-14.5 StartZ=0 EndX=-21.5 EndY=14.5 EndZ=0
  constraints (10):
    c: Coincident(g0,g1)
    c: Coincident(g1,g2)
    c: Coincident(g2,g3)
    c: Coincident(g3,g0)
    c: Horizontal(g2)
    c: Vertical(g1)
    c: Symmetric(g0,g0,g-2)
    c: Symmetric(g2,g0,g-1)
    c: DistanceX(g0,g0) = 43
    c: DistanceY(g1,g1) = 29
FEATURE [PartDesign::Pad] Pad089
  Direction = (0,-1,-2e-16)
  Length = 60
  Length2 = 10
  Placement = pos=(0,0,0) rot=(1,0,0;1.5708rad)
  Profile = -> Sketch133
  ReferenceAxis = -> Sketch133 [N_Axis]
  Type = 0
FEATURE [PartDesign::Fillet] Fillet
  Base = -> Pad089 [Edge7,Edge4,Edge10,Edge12,Edge2,Edge5,Edge1,Edge8,Edge3,Edge11,Edge9,Edge6]
  BaseFeature = -> Pad089
  Placement = pos=(0,0,0) rot=(1,0,0;1.5708rad)
  Radius = 2
  SupportTransform = false
  UseAllEdges = false
FEATURE [PartDesign::Body] Body053  label="Batterie test"
  Group = -> [Sketch131,Sketch133,Pad089,Fillet]
  Origin = -> Origin259
  Placement = pos=(64,-2.9e-14,-36.5) rot=(0.57735,-0.57735,0.57735;4.18879rad)
  Tip = -> Fillet
FEATURE [App::Part] Part004  label="Powerpack"
  Group = -> [Body013,Body014,Body053]
  Origin = -> Origin037
  Placement = pos=(0,0,3) rot=(0,0,1;0rad)
FEATURE [Sketcher::SketchObject] Sketch137
  ExternalGeometry = -> [Pad084]
  FullyConstrained = true
  MapMode = 5
  Placement = pos=(0,0,26) rot=(0,0,1;0rad)
  Support = -> [Pad084]
  sketch-geometry (3):
    g0: Circle CenterX=-56 CenterY=4 CenterZ=0 NormalX=0 NormalY=0 NormalZ=1 AngleXU=0 Radius=1.5
    g1: Circle CenterX=-56 CenterY=-4 CenterZ=0 NormalX=0 NormalY=0 NormalZ=1 AngleXU=0 Radius=1.5
    g2: LineSegment StartX=-56 StartY=4 StartZ=0 EndX=-64 EndY=10 EndZ=0
  constraints (7):
    c: Diameter(g0) = 3
    c: Diameter(g1) = 3
    c: Symmetric(g1,g0,g-1)
    c: Coincident(g2,g0)
    c: Coincident(g2,g-3)
    c: DistanceX(g2,g0) = 8
    c: DistanceY(g0,g2) = 6
FEATURE [PartDesign::Pocket] Pocket108
  BaseFeature = -> Pad084
  Direction = (0,0,-1)
  Length = 5
  Length2 = 5
  Profile = -> Sketch137
  ReferenceAxis = -> Sketch137 [N_Axis]
  Type = 1
FEATURE [PartDesign::Body] Body049  label="Kicker OTS"
  Group = -> [Sketch119,Pad083,Sketch120,Pad084,Sketch137,Pocket108]
  Origin = -> Origin254
  Placement = pos=(-1,0,-15) rot=(0,0,1;0rad)
  Tip = -> Pocket108
FEATURE [PartDesign::SubShapeBinder] Binder038
  BindCopyOnChange = 0
  BindMode = 0
  ClaimChildren = false
  Context = -> Body [Binder038.]
  Fuse = false
  MakeFace = true
  OffsetFill = false
  OffsetIntersection = false
  OffsetJoinType = 0
  OffsetOpenResult = false
  PartialLoad = false
  Relative = true
  Support = -> [Part013[Body049.Pocket108.Sketch137.]]
  _Version = 2
FEATURE [PartDesign::Pocket] Pocket109
  BaseFeature = -> Pocket103
  Direction = (0,0,-1)
  Length = 5
  Length2 = 5
  Profile = -> Binder038
  Reversed = true
  Type = 1
FEATURE [Sketcher::SketchObject] Sketch138
  ExternalGeometry = -> [Pocket097]
  FullyConstrained = true
  MapMode = 5
  Placement = pos=(0,0,0) rot=(1,0,0;3.14159rad)
  Support = -> [Pocket097]
  sketch-geometry (3):
    g0: LineSegment StartX=7.63834 StartY=75.3298 StartZ=0 EndX=17.2106 EndY=49.0304 EndZ=0
    g1: LineSegment StartX=17.2106 StartY=49.0304 StartZ=0 EndX=49.0304 EndY=17.2106 EndZ=0
    g2: LineSegment StartX=49.0304 StartY=17.2106 StartZ=0 EndX=75.3298 EndY=7.63834 EndZ=0
  constraints (8):
    c: Coincident(g0,g-3)
    c: Coincident(g1,g0)
    c: Coincident(g2,g1)
    c: Coincident(g2,g-4)
    c: Distance(g1) = 45
    c: Equal(g0,g2)
    c: Angle(g0,g-3) = 2.18166
    c: Angle(g-4,g2) = 2.18166
FEATURE [Sketcher::SketchObject] Sketch193
  FullyConstrained = false
  MapMode = 5
  Placement = pos=(0,0,0) rot=(1,0,0;3.14159rad)
  sketch-geometry (6):
    g0: LineSegment StartX=7.63834 StartY=75.3298 StartZ=0 EndX=17.2106 EndY=49.0304 EndZ=0
    g1: LineSegment StartX=17.2106 StartY=49.0304 StartZ=0 EndX=49.0304 EndY=17.2106 EndZ=0
    g2: LineSegment StartX=49.0304 StartY=17.2106 StartZ=0 EndX=75.3298 EndY=7.63834 EndZ=0
    g3: LineSegment StartX=7.63834 StartY=75.3298 StartZ=0 EndX=13.6383 EndY=83.8987 EndZ=0
    g4: LineSegment StartX=75.3298 StartY=7.63834 StartZ=0 EndX=83.8987 EndY=13.6383 EndZ=0
    g5: ArcOfCircle CenterX=0 CenterY=0 CenterZ=0 NormalX=0 NormalY=0 NormalZ=1 AngleXU=0 Radius=85 StartAngle=0.161148 EndAngle=1.40965
  constraints (8):
    c: Coincident(g1,g0)
    c: Coincident(g2,g1)
    c: Distance(g1) = 45
    c: Equal(g0,g2)
    c: Coincident(g3,g0)
    c: Coincident(g4,g2)
    c: Coincident(g5,g-1)
    c: Coincident(g5,g3)
FEATURE [PartDesign::Pad] Pad091
  Direction = (0,0,-1)
  Length = 3
  Length2 = 10
  Placement = pos=(0,0,0) rot=(1,0,0;3.14159rad)
  Profile = -> Sketch193
  ReferenceAxis = -> Sketch193 [N_Axis]
  Type = 0
FEATURE [Sketcher::SketchObject] Sketch248
  FullyConstrained = false
  MapMode = 5
  Placement = pos=(0,0,0) rot=(1,0,0;3.14159rad)
  sketch-geometry (20):
    g0: LineSegment StartX=7.63834 StartY=75.3298 StartZ=0 EndX=17.2106 EndY=49.0304 EndZ=0
    g1: LineSegment StartX=17.2106 StartY=49.0304 StartZ=0 EndX=49.0304 EndY=17.2106 EndZ=0
    g2: LineSegment StartX=49.0304 StartY=17.2106 StartZ=0 EndX=75.3298 EndY=7.63834 EndZ=0
    g3: LineSegment StartX=7.63834 StartY=75.3298 StartZ=0 EndX=-32.942 EndY=68.1744 EndZ=0
    g4: LineSegment StartX=-32.942 StartY=68.1744 StartZ=0 EndX=-41.5109 EndY=74.1744 EndZ=0
    g5: LineSegment StartX=-74.1744 StartY=41.5109 StartZ=0 EndX=-68.1744 EndY=32.942 EndZ=0
    g6: LineSegment StartX=-68.1744 StartY=32.942 StartZ=0 EndX=-75.1847 EndY=-6.81529 EndZ=0
    g7: LineSegment StartX=-6.81529 StartY=-75.1847 StartZ=0 EndX=32.942 EndY=-68.1744 EndZ=0
    g8: LineSegment StartX=32.942 StartY=-68.1744 StartZ=0 EndX=41.5109 EndY=-74.1744 EndZ=0
    g9: LineSegment StartX=74.1744 StartY=-41.5109 StartZ=0 EndX=68.1744 EndY=-32.942 EndZ=0
    g10: LineSegment StartX=68.1744 StartY=-32.942 StartZ=0 EndX=75.3298 EndY=7.63834 EndZ=0
    g11: ArcOfCircle CenterX=0 CenterY=0 CenterZ=0 NormalX=0 NormalY=0 NormalZ=1 AngleXU=0 Radius=85 StartAngle=2.08101 EndAngle=2.63138
    g12: ArcOfCircle CenterX=0 CenterY=0 CenterZ=0 NormalX=0 NormalY=0 NormalZ=1 AngleXU=0 Radius=85 StartAngle=5.2226 EndAngle=5.77297
    g13: LineSegment StartX=-75.1847 StartY=-6.81529 StartZ=0 EndX=-85.7913 EndY=-17.4219 EndZ=0
    g14: LineSegment StartX=-85.7913 StartY=-17.4219 StartZ=0 EndX=-75.1847 EndY=-28.0285 EndZ=0
    g15: LineSegment StartX=-75.1847 StartY=-28.0285 StartZ=0 EndX=-64.5781 EndY=-17.4219 EndZ=0
    g16: LineSegment StartX=-64.5781 StartY=-17.4219 StartZ=0 EndX=-17.4219 EndY=-64.5781 EndZ=0
    g17: LineSegment StartX=-17.4219 StartY=-64.5781 StartZ=0 EndX=-28.0285 EndY=-75.1847 EndZ=0
    g18: LineSegment StartX=-28.0285 StartY=-75.1847 StartZ=0 EndX=-17.4219 EndY=-85.7913 EndZ=0
    g19: LineSegment StartX=-17.4219 StartY=-85.7913 StartZ=0 EndX=-6.81529 EndY=-75.1847 EndZ=0
  constraints (38):
    c: Coincident(g1,g0)
    c: Coincident(g2,g1)
    c: Distance(g1) = 45
    c: Equal(g0,g2)
    c: Coincident(g3,g0)
    c: Coincident(g4,g3)
    c: Coincident(g6,g5)
    c: Coincident(g8,g7)
    c: Coincident(g10,g9)
    c: Coincident(g10,g2)
    c: Coincident(g11,g4)
    c: Coincident(g12,g11)
    c: Coincident(g12,g8)
    c: Coincident(g12,g9)
    c: DistanceX(g6) = -75.1847
    c: DistanceY(g6) = -6.81529
    c: DistanceX(g7) = -6.81529
    c: DistanceY(g7) = -75.1847
    c: Coincident(g13,g6)
    c: Coincident(g14,g13)
    c: Coincident(g15,g14)
    c: Coincident(g16,g15)
    c: Coincident(g17,g16)
    c: Coincident(g18,g17)
    c: Coincident(g19,g18)
    c: Coincident(g19,g7)
    c: Parallel(g13,g15)
    c: Parallel(g17,g19)
    c: Parallel(g16,g14)
    c: Parallel(g16,g18)
    c: Perpendicular(g17,g18)
    c: Perpendicular(g15,g14)
    c: Equal(g15,g17)
    c: Equal(g18,g14)
    c: Equal(g13,g15)
    c: Equal(g17,g19)
    c: Distance(g14) = 15
    c: Distance(g15) = 15
FEATURE [PartDesign::Pad] Pad092
  Direction = (0,0,-1)
  Length = 3
  Length2 = 10
  Placement = pos=(0,0,0) rot=(1,0,0;3.14159rad)
  Profile = -> Sketch248
  ReferenceAxis = -> Sketch248 [N_Axis]
  Type = 0
FEATURE [PartDesign::SubShapeBinder] Binder039
  BindCopyOnChange = 0
  BindMode = 0
  ClaimChildren = false
  Context = -> Part014 [Body093.Binder039.]
  Fuse = false
  MakeFace = true
  OffsetFill = false
  OffsetIntersection = false
  OffsetJoinType = 0
  OffsetOpenResult = false
  PartialLoad = false
  Relative = true
  Support = -> [Body[Pocket055.Sketch126.]]
  _Version = 2
FEATURE [PartDesign::Pocket] Pocket110
  BaseFeature = -> Pad092
  Direction = (0,0,-1)
  Length = 5
  Length2 = 5
  Placement = pos=(0,0,0) rot=(1,0,0;3.14159rad)
  Profile = -> Binder039
  Type = 1
FEATURE [PartDesign::SubShapeBinder] Binder040
  BindCopyOnChange = 0
  BindMode = 0
  ClaimChildren = false
  Context = -> Part014 [Body073.Binder040.]
  Fuse = false
  MakeFace = true
  OffsetFill = false
  OffsetIntersection = false
  OffsetJoinType = 0
  OffsetOpenResult = false
  PartialLoad = false
  Relative = true
  Support = -> [Body[Pocket055.Sketch126.]]
  _Version = 2
FEATURE [PartDesign::Pocket] Pocket111
  BaseFeature = -> Pad091
  Direction = (0,0,-1)
  Length = 5
  Length2 = 5
  Placement = pos=(0,0,0) rot=(1,0,0;3.14159rad)
  Profile = -> Binder040
  Type = 1
FEATURE [PartDesign::Body] Body073  label="Lower plate small"
  Group = -> [Sketch193,Pad091,Binder040,Pocket111]
  Origin = -> Origin300
  Placement = pos=(0,0,-34.2) rot=(0,0,1;0.785398rad)
  Tip = -> Pocket111
FEATURE [Sketcher::SketchObject] Sketch249
  ExternalGeometry = -> [Pocket052]
  FullyConstrained = false
  MapMode = 5
  Placement = pos=(0,0,-6) rot=(1,0,0;3.14159rad)
  Support = -> [Pocket052]
  sketch-geometry (18):
    g0: LineSegment StartX=-61.4103 StartY=-33.3313 StartZ=0 EndX=-64.3168 EndY=-34.0745 EndZ=0
    g1: LineSegment StartX=-64.3168 StartY=-34.0745 StartZ=0 EndX=-65.1265 EndY=-36.9631 EndZ=0
    g2: LineSegment StartX=-65.1265 StartY=-36.9631 StartZ=0 EndX=-63.0297 EndY=-39.1087 EndZ=0
    g3: LineSegment StartX=-63.0297 StartY=-39.1087 StartZ=0 EndX=-60.1232 EndY=-38.3655 EndZ=0
    g4: LineSegment StartX=-60.1232 StartY=-38.3655 StartZ=0 EndX=-59.3135 EndY=-35.4769 EndZ=0
    g5: LineSegment StartX=-59.3135 StartY=-35.4769 StartZ=0 EndX=-61.4103 EndY=-33.3313 EndZ=0
    g6: Circle CenterX=-62.22 CenterY=-36.22 CenterZ=0 NormalX=0 NormalY=0 NormalZ=1 AngleXU=0 Radius=3
    g7: LineSegment StartX=-62.22 StartY=-36.22 StartZ=0 EndX=-66.22 EndY=-40.22 EndZ=0
    g8: LineSegment StartX=-62.22 StartY=-36.22 StartZ=0 EndX=-66.22 EndY=-32.22 EndZ=0
    g9: LineSegment StartX=95.3648 StartY=-34.4404 StartZ=0 EndX=95.0313 EndY=-37.4218 EndZ=0
    g10: LineSegment StartX=95.0313 StartY=-37.4218 StartZ=0 EndX=97.4464 EndY=-39.2014 EndZ=0
    g11: LineSegment StartX=97.4464 StartY=-39.2014 StartZ=0 EndX=100.195 EndY=-37.9996 EndZ=0
    g12: LineSegment StartX=100.195 StartY=-37.9996 StartZ=0 EndX=100.529 EndY=-35.0182 EndZ=0
    g13: LineSegment StartX=100.529 StartY=-35.0182 StartZ=0 EndX=98.1136 EndY=-33.2386 EndZ=0
    g14: LineSegment StartX=98.1136 StartY=-33.2386 StartZ=0 EndX=95.3648 EndY=-34.4404 EndZ=0
    g15: Circle CenterX=97.78 CenterY=-36.22 CenterZ=0 NormalX=0 NormalY=0 NormalZ=1 AngleXU=0 Radius=3
    g16: LineSegment StartX=101.78 StartY=-32.22 StartZ=0 EndX=97.78 EndY=-36.22 EndZ=0
    g17: LineSegment StartX=97.78 StartY=-36.22 StartZ=0 EndX=101.78 EndY=-40.22 EndZ=0
  constraints (40):
    c: Coincident(g0,g1)
    c: Coincident(g1,g2)
    c: Coincident(g2,g3)
    c: Coincident(g3,g4)
    c: Coincident(g4,g5)
    c: Coincident(g5,g0)
    c: Equal(g0, g1-g5) x5
    c: PointOnObject(g0,g6)
    c: PointOnObject(g1,g6)
    c: PointOnObject(g2,g6)
    c: PointOnObject(g3,g6)
    c: PointOnObject(g4,g6)
    c: PointOnObject(g5,g6)
    c: Diameter(g6) = 6
    c: Coincident(g7,g6)
    c: Coincident(g7,g-3)
    c: Coincident(g8,g6)
    c: Coincident(g8,g-3)
    c: Equal(g8,g7)
    c: Coincident(g9,g10)
    c: Coincident(g10,g11)
    c: Coincident(g11,g12)
    c: Coincident(g12,g13)
    c: Coincident(g13,g14)
    c: Coincident(g14,g9)
    c: Equal(g9, g10-g14) x5
    c: PointOnObject(g9,g15)
    c: PointOnObject(g10,g15)
    c: PointOnObject(g11,g15)
    c: PointOnObject(g12,g15)
    c: PointOnObject(g13,g15)
    c: PointOnObject(g14,g15)
    c: Diameter(g15) = 6
    c: Coincident(g16,g-4)
    c: Coincident(g16,g15)
    c: Coincident(g17,g15)
    c: Coincident(g17,g-4)
    c: Equal(g16,g17)
    c: Perpendicular(g8,g7)
    c: Perpendicular(g16,g17)
FEATURE [PartDesign::Pad] Pad093
  BaseFeature = -> Pocket052
  Direction = (0,0,-1)
  Length = 50
  Length2 = 10
  Profile = -> Sketch249
  ReferenceAxis = -> Sketch249 [N_Axis]
  Type = 0
FEATURE [Sketcher::SketchObject] Sketch250
  ExternalGeometry = -> [Pad093]
  FullyConstrained = true
  MapMode = 5
  Support = -> [Pad093]
  sketch-geometry (6):
    g0: Circle CenterX=-62.22 CenterY=36.22 CenterZ=0 NormalX=0 NormalY=0 NormalZ=1 AngleXU=0 Radius=1
    g1: LineSegment StartX=-66.22 StartY=32.22 StartZ=0 EndX=-62.22 EndY=36.22 EndZ=0
    g2: LineSegment StartX=-62.22 StartY=36.22 StartZ=0 EndX=-66.22 EndY=40.22 EndZ=0
    g3: Circle CenterX=97.78 CenterY=36.22 CenterZ=0 NormalX=0 NormalY=0 NormalZ=1 AngleXU=0 Radius=1
    g4: LineSegment StartX=101.78 StartY=32.22 StartZ=0 EndX=97.78 EndY=36.22 EndZ=0
    g5: LineSegment StartX=97.78 StartY=36.22 StartZ=0 EndX=101.78 EndY=40.22 EndZ=0
  constraints (14):
    c: Diameter(g0) = 2
    c: Coincident(g1,g-3)
    c: Coincident(g1,g0)
    c: Coincident(g2,g-3)
    c: Coincident(g2,g0)
    c: Equal(g1,g2)
    c: Diameter(g3) = 2
    c: Coincident(g4,g-4)
    c: Coincident(g4,g3)
    c: Coincident(g5,g3)
    c: Coincident(g5,g-4)
    c: Equal(g4,g5)
    c: Perpendicular(g2,g1)
    c: Perpendicular(g5,g4)
FEATURE [PartDesign::Pocket] Pocket112
  BaseFeature = -> Pad093
  Direction = (0,0,-1)
  Length = 5
  Length2 = 5
  Profile = -> Sketch250
  ReferenceAxis = -> Sketch250 [N_Axis]
  Type = 1
FEATURE [PartDesign::SubShapeBinder] Binder044
  BindCopyOnChange = 0
  BindMode = 0
  ClaimChildren = false
  Context = -> Part014 [Body093.Binder044.]
  Fuse = false
  MakeFace = true
  OffsetFill = false
  OffsetIntersection = false
  OffsetJoinType = 0
  OffsetOpenResult = false
  PartialLoad = false
  Relative = true
  Support = -> [openmv4_h7[Body025.Pocket112.Sketch250.]]
  _Version = 2
FEATURE [PartDesign::Pocket] Pocket116
  BaseFeature = -> Pocket110
  Direction = (0,0,-1)
  Length = 5
  Length2 = 5
  Placement = pos=(0,0,0) rot=(1,0,0;3.14159rad)
  Profile = -> Binder044
  Type = 1
FEATURE [PartDesign::Body] Body093  label="Lower plate large"
  Group = -> [Sketch248,Pad092,Binder039,Pocket110,Binder044,Pocket116]
  Origin = -> Origin340
  Placement = pos=(0,0,-34.2) rot=(0,0,1;0.785398rad)
  Tip = -> Pocket116
FEATURE [PartDesign::SubShapeBinder] Binder045
  BindCopyOnChange = 0
  BindMode = 0
  ClaimChildren = false
  Context = -> Part014 [Body044.Binder045.]
  Fuse = false
  MakeFace = true
  OffsetFill = false
  OffsetIntersection = false
  OffsetJoinType = 0
  OffsetOpenResult = false
  PartialLoad = false
  Relative = true
  Support = -> [openmv4_h7[Body025.Pocket112.Sketch250.]]
  _Version = 2
FEATURE [PartDesign::Pocket] Pocket117
  BaseFeature = -> Pocket097
  Direction = (0,0,-1)
  Length = 5
  Length2 = 5
  Profile = -> Binder045
  Type = 1
FEATURE [PartDesign::Body] Body044  label="Lower plate full"
  Group = -> [Sketch102,Pad070,Binder013,Pocket094,Binder027,Pocket096,PolarPattern023,PolarPattern024,PolarPattern025,Binder028,Pocket097,Sketch138,Binder045,Pocket117]
  Origin = -> Origin248
  Placement = pos=(0,0,-37.2) rot=(0,0,1;0.785398rad)
  Tip = -> Pocket117
FEATURE [App::Part] Part014  label="Lower plate"
  Group = -> [Body044,Body073,Body093]
  Origin = -> Origin260
FEATURE [Part::Feature] Part__Feature1467  label="rt10"
  shape: bbox 14 x 14 x 16.7 mm, 16 faces (baked)
FEATURE [Part::Feature] Part__Feature1468  label="rt011"
  shape: bbox 5 x 5 x 0.7243 mm, 72 faces (baked)
FEATURE [Part::Feature] Part__Feature1469  label="rt012"
  shape: bbox 12.1 x 4.6 x 2.3 mm, 1904 faces (baked)
FEATURE [Part::Feature] Part__Feature1470  label="rt013"
  shape: bbox 35.56 x 16.51 x 1.6 mm, 134 faces (baked)
FEATURE [Part::Feature] Part__Feature1471  label="rt014"
  shape: bbox 4.35 x 4.35 x 4.4 mm, 6 faces (baked)
FEATURE [Part::Feature] Part__Feature1472  label="rt015"
  shape: bbox 4.35 x 4.35 x 4.4 mm, 6 faces (baked)
FEATURE [Part::Feature] Part__Feature1473  label="rt016"
  shape: bbox 12.11 x 4.605 x 2.705 mm, 1046 faces (baked)
FEATURE [Part::Feature] Part__Feature1474  label="rt017"
  shape: bbox 5 x 7 x 1.1 mm, 7 faces (baked)
FEATURE [Part::Feature] Part__Feature1475  label="rt018"
  shape: bbox 0.4 x 2 x 16.99 mm, 25 faces (baked)
FEATURE [Part::Feature] Part__Feature1476  label="rt019"
  shape: bbox 0.4 x 2 x 16.99 mm, 25 faces (baked)
FEATURE [Part::Feature] Part__Feature1477  label="rt020"
  shape: bbox 0.4 x 2 x 16.99 mm, 25 faces (baked)
FEATURE [Part::Feature] Part__Feature1478  label="rt021"
  shape: bbox 0.4 x 2 x 16.99 mm, 25 faces (baked)
FEATURE [Part::Feature] Part__Feature1479  label="rt022"
  shape: bbox 0.4 x 2 x 16.99 mm, 25 faces (baked)
FEATURE [Part::Feature] Part__Feature1480  label="rt023"
  shape: bbox 0.4 x 2 x 16.99 mm, 25 faces (baked)
FEATURE [Part::Feature] Part__Feature1481  label="rt024"
  shape: bbox 0.4 x 2 x 16.99 mm, 25 faces (baked)
FEATURE [Part::Feature] Part__Feature1482  label="rt025"
  shape: bbox 0.4 x 2 x 16.99 mm, 25 faces (baked)
FEATURE [Part::Feature] Part__Feature1483  label="rt026"
  shape: bbox 2.54 x 20.32 x 8.5 mm, 114 faces (baked)
FEATURE [Part::Feature] Part__Feature1484  label="rt027"
  shape: bbox 0.4 x 2 x 16.99 mm, 25 faces (baked)
FEATURE [Part::Feature] Part__Feature1485  label="rt028"
  shape: bbox 0.4 x 2 x 16.99 mm, 25 faces (baked)
FEATURE [Part::Feature] Part__Feature1486  label="rt029"
  shape: bbox 0.4 x 2 x 16.99 mm, 25 faces (baked)
FEATURE [Part::Feature] Part__Feature1487  label="rt030"
  shape: bbox 0.4 x 2 x 16.99 mm, 25 faces (baked)
FEATURE [Part::Feature] Part__Feature1488  label="rt031"
  shape: bbox 0.4 x 2 x 16.99 mm, 25 faces (baked)
FEATURE [Part::Feature] Part__Feature1489  label="rt032"
  shape: bbox 0.4 x 2 x 16.99 mm, 25 faces (baked)
FEATURE [Part::Feature] Part__Feature1490  label="rt033"
  shape: bbox 0.4 x 2 x 16.99 mm, 25 faces (baked)
FEATURE [Part::Feature] Part__Feature1491  label="rt034"
  shape: bbox 0.4 x 2 x 16.99 mm, 25 faces (baked)
FEATURE [Part::Feature] Part__Feature1492  label="rt035"
  shape: bbox 2.54 x 20.32 x 8.5 mm, 114 faces (baked)
FEATURE [Part::Feature] Part__Feature1495  label="rt038"
  shape: bbox 6 x 7.7 x 8.35 mm, 81 faces (baked)
FEATURE [Part::Feature] Part__Feature1501  label="rt044"
  shape: bbox 8 x 8 x 1.2 mm, 7 faces (baked)
FEATURE [Part::Feature] Part__Feature1503  label="rt046"
  shape: bbox 5 x 6 x 1 mm, 6 faces (baked)
FEATURE [Part::Feature] Part__Feature1507  label="rt050"
  shape: bbox 10 x 10 x 1.5 mm, 6 faces (baked)
FEATURE [Part::Feature] Part__Feature1510  label="rt053"
  shape: bbox 5.08 x 6.35 x 5.715 mm, 90 faces (baked)
FEATURE [Part::Feature] Part__Feature1511  label="rt054"
  shape: bbox 1.676 x 5.486 x 4.293 mm, 91 faces (baked)
FEATURE [Part::Feature] Part__Feature1512  label="rt055"
  shape: bbox 5.842 x 5.486 x 2.017 mm, 71 faces (baked)
FEATURE [Part::Feature] Part__Feature1514  label="rt057"
  shape: bbox 4 x 4 x 1 mm, 7 faces (baked)
FEATURE [Part::Feature] Part__Feature1517  label="rt060"
  shape: bbox 0.4 x 2 x 16.99 mm, 25 faces (baked)
FEATURE [Part::Feature] Part__Feature1518  label="rt061"
  shape: bbox 0.4 x 2 x 16.99 mm, 25 faces (baked)
FEATURE [Part::Feature] Part__Feature1519  label="rt062"
  shape: bbox 0.4 x 2 x 16.99 mm, 25 faces (baked)
FEATURE [Part::Feature] Part__Feature1520  label="rt063"
  shape: bbox 0.4 x 2 x 16.99 mm, 25 faces (baked)
FEATURE [Part::Feature] Part__Feature1521  label="rt064"
  shape: bbox 0.4 x 2 x 16.99 mm, 25 faces (baked)
FEATURE [Part::Feature] Part__Feature1522  label="rt065"
  shape: bbox 0.4 x 2 x 16.99 mm, 25 faces (baked)
FEATURE [Part::Feature] Part__Feature1523  label="rt066"
  shape: bbox 0.4 x 2 x 16.99 mm, 25 faces (baked)
FEATURE [Part::Feature] Part__Feature1524  label="rt067"
  shape: bbox 0.4 x 2 x 16.99 mm, 25 faces (baked)
FEATURE [Part::Feature] Part__Feature1525  label="rt068"
  shape: bbox 2.54 x 20.32 x 8.5 mm, 114 faces (baked)
FEATURE [Part::Feature] Part__Feature1527  label="rt070"
  shape: bbox 3.2 x 1.6 x 1.2 mm, 240 faces (baked)
FEATURE [Part::Feature] Part__Feature1542  label="rt085"
  shape: bbox 1.6 x 2 x 0.65 mm, 6 faces (baked)
FEATURE [Part::Feature] Part__Feature1543  label="rt086"
  shape: bbox 1.4 x 3.2 x 1 mm, 6 faces (baked)
FEATURE [Part::Feature] Part__Feature1544  label="rt087"
  shape: bbox 2.5 x 1.2 x 0.5 mm, 6 faces (baked)
FEATURE [Part::Feature] Part__Feature1547  label="rt090"
  shape: bbox 0.8 x 1.5 x 0.35 mm, 6 faces (baked)
FEATURE [Part::Feature] Part__Feature1548  label="rt091"
  shape: bbox 0.8 x 1.1 x 0.049 mm, 6 faces (baked)
FEATURE [Part::Feature] Part__Feature1549  label="rt092"
  shape: bbox 3 x 3 x 1 mm, 6 faces (baked)
FEATURE [Part::Feature] Part__Feature1576  label="rt119"
  shape: bbox 3 x 3 x 0.3 mm, 6 faces (baked)
FEATURE [Part::Feature] Part__Feature1578  label="rt121"
  shape: bbox 1.2 x 1.6 x 0.62 mm, 6 faces (baked)
FEATURE [Part::Feature] Part__Feature1585  label="rt128"
  shape: bbox 1.5 x 2.5 x 0.6 mm, 7 faces (baked)
FEATURE [Part::Feature] Part__Feature1591  label="rt134"
  shape: bbox 2 x 1.25 x 1.25 mm, 58 faces (baked)
FEATURE [Part::Feature] Part__Feature1603  label="rt146"
  shape: bbox 2 x 1.25 x 1.25 mm, 58 faces (baked)
FEATURE [Part::Feature] Part__Feature1604  label="rt147"
  shape: bbox 2 x 1.25 x 1.25 mm, 58 faces (baked)
FEATURE [Part::Feature] Part__Feature1608  label="rt151"
  shape: bbox 1.5 x 2.5 x 0.6 mm, 7 faces (baked)
FEATURE [Part::Feature] Part__Feature1615  label="rt158"
  shape: bbox 1.351 x 2.201 x 1.05 mm, 34 faces (baked)
FEATURE [Part::Feature] Part__Feature1616  label="rt159"
  shape: bbox 1.6 x 2 x 1 mm, 7 faces (baked)
FEATURE [Part::Feature] Part__Feature1617  label="rt160"
  shape: bbox 0.5 x 1 x 0.5 mm, 58 faces (baked)
FEATURE [Part::Feature] Part__Feature1700  label="rt243"
  shape: bbox 1.25 x 2 x 1.25 mm, 58 faces (baked)
FEATURE [Part::Feature] Part__Feature1702  label="rt245"
  shape: bbox 1.25 x 2 x 1.25 mm, 58 faces (baked)
FEATURE [Part::Feature] Part__Feature1703  label="rt246"
  shape: bbox 1.6 x 2 x 1 mm, 7 faces (baked)
FEATURE [Part::Feature] Part__Feature1722  label="rt265"
  shape: bbox 2 x 1.25 x 1.25 mm, 58 faces (baked)
FEATURE [Part::Feature] Part__Feature1723  label="rt266"
  shape: bbox 1.25 x 2 x 1.25 mm, 58 faces (baked)
FEATURE [Part::Feature] Part__Feature1738  label="rt281"
  shape: bbox 2 x 1.25 x 1.25 mm, 58 faces (baked)
FEATURE [Part::Feature] Part__Feature1739  label="rt282"
  shape: bbox 11.4 x 11.95 x 1.452 mm, 410 faces (baked)
FEATURE [Part::Feature] Part__Feature1740  label="rt283"
  shape: bbox 1.25 x 2 x 1.25 mm, 58 faces (baked)
FEATURE [Part::Feature] Part__Feature1741  label="rt284"
  shape: bbox 2 x 1.25 x 1.25 mm, 58 faces (baked)
FEATURE [Part::Feature] Part__Feature1742  label="rt285"
  shape: bbox 1.25 x 2 x 1.25 mm, 58 faces (baked)
FEATURE [Part::Feature] Part__Feature1750  label="rt293"
  shape: bbox 1.5 x 2.5 x 0.6 mm, 7 faces (baked)
FEATURE [Part::Feature] Part__Feature1754  label="rt297"
  shape: bbox 1.2 x 1.6 x 0.6 mm, 6 faces (baked)
FEATURE [Part::Feature] Part__Feature1757  label="rt300"
  shape: bbox 2 x 1.25 x 1.25 mm, 58 faces (baked)
FEATURE [Part::Feature] Part__Feature1758  label="rt301"
  shape: bbox 1.6 x 2 x 1 mm, 7 faces (baked)
FEATURE [Part::Feature] Part__Feature1768  label="rt311"
  shape: bbox 2.988 x 2.8 x 1.175 mm, 78 faces (baked)
FEATURE [Part::Feature] Part__Feature1772  label="rt315"
  shape: bbox 1.351 x 2.201 x 1.05 mm, 34 faces (baked)
FEATURE [Part::Feature] Part__Feature1776  label="rt319"
  shape: bbox 1.351 x 2.201 x 1.05 mm, 34 faces (baked)
FEATURE [Part::Feature] Part__Feature1777  label="rt320"
  shape: bbox 2.2 x 1.2 x 0.6 mm, 7 faces (baked)
FEATURE [Part::Feature] Part__Feature1778  label="rt321"
  shape: bbox 1.25 x 2 x 1.25 mm, 58 faces (baked)
FEATURE [Part::Feature] Part__Feature1779  label="rt322"
  shape: bbox 1.25 x 2 x 1.25 mm, 58 faces (baked)
FEATURE [Part::Feature] Part__Feature1796  label="rt339"
  shape: bbox 8.34 x 6.62 x 3.56 mm, 238 faces (baked)
FEATURE [Part::Feature] Part__Feature1823  label="rt366"
  shape: bbox 9.58 x 7.53 x 4.16 mm, 463 faces (baked)
FEATURE [Part::Feature] Part__Feature1828  label="rt371"
  shape: bbox 0.4 x 2 x 16.99 mm, 25 faces (baked)
FEATURE [Part::Feature] Part__Feature1829  label="rt372"
  shape: bbox 0.4 x 2 x 16.99 mm, 25 faces (baked)
FEATURE [Part::Feature] Part__Feature1830  label="rt373"
  shape: bbox 0.4 x 2 x 16.99 mm, 25 faces (baked)
FEATURE [Part::Feature] Part__Feature1831  label="rt374"
  shape: bbox 0.4 x 2 x 16.99 mm, 25 faces (baked)
FEATURE [Part::Feature] Part__Feature1832  label="rt375"
  shape: bbox 0.4 x 2 x 16.99 mm, 25 faces (baked)
FEATURE [Part::Feature] Part__Feature1833  label="rt376"
  shape: bbox 0.4 x 2 x 16.99 mm, 25 faces (baked)
FEATURE [Part::Feature] Part__Feature1834  label="rt377"
  shape: bbox 0.4 x 2 x 16.99 mm, 25 faces (baked)
FEATURE [Part::Feature] Part__Feature1835  label="rt378"
  shape: bbox 0.4 x 2 x 16.99 mm, 25 faces (baked)
FEATURE [Part::Feature] Part__Feature1836  label="rt379"
  shape: bbox 2.54 x 20.32 x 8.5 mm, 114 faces (baked)
FEATURE [Part::Feature] Part__Feature1837  label="rt380"
  shape: bbox 0.5 x 1 x 0.3375 mm, 36 faces (baked)
FEATURE [Part::Feature] Part__Feature1857  label="rt400"
  shape: bbox 4.718 x 3.55 x 1.549 mm, 350 faces (baked)
FEATURE [Part::Feature] Part__Feature1862  label="rt405"
  shape: bbox 2.5 x 3.2 x 0.8 mm, 47 faces (baked)
FEATURE [Part::Feature] Part__Feature1863  label="rt406"
  shape: bbox 3.21 x 1.803 x 2.385 mm, 34 faces (baked)
FEATURE [Part::Feature] Part__Feature1874  label="rt417"
  shape: bbox 4.718 x 3.55 x 1.549 mm, 350 faces (baked)
FEATURE [Part::Feature] Part__Feature1878  label="rt421"
  shape: bbox 1.803 x 3.21 x 2.385 mm, 34 faces (baked)
FEATURE [Part::Feature] Part__Feature1886  label="rt429"
  shape: bbox 0.991 x 2.312 x 1.054 mm, 10 faces (baked)
FEATURE [Part::Feature] Part__Feature1887  label="rt430"
  shape: bbox 0.991 x 2.312 x 1.054 mm, 10 faces (baked)
FEATURE [Part::Feature] Part__Feature1888  label="rt431"
  shape: bbox 3.088 x 2.999 x 2.109 mm, 16 faces (baked)
FEATURE [Part::Feature] Part__Feature1889  label="rt432"
  shape: bbox 0.617 x 2.874 x 0.051 mm, 6 faces (baked)
FEATURE [Part::Feature] Part__Feature1890  label="rt433"
  shape: bbox 0.991 x 2.312 x 1.054 mm, 10 faces (baked)
FEATURE [Part::Feature] Part__Feature1891  label="rt434"
  shape: bbox 0.991 x 2.312 x 1.054 mm, 10 faces (baked)
FEATURE [Part::Feature] Part__Feature1892  label="rt435"
  shape: bbox 3.088 x 2.999 x 2.109 mm, 16 faces (baked)
FEATURE [Part::Feature] Part__Feature1893  label="rt436"
  shape: bbox 0.617 x 2.874 x 0.051 mm, 6 faces (baked)
FEATURE [Part::Feature] Part__Feature1905  label="rt448"
  shape: bbox 35.56 x 44.45 x 1.2 mm, 64 faces (baked)
FEATURE [Part::Feature] Part__Feature1906  label="rt449"
  shape: bbox 15.5 x 16.25 x 6.3 mm, 24 faces (baked)
FEATURE [Part::Feature] Part__Feature1907  label="rt450"
  shape: bbox 23.8 x 17 x 8 mm, 20 faces (baked)
FEATURE [App::Part] rt10  label="OpenMV RT1062"
  Group = -> [Part__Feature1467,Part__Feature1468,Part__Feature1469,Part__Feature1470,Part__Feature1471,Part__Feature1472,Part__Feature1473,Part__Feature1474,Part__Feature1475,Part__Feature1476,Part__Feature1477,Part__Feature1478,Part__Feature1479,Part__Feature1480,Part__Feature1481,Part__Feature1482,Part__Feature1483,Part__Feature1484,Part__Feature1485,Part__Feature1486,Part__Feature1487,Part__Feature1488,+86 more]
  Origin = -> Origin341
  Placement = pos=(0,0,4.2) rot=(0,0,1;0rad)
FEATURE [PartDesign::SubShapeBinder] Binder047
  BindCopyOnChange = 0
  BindMode = 0
  ClaimChildren = false
  Context = -> Part012 [Body003.Binder047.]
  Fuse = false
  MakeFace = true
  OffsetFill = false
  OffsetIntersection = false
  OffsetJoinType = 0
  OffsetOpenResult = false
  PartialLoad = false
  Relative = true
  Support = -> [Body[Pocket055.Sketch126.]]
  _Version = 2
FEATURE [PartDesign::SubShapeBinder] Binder048
  BindCopyOnChange = 0
  BindMode = 0
  ClaimChildren = false
  Context = -> Part012 [Body051.Binder048.]
  Fuse = false
  MakeFace = true
  OffsetFill = false
  OffsetIntersection = false
  OffsetJoinType = 0
  OffsetOpenResult = false
  PartialLoad = false
  Relative = true
  Support = -> [Body[Pocket055.Sketch126.]]
  _Version = 2
FEATURE [PartDesign::SubShapeBinder] Binder049
  BindCopyOnChange = 0
  BindMode = 0
  ClaimChildren = false
  Context = -> Part012 [Body052.Binder049.]
  Fuse = false
  MakeFace = true
  OffsetFill = false
  OffsetIntersection = false
  OffsetJoinType = 0
  OffsetOpenResult = false
  PartialLoad = false
  Relative = true
  Support = -> [Body[Pocket055.Sketch126.]]
  _Version = 2
FEATURE [PartDesign::Pocket] Pocket119
  BaseFeature = -> Revolution003
  Direction = (0,0,-1)
  Length = 5
  Length2 = 5
  Placement = pos=(0,0,0) rot=(1,0,0;1.5708rad)
  Profile = -> Binder049
  Type = 1
FEATURE [PartDesign::Body] Body052  label="Outer shielding 3"
  Group = -> [Sketch128,Revolution003,Binder049,Pocket119]
  Origin = -> Origin257
  Placement = pos=(0,-3,0) rot=(0,0,-1;1.5708rad)
  Tip = -> Pocket119
FEATURE [PartDesign::Pocket] Pocket120
  BaseFeature = -> Revolution002
  Direction = (0,0,-1)
  Length = 5
  Length2 = 5
  Placement = pos=(0,0,0) rot=(1,0,0;1.5708rad)
  Profile = -> Binder048
  Type = 1
FEATURE [PartDesign::Body] Body051  label="Outer shielding 2"
  Group = -> [Sketch127,Revolution002,Binder048,Pocket120]
  Origin = -> Origin256
  Placement = pos=(-3,1e-15,0) rot=(0,0,1;3.14159rad)
  Tip = -> Pocket120
FEATURE [PartDesign::Pocket] Pocket121
  BaseFeature = -> Revolution001
  Direction = (0,0,-1)
  Length = 5
  Length2 = 5
  Placement = pos=(0,0,0) rot=(1,0,0;1.5708rad)
  Profile = -> Binder047
  Type = 1
FEATURE [PartDesign::SubShapeBinder] Binder050
  BindCopyOnChange = 0
  BindMode = 0
  ClaimChildren = false
  Context = -> Body [Binder050.]
  Fuse = false
  MakeFace = true
  OffsetFill = false
  OffsetIntersection = false
  OffsetJoinType = 0
  OffsetOpenResult = false
  PartialLoad = false
  Relative = true
  Support = -> [Part015[Body025.Pocket112.Sketch250.]]
  _Version = 2
FEATURE [PartDesign::Pocket] Pocket122
  BaseFeature = -> Pocket109
  Direction = (-2e-16,-2e-16,-1)
  Length = 5
  Length2 = 5
  Profile = -> Binder050
  Type = 1
FEATURE [Sketcher::SketchObject] Sketch251
  FullyConstrained = false
  MapMode = 5
  Placement = pos=(0,0,3) rot=(0,0,1;0rad)
  sketch-geometry (2):
    g0: Circle CenterX=0 CenterY=0 CenterZ=0 NormalX=0 NormalY=0 NormalZ=1 AngleXU=0 Radius=28
    g1: Circle CenterX=0 CenterY=0 CenterZ=0 NormalX=0 NormalY=0 NormalZ=1 AngleXU=0 Radius=25.25
  constraints (2):
    c: Coincident(g1,g0)
    c: Diameter(g1) = 50.5
FEATURE [PartDesign::Pad] Pad095
  BaseFeature = -> Pad007
  Direction = (0,0,1)
  Length = 5
  Length2 = 10
  Profile = -> Sketch251
  ReferenceAxis = -> Sketch251 [N_Axis]
  Type = 0
FEATURE [Sketcher::SketchObject] Sketch253
  FullyConstrained = true
  MapMode = 5
  Placement = pos=(0,0,0) rot=(0.57735,0.57735,-0.57735;4.18879rad)
  Support = -> [Pad076]
  sketch-geometry (1):
    g0: Circle CenterX=0 CenterY=0 CenterZ=0 NormalX=0 NormalY=0 NormalZ=1 AngleXU=0 Radius=1
  constraints (2):
    c: Coincident(g0,g-1)
    c: Diameter(g0) = 2
FEATURE [PartDesign::Pocket] Pocket123
  BaseFeature = -> Pad076
  Direction = (1,-7e-16,3e-16)
  Length = 5
  Length2 = 5
  Placement = pos=(0,0,0) rot=(0.57735,0.57735,0.57735;2.0944rad)
  Profile = -> Sketch253
  ReferenceAxis = -> Sketch253 [N_Axis]
  Type = 1
FEATURE [PartDesign::Body] Body046  label="Kicker plate"
  Group = -> [Sketch109,Pad076,Sketch253,Pocket123]
  Origin = -> Origin251
  Placement = pos=(-79,0,-2) rot=(0,0,1;0rad)
  Tip = -> Pocket123
FEATURE [App::Part] Part013  label="Kicker"
  Group = -> [Body045,Body046,Body049]
  Origin = -> Origin249
  Placement = pos=(7,-2.9e-15,-23) rot=(1,0,0;3.14159rad)
FEATURE [Sketcher::SketchObject] Sketch254
  FullyConstrained = true
  MapMode = 5
  Placement = pos=(0,50,-1e-16) rot=(-1,0,0;1.5708rad)
  Support = -> [Pad058]
  sketch-geometry (1):
    g0: Circle CenterX=0 CenterY=0 CenterZ=0 NormalX=0 NormalY=0 NormalZ=1 AngleXU=0 Radius=2
  constraints (2):
    c: Coincident(g0,g-1)
    c: Diameter(g0) = 4
FEATURE [PartDesign::Pad] Pad097
  BaseFeature = -> Pad058
  Direction = (0,1,2e-16)
  Length = 17.5
  Length2 = 10
  Placement = pos=(0,0,0) rot=(1,0,0;1.5708rad)
  Profile = -> Sketch254
  ReferenceAxis = -> Sketch254 [N_Axis]
  Type = 0
FEATURE [PartDesign::Body] Body034  label="Dribbler motor"
  Group = -> [Sketch082,Pad058,Sketch254,Pad097]
  Origin = -> Origin237
  Placement = pos=(-48.5,-34,17.9) rot=(0,-1,0;1.5708rad)
  Tip = -> Pad097
FEATURE [PartDesign::SubShapeBinder] Binder051
  BindCopyOnChange = 0
  BindMode = 0
  ClaimChildren = false
  Context = -> Part011 [Body050.Binder051.]
  Fuse = false
  MakeFace = true
  OffsetFill = false
  OffsetIntersection = false
  OffsetJoinType = 0
  OffsetOpenResult = false
  PartialLoad = false
  Relative = true
  Support = -> [Part013[Body049.Pocket108.Sketch137.]]
  _Version = 2
FEATURE [PartDesign::Pocket] Pocket124
  BaseFeature = -> PolarPattern018
  Direction = (0,0,-1)
  Length = 5
  Length2 = 5
  Placement = pos=(0,0,0) rot=(1,0,0;1.5708rad)
  Profile = -> Binder051
  Type = 1
FEATURE [PartDesign::Body] Body050  label="Dribbler support"
  Group = -> [Sketch121,Pad085,Sketch122,Pad086,Sketch123,Pocket048,Sketch124,Pocket049,PolarPattern018,Binder051,Pocket124]
  Origin = -> Origin255
  Placement = pos=(-48.5401,18.0401,18) rot=(0,1,0;3.14159rad)
  Tip = -> Pocket124
FEATURE [App::Part] Part011  label="Dribbler"
  Group = -> [Body034,Body035,Body036,Body037,Body050]
  Origin = -> Origin236
  Placement = pos=(4,0,1) rot=(0,0,1;0rad)
FEATURE [Part::Feature] Part__Feature1908  label="HC05_Pcb"
  Placement = pos=(14.7308,31.0562,28.3016) rot=(-1,0,0;1.5708rad)
  shape: bbox 35.75 x 1.502 x 15.75 mm, 1080 faces (baked)
FEATURE [Part::Feature] Part__Feature1909  label="HC05_06"
  Placement = pos=(6.11873,45.8979,22.3358) rot=(-1,0,0;1.5708rad)
  shape: bbox 27.01 x 1.902 x 13.01 mm, 1526 faces (baked)
FEATURE [Part::Feature] Part__Feature1910  label="C0603"
  Placement = pos=(11.7437,47.1529,18.3773) rot=(0,1,0;1.5708rad)
  shape: bbox 0.91 x 0.91 x 1.6 mm, 44 faces (baked)
FEATURE [Part::Feature] Part__Feature1911  label="R0402_По умолчанию"
  Placement = pos=(11.7437,46.6979,20.9264) rot=(0,1,0;1.5708rad)
  shape: bbox 0.5 x 0.2 x 0.3 mm, 24 faces (baked)
FEATURE [Part::Feature] Part__Feature1912  label="R0402_По умолчанию001"
  Placement = pos=(11.7437,46.6979,20.9264) rot=(0,1,0;1.5708rad)
  shape: bbox 0.5 x 0.2 x 0.3 mm, 24 faces (baked)
FEATURE [Part::Feature] Part__Feature1913  label="R0402_По умолчанию002"
  Placement = pos=(11.7437,46.6979,20.9264) rot=(0,1,0;1.5708rad)
  shape: bbox 0.5 x 0.16 x 0.96 mm, 6 faces (baked)
FEATURE [Part::Feature] Part__Feature1914  label="R0402_По умолчанию003"
  Placement = pos=(11.7437,46.6979,20.9264) rot=(0,1,0;1.5708rad)
  shape: bbox 0.5 x 0.011 x 0.4 mm, 48 faces (baked)
FEATURE [App::Part] R0402________________________  label="R0402_По умолчанию004"
  Group = -> [Part__Feature1911,Part__Feature1912,Part__Feature1913,Part__Feature1914]
  Origin = -> Origin343
FEATURE [Part::Feature] Part__Feature1915  label="C0402"
  Placement = pos=(11.7437,46.9479,24.2945) rot=(0,1,0;1.5708rad)
  shape: bbox 0.5 x 0.5 x 1 mm, 44 faces (baked)
FEATURE [Part::Feature] Part__Feature1916  label="C0604"
  Placement = pos=(10.4261,47.1529,26.5383) rot=(0,0,1;0rad)
  shape: bbox 1.6 x 0.91 x 0.91 mm, 44 faces (baked)
FEATURE [Part::Feature] Part__Feature1917  label="C0605"
  Placement = pos=(16.8292,46.9479,26.5383) rot=(0,1,0;1.5708rad)
  shape: bbox 0.5 x 0.5 x 1 mm, 44 faces (baked)
FEATURE [Part::Feature] Part__Feature1918  label="C0606"
  Placement = pos=(15.7948,46.9479,26.5383) rot=(0,1,0;1.5708rad)
  shape: bbox 0.5 x 0.5 x 1 mm, 44 faces (baked)
FEATURE [Part::Feature] Part__Feature1919  label="R0402_По умолчанию005"
  Placement = pos=(14.7519,46.6979,26.5383) rot=(0,1,0;1.5708rad)
  shape: bbox 0.5 x 0.2 x 0.3 mm, 24 faces (baked)
FEATURE [Part::Feature] Part__Feature1920  label="R0402_По умолчанию006"
  Placement = pos=(14.7519,46.6979,26.5383) rot=(0,1,0;1.5708rad)
  shape: bbox 0.5 x 0.2 x 0.3 mm, 24 faces (baked)
FEATURE [Part::Feature] Part__Feature1921  label="R0402_По умолчанию007"
  Placement = pos=(14.7519,46.6979,26.5383) rot=(0,1,0;1.5708rad)
  shape: bbox 0.5 x 0.16 x 0.96 mm, 6 faces (baked)
FEATURE [Part::Feature] Part__Feature1922  label="R0402_По умолчанию008"
  Placement = pos=(14.7519,46.6979,26.5383) rot=(0,1,0;1.5708rad)
  shape: bbox 0.5 x 0.011 x 0.4 mm, 48 faces (baked)
FEATURE [App::Part] R0402________________________001  label="R0402_По умолчанию009"
  Group = -> [Part__Feature1919,Part__Feature1920,Part__Feature1921,Part__Feature1922]
  Origin = -> Origin344
FEATURE [Part::Feature] Part__Feature1923  label="C0607"
  Placement = pos=(1.47652,46.9479,26.3896) rot=(0,1,0;1.5708rad)
  shape: bbox 0.5 x 0.5 x 1 mm, 44 faces (baked)
FEATURE [Part::Feature] Part__Feature1924  label="C0608"
  Placement = pos=(6.67848,46.9479,26.3896) rot=(0,1,0;1.5708rad)
  shape: bbox 0.5 x 0.5 x 1 mm, 44 faces (baked)
FEATURE [Part::Feature] Part__Feature1925  label="C0609"
  Placement = pos=(-0.660855,47.1529,26.2345) rot=(0,0,1;0rad)
  shape: bbox 1.6 x 0.91 x 0.91 mm, 44 faces (baked)
FEATURE [Part::Feature] Part__Feature1926  label="C0610"
  Placement = pos=(-1.35714,46.9479,24.2036) rot=(0,1,0;1.5708rad)
  shape: bbox 0.5 x 0.5 x 1 mm, 44 faces (baked)
FEATURE [Part::Feature] Part__Feature1927  label="C0611"
  Placement = pos=(1.59394,46.9479,17.546) rot=(0,1,0;1.5708rad)
  shape: bbox 0.5 x 0.5 x 1 mm, 44 faces (baked)
FEATURE [Part::Feature] Part__Feature1928  label="C0612"
  Placement = pos=(-0.165737,46.9479,17.546) rot=(0,1,0;1.5708rad)
  shape: bbox 0.5 x 0.5 x 1 mm, 44 faces (baked)
FEATURE [Part::Feature] Part__Feature1929  label="R0402_По умолчанию010"
  Placement = pos=(-1.09295,46.6979,17.546) rot=(0,1,0;1.5708rad)
  shape: bbox 0.5 x 0.2 x 0.3 mm, 24 faces (baked)
FEATURE [Part::Feature] Part__Feature1930  label="R0402_По умолчанию011"
  Placement = pos=(-1.09295,46.6979,17.546) rot=(0,1,0;1.5708rad)
  shape: bbox 0.5 x 0.2 x 0.3 mm, 24 faces (baked)
FEATURE [Part::Feature] Part__Feature1931  label="R0402_По умолчанию012"
  Placement = pos=(-1.09295,46.6979,17.546) rot=(0,1,0;1.5708rad)
  shape: bbox 0.5 x 0.16 x 0.96 mm, 6 faces (baked)
FEATURE [Part::Feature] Part__Feature1932  label="R0402_По умолчанию013"
  Placement = pos=(-1.09295,46.6979,17.546) rot=(0,1,0;1.5708rad)
  shape: bbox 0.5 x 0.011 x 0.4 mm, 48 faces (baked)
FEATURE [App::Part] R0402________________________002  label="R0402_По умолчанию014"
  Group = -> [Part__Feature1929,Part__Feature1930,Part__Feature1931,Part__Feature1932]
  Origin = -> Origin345
FEATURE [Part::Feature] Part__Feature1933  label="R0402_По умолчанию015"
  Placement = pos=(-0.431698,46.6979,24.2036) rot=(0,1,0;1.5708rad)
  shape: bbox 0.5 x 0.2 x 0.3 mm, 24 faces (baked)
FEATURE [Part::Feature] Part__Feature1934  label="R0402_По умолчанию016"
  Placement = pos=(-0.431698,46.6979,24.2036) rot=(0,1,0;1.5708rad)
  shape: bbox 0.5 x 0.2 x 0.3 mm, 24 faces (baked)
FEATURE [Part::Feature] Part__Feature1935  label="R0402_По умолчанию017"
  Placement = pos=(-0.431698,46.6979,24.2036) rot=(0,1,0;1.5708rad)
  shape: bbox 0.5 x 0.16 x 0.96 mm, 6 faces (baked)
FEATURE [Part::Feature] Part__Feature1936  label="R0402_По умолчанию018"
  Placement = pos=(-0.431698,46.6979,24.2036) rot=(0,1,0;1.5708rad)
  shape: bbox 0.5 x 0.011 x 0.4 mm, 48 faces (baked)
FEATURE [App::Part] R0402________________________003  label="R0402_По умолчанию019"
  Group = -> [Part__Feature1933,Part__Feature1934,Part__Feature1935,Part__Feature1936]
  Origin = -> Origin346
FEATURE [Part::Feature] Part__Feature1937  label="C0613"
  Placement = pos=(1.38648,46.9479,24.4072) rot=(0,0,1;0rad)
  shape: bbox 1 x 0.5 x 0.5 mm, 44 faces (baked)
FEATURE [Part::Feature] Part__Feature1938  label="QSMD7.0x5.0x1.3"
  Placement = pos=(4.0775,46.698,26.3896) rot=(0,0,1;0rad)
  shape: bbox 3.51 x 0.8001 x 2 mm, 196 faces (baked)
FEATURE [App::Part] HC05_06  label="HC05_007"
  Group = -> [Part__Feature1909,Part__Feature1910,R0402________________________,Part__Feature1915,Part__Feature1916,Part__Feature1917,Part__Feature1918,R0402________________________001,Part__Feature1923,Part__Feature1924,Part__Feature1925,Part__Feature1926,Part__Feature1927,Part__Feature1928,R0402________________________002,R0402________________________003,Part__Feature1937,Part__Feature1938]
  Origin = -> Origin347
  Placement = pos=(4.98703,-13.3397,5.96586) rot=(0,0,1;0rad)
FEATURE [Part::Feature] Part__Feature1939  label="Pines_90"
  Placement = pos=(31.1058,32.5572,34.6516) rot=(0,1,0;1.5708rad)
  shape: bbox 8.54 x 9.358 x 2.54 mm, 44 faces (baked)
FEATURE [Part::Feature] Part__Feature1940  label="Pines_091"
  Placement = pos=(31.1058,32.5572,34.6516) rot=(0,1,0;1.5708rad)
  shape: bbox 8.54 x 9.358 x 2.54 mm, 44 faces (baked)
FEATURE [Part::Feature] Part__Feature1941  label="Pines_092"
  Placement = pos=(31.1058,32.5572,34.6516) rot=(0,1,0;1.5708rad)
  shape: bbox 8.54 x 9.358 x 2.34 mm, 40 faces (baked)
FEATURE [Part::Feature] Part__Feature1942  label="Pines_093"
  Placement = pos=(31.1058,32.5572,34.6516) rot=(0,1,0;1.5708rad)
  shape: bbox 8.54 x 9.358 x 2.54 mm, 44 faces (baked)
FEATURE [Part::Feature] Part__Feature1943  label="Pines_094"
  Placement = pos=(31.1058,32.5572,34.6516) rot=(0,1,0;1.5708rad)
  shape: bbox 8.54 x 9.358 x 2.54 mm, 44 faces (baked)
FEATURE [Part::Feature] Part__Feature1944  label="Pines_095"
  Placement = pos=(31.1058,32.5572,34.6516) rot=(0,1,0;1.5708rad)
  shape: bbox 8.54 x 9.358 x 2.54 mm, 44 faces (baked)
FEATURE [App::Part] Pines_90  label="Pines_096"
  Group = -> [Part__Feature1939,Part__Feature1940,Part__Feature1941,Part__Feature1942,Part__Feature1943,Part__Feature1944]
  Origin = -> Origin348
FEATURE [Part::Feature] Part__Feature1945  label="Led 0603 Smd"
  Placement = pos=(27.7897,32.5812,34.6166) rot=(-0.57735,-0.57735,-0.57735;2.0944rad)
  shape: bbox 0.7202 x 0.421 x 1.02 mm, 18 faces (baked)
FEATURE [Part::Feature] Part__Feature1946  label="Led 0603 Smd001"
  Placement = pos=(27.7897,32.5812,34.6166) rot=(-0.57735,-0.57735,-0.57735;2.0944rad)
  shape: bbox 0.8 x 0.275 x 1.45 mm, 34 faces (baked)
FEATURE [App::Part] Led_0603_Smd  label="Led 0603 Smd002"
  Group = -> [Part__Feature1945,Part__Feature1946]
  Origin = -> Origin349
FEATURE [Part::Feature] Part__Feature1947  label="C0614"
  Placement = pos=(28.9889,33.0112,31.4787) rot=(0,1,0;1.5708rad)
  shape: bbox 0.91 x 0.91 x 1.6 mm, 44 faces (baked)
FEATURE [Part::Feature] Part__Feature1948  label="R0603 222_По умолчанию"
  Placement = pos=(28.9889,32.5562,34.6467) rot=(0,1,0;1.5708rad)
  shape: bbox 0.8 x 0.45 x 0.3 mm, 24 faces (baked)
FEATURE [Part::Feature] Part__Feature1949  label="R0603 222_По умолчанию001"
  Placement = pos=(28.9889,32.5562,34.6467) rot=(0,1,0;1.5708rad)
  shape: bbox 0.8 x 0.45 x 0.3 mm, 24 faces (baked)
FEATURE [Part::Feature] Part__Feature1950  label="R0603 222_По умолчанию002"
  Placement = pos=(28.9889,32.5562,34.6467) rot=(0,1,0;1.5708rad)
  shape: bbox 0.8 x 0.39 x 1.54 mm, 6 faces (baked)
FEATURE [Part::Feature] Part__Feature1951  label="R0603 222_По умолчанию003"
  Placement = pos=(28.9889,32.5562,34.6467) rot=(0,1,0;1.5708rad)
  shape: bbox 0.8 x 0.016 x 1 mm, 48 faces (baked)
FEATURE [App::Part] R0603_222________________________  label="R0603 222_По умолчанию004"
  Group = -> [Part__Feature1948,Part__Feature1949,Part__Feature1950,Part__Feature1951]
  Origin = -> Origin350
FEATURE [Part::Feature] Part__Feature1952  label="R0603 222_По умолчанию005"
  Placement = pos=(28.9889,32.5562,24.8143) rot=(0,1,0;1.5708rad)
  shape: bbox 0.8 x 0.45 x 0.3 mm, 24 faces (baked)
FEATURE [Part::Feature] Part__Feature1953  label="R0603 222_По умолчанию006"
  Placement = pos=(28.9889,32.5562,24.8143) rot=(0,1,0;1.5708rad)
  shape: bbox 0.8 x 0.45 x 0.3 mm, 24 faces (baked)
FEATURE [Part::Feature] Part__Feature1954  label="R0603 222_По умолчанию007"
  Placement = pos=(28.9889,32.5562,24.8143) rot=(0,1,0;1.5708rad)
  shape: bbox 0.8 x 0.39 x 1.54 mm, 6 faces (baked)
FEATURE [Part::Feature] Part__Feature1955  label="R0603 222_По умолчанию008"
  Placement = pos=(28.9889,32.5562,24.8143) rot=(0,1,0;1.5708rad)
  shape: bbox 0.8 x 0.016 x 1 mm, 48 faces (baked)
FEATURE [App::Part] R0603_222________________________001  label="R0603 222_По умолчанию009"
  Group = -> [Part__Feature1952,Part__Feature1953,Part__Feature1954,Part__Feature1955]
  Origin = -> Origin351
FEATURE [Part::Feature] Part__Feature1956  label="R0603 103_По умолчанию"
  Placement = pos=(27.7897,32.5562,24.8143) rot=(0,1,0;1.5708rad)
  shape: bbox 0.8 x 0.45 x 0.3 mm, 24 faces (baked)
FEATURE [Part::Feature] Part__Feature1957  label="R0603 103_По умолчанию001"
  Placement = pos=(27.7897,32.5562,24.8143) rot=(0,1,0;1.5708rad)
  shape: bbox 0.8 x 0.45 x 0.3 mm, 24 faces (baked)
FEATURE [Part::Feature] Part__Feature1958  label="R0603 103_По умолчанию002"
  Placement = pos=(27.7897,32.5562,24.8143) rot=(0,1,0;1.5708rad)
  shape: bbox 0.8 x 0.39 x 1.54 mm, 6 faces (baked)
FEATURE [Part::Feature] Part__Feature1959  label="R0603 103_По умолчанию003"
  Placement = pos=(27.7897,32.5562,24.8143) rot=(0,1,0;1.5708rad)
  shape: bbox 0.8 x 0.016 x 1 mm, 44 faces (baked)
FEATURE [App::Part] R0603_103________________________  label="R0603 103_По умолчанию004"
  Group = -> [Part__Feature1956,Part__Feature1957,Part__Feature1958,Part__Feature1959]
  Origin = -> Origin352
FEATURE [Part::Feature] Part__Feature1960  label="C0615"
  Placement = pos=(28.9889,33.0112,27.8084) rot=(0,1,0;1.5708rad)
  shape: bbox 0.91 x 0.91 x 1.6 mm, 44 faces (baked)
FEATURE [Part::Feature] Part__Feature1961  label="C0616"
  Placement = pos=(27.7897,33.0112,27.8084) rot=(0,1,0;1.5708rad)
  shape: bbox 0.91 x 0.91 x 1.6 mm, 44 faces (baked)
FEATURE [Part::Feature] Part__Feature1962  label="C0617"
  Placement = pos=(26.5717,33.0112,34.6467) rot=(0,1,0;1.5708rad)
  shape: bbox 0.91 x 0.91 x 1.6 mm, 44 faces (baked)
FEATURE [Part::Feature] Part__Feature1963  label="SOT23-3"
  Placement = pos=(26.8491,33.1612,31.4787) rot=(0,1,0;1.5708rad)
  shape: bbox 0.6603 x 0.6 x 0.48 mm, 14 faces (baked)
FEATURE [Part::Feature] Part__Feature1964  label="SOT23-004"
  Placement = pos=(26.8491,33.1612,31.4787) rot=(0,1,0;1.5708rad)
  shape: bbox 0.6603 x 0.6 x 0.48 mm, 14 faces (baked)
FEATURE [Part::Feature] Part__Feature1965  label="SOT23-005"
  Placement = pos=(26.8491,33.1612,31.4787) rot=(0,1,0;1.5708rad)
  shape: bbox 1.398 x 1 x 2.998 mm, 42 faces (baked)
FEATURE [Part::Feature] Part__Feature1966  label="SOT23-006"
  Placement = pos=(26.8491,33.1612,31.4787) rot=(0,1,0;1.5708rad)
  shape: bbox 0.6603 x 0.6 x 0.48 mm, 14 faces (baked)
FEATURE [App::Part] SOT23_3  label="SOT23-007"
  Group = -> [Part__Feature1963,Part__Feature1964,Part__Feature1965,Part__Feature1966]
  Origin = -> Origin353
FEATURE [Part::Feature] Part__Feature1967  label="SOD323 S4"
  Placement = pos=(26.3996,32.5572,26.4457) rot=(-0.57735,0.57735,0.57735;2.0944rad)
  shape: bbox 1.25 x 1.101 x 2.5 mm, 87 faces (baked)
FEATURE [Part::Feature] Part__Feature1968  label="Pulsador_Smd"
  Placement = pos=(27.6199,32.5662,22.084) rot=(0,0.707107,0.707107;3.14159rad)
  shape: bbox 3.92 x 1.91 x 2.9 mm, 86 faces (baked)
FEATURE [App::Part] HC05_Modulo  label="Module HC-05"
  Group = -> [Part__Feature1908,HC05_06,Pines_90,Led_0603_Smd,Part__Feature1947,R0603_222________________________,R0603_222________________________001,R0603_103________________________,Part__Feature1960,Part__Feature1961,Part__Feature1962,SOT23_3,Part__Feature1967,Part__Feature1968]
  Origin = -> Origin354
  Placement = pos=(-20.2898,-34.483,-9) rot=(1,0,0;1.5708rad)
FEATURE [Part::Feature] Part__Feature1969  label="XT60_Hembra"
  shape: bbox 4.001 x 4.001 x 19.1 mm, 45 faces (baked)
FEATURE [Part::Feature] Part__Feature1970  label="XT60_Hembra001"
  shape: bbox 4.001 x 4.001 x 19.1 mm, 45 faces (baked)
FEATURE [Part::Feature] Part__Feature1971  label="XT60_Hembra002"
  shape: bbox 15.9 x 7.902 x 16.1 mm, 245 faces (baked)
FEATURE [App::Part] XT60_Hembra  label="Port XT60"
  Group = -> [Part__Feature1969,Part__Feature1970,Part__Feature1971]
  Origin = -> Origin355
  Placement = pos=(58.3289,29.8213,17.9659) rot=(0,0,1;0rad)
FEATURE [Sketcher::SketchObject] Sketch255
  FullyConstrained = true
  MapMode = 5
  Support = -> [XY_Plane356]
  sketch-geometry (4):
    g0: LineSegment StartX=-12.7 StartY=12.7 StartZ=0 EndX=12.7 EndY=12.7 EndZ=0
    g1: LineSegment StartX=12.7 StartY=12.7 StartZ=0 EndX=12.7 EndY=-12.7 EndZ=0
    g2: LineSegment StartX=12.7 StartY=-12.7 StartZ=0 EndX=-12.7 EndY=-12.7 EndZ=0
    g3: LineSegment StartX=-12.7 StartY=-12.7 StartZ=0 EndX=-12.7 EndY=12.7 EndZ=0
  constraints (10):
    c: Coincident(g0,g1)
    c: Coincident(g1,g2)
    c: Coincident(g2,g3)
    c: Coincident(g3,g0)
    c: Horizontal(g0)
    c: Vertical(g3)
    c: Symmetric(g1,g2,g-2)
    c: Symmetric(g1,g0,g-1)
    c: Equal(g0,g1)
    c: DistanceX(g0,g0) = 25.4
FEATURE [PartDesign::Pad] Pad098
  Direction = (0,0,1)
  Length = 9.5
  Length2 = 10
  Profile = -> Sketch255
  ReferenceAxis = -> Sketch255 [N_Axis]
  Type = 0
FEATURE [PartDesign::Body] Body094  label="Convertisseur D36V50FX"
  Group = -> [Sketch255,Pad098]
  Origin = -> Origin356
  Placement = pos=(17,58,18) rot=(0,0,1;0rad)
  Tip = -> Pad098
FEATURE [Part::Feature] Part__Feature1972  label="XT60PW FEMALE"
  Placement = pos=(61,40,22) rot=(0,0.707107,-0.707107;3.14159rad)
  shape: bbox 15.5 x 18.4 x 10.1 mm, 134 faces (baked)
FEATURE [App::Part] Part  label="Main PCB"
  Group = -> [Body024,Teensy4_1_v22,HC05_Modulo,XT60_Hembra,Body094,Part__Feature1972]
  Origin = -> Origin077
  Placement = pos=(0,0,-8) rot=(0,0,1;0rad)
FEATURE [Sketcher::SketchObject] Sketch256
  ExternalGeometry = -> [Pad095]
  FullyConstrained = true
  MapMode = 5
  Placement = pos=(0,0,0) rot=(1,0,0;3.14159rad)
  Support = -> [Pad095]
  sketch-geometry (4):
    g0: Circle CenterX=31.7128 CenterY=0 CenterZ=0 NormalX=0 NormalY=0 NormalZ=1 AngleXU=0 Radius=1.5
    g1: Circle CenterX=-31.7128 CenterY=0 CenterZ=0 NormalX=0 NormalY=0 NormalZ=1 AngleXU=0 Radius=1.5
    g2: LineSegment StartX=31.7128 StartY=0 StartZ=0 EndX=35.7128 EndY=4 EndZ=0
    g3: LineSegment StartX=31.7128 StartY=0 StartZ=0 EndX=35.7128 EndY=-4 EndZ=0
  constraints (9):
    c: PointOnObject(g0,g-1)
    c: Diameter(g0) = 3
    c: Diameter(g1) = 3
    c: Symmetric(g1,g0,g-2)
    c: Coincident(g2,g0)
    c: Coincident(g2,g-3)
    c: Coincident(g3,g0)
    c: Coincident(g3,g-3)
    c: Perpendicular(g3,g2)
FEATURE [PartDesign::Pocket] Pocket125
  BaseFeature = -> Pad095
  Direction = (0,0,1)
  Length = 5
  Length2 = 5
  Profile = -> Sketch256
  ReferenceAxis = -> Sketch256 [N_Axis]
  Type = 1
FEATURE [PartDesign::Body] Body007  label="Mirror base"
  Group = -> [Sketch023,Pad007,Sketch251,Pad095,Sketch256,Pocket125]
  Origin = -> Origin024
  Placement = pos=(0,0,56) rot=(0,0,1;0rad)
  Tip = -> Pocket125
FEATURE [PartDesign::SubShapeBinder] Binder052
  BindCopyOnChange = 0
  BindMode = 0
  ClaimChildren = false
  Context = -> Part015 [Body025.Binder052.]
  Fuse = false
  MakeFace = true
  OffsetFill = false
  OffsetIntersection = false
  OffsetJoinType = 0
  OffsetOpenResult = false
  PartialLoad = false
  Relative = true
  Support = -> [Part001[Body007.Pocket125.Sketch256.]]
  _Version = 2
FEATURE [PartDesign::Pocket] Pocket126
  BaseFeature = -> Pocket112
  Direction = (2e-16,0,-1)
  Length = 5
  Length2 = 5
  Profile = -> Binder052
  Type = 1
FEATURE [PartDesign::Body] Body025  label="Support camera "
  Group = -> [Sketch065,Pad044,Binder010,Pocket052,Sketch249,Pad093,Sketch250,Pocket112,Binder052,Pocket126]
  Origin = -> Origin226
  Placement = pos=(0,0,1) rot=(0,0,1;0rad)
  Tip = -> Pocket126
FEATURE [App::Part] Part015  label="Camera"
  Group = -> [rt10,Body025]
  Origin = -> Origin342
  Placement = pos=(36.22,-17.79,57) rot=(0,0,-1;4.71239rad)
FEATURE [PartDesign::SubShapeBinder] Binder053
  BindCopyOnChange = 0
  BindMode = 0
  ClaimChildren = false
  Context = -> Part012 [Body003.Binder053.]
  Fuse = false
  MakeFace = true
  OffsetFill = false
  OffsetIntersection = false
  OffsetJoinType = 0
  OffsetOpenResult = false
  PartialLoad = false
  Relative = true
  Support = -> [Part015[Body025.Pocket112.Sketch250.]]
  _Version = 2
FEATURE [PartDesign::Pocket] Pocket127
  BaseFeature = -> Pocket121
  Direction = (-2e-16,0,-1)
  Length = 60
  Length2 = 5
  Placement = pos=(0,0,0) rot=(1,0,0;1.5708rad)
  Profile = -> Binder053
  Type = 0
FEATURE [PartDesign::Body] Body003  label="Outer shielding 1"
  Group = -> [Sketch016,Revolution001,Binder047,Pocket121,Binder053,Pocket127]
  Origin = -> Origin016
  Placement = pos=(1e-15,3,0) rot=(0,0,1;1.5708rad)
  Tip = -> Pocket127
FEATURE [App::Part] Part012  label="Shielding"
  Group = -> [Body003,Body051,Body052]
  Origin = -> Origin247
FEATURE [PartDesign::SubShapeBinder] Binder054
  BindCopyOnChange = 0
  BindMode = 0
  ClaimChildren = false
  Context = -> Body [Binder054.]
  Fuse = false
  MakeFace = true
  OffsetFill = false
  OffsetIntersection = false
  OffsetJoinType = 0
  OffsetOpenResult = false
  PartialLoad = false
  Relative = true
  Support = -> [Part015[Body025.Pocket112.Sketch250.]]
  _Version = 2
FEATURE [PartDesign::Pocket] Pocket128
  BaseFeature = -> Pocket122
  Direction = (-2e-16,-2e-16,-1)
  Length = 5
  Length2 = 5
  Profile = -> Binder054
  Type = 1
FEATURE [PartDesign::Body] Body  label="Main plate"
  Group = -> [Sketch,Pad,Sketch001,Pocket,PolarPattern,Sketch015,Pocket004,Sketch061,Pocket019,Binder,Pocket031,Binder005,Pocket038,Binder006,Pocket039,Binder007,Pocket040,Binder008,Pocket050,Sketch126,Pocket055,PolarPattern021,PolarPattern022,Binder032,Pocket101,Binder034,Pocket103,Binder038,Pocket109,Binder050,Pocket122,Binder054,Pocket128]
  Origin = -> Origin008
  Placement = pos=(0,0,-1) rot=(0,0,1;0.785398rad)
  Tip = -> Pocket128
FEATURE [Sketcher::SketchObject] Sketch077
  FullyConstrained = true
  MapMode = 5
  Support = -> [XY_Plane232]
  sketch-geometry (1):
    g0: Circle CenterX=0 CenterY=0 CenterZ=0 NormalX=0 NormalY=0 NormalZ=1 AngleXU=0 Radius=12
  constraints (2):
    c: Diameter(g0) = 24
    c: Coincident(g0,g-1)
FEATURE [PartDesign::Pad] Pad054
  Direction = (0,0,1)
  Length = 56.5
  Length2 = 28.25
  Profile = -> Sketch077
  ReferenceAxis = -> Sketch077 [N_Axis]
  Type = 0
FEATURE [Sketcher::SketchObject] Sketch257
  FullyConstrained = true
  MapMode = 5
  Placement = pos=(0,0,0) rot=(1,0,0;3.14159rad)
  Support = -> [Pad052]
  sketch-geometry (1):
    g0: Circle CenterX=0 CenterY=0 CenterZ=0 NormalX=0 NormalY=0 NormalZ=1 AngleXU=0 Radius=2
  constraints (2):
    c: Coincident(g0,g-1)
    c: Diameter(g0) = 4
FEATURE [PartDesign::Pad] Pad099
  BaseFeature = -> Pad052
  Direction = (0,0,-1)
  Length = 17.5
  Length2 = 10
  Profile = -> Sketch257
  ReferenceAxis = -> Sketch257 [N_Axis]
  Type = 0
FEATURE [PartDesign::Body] Body029  label="Moteur 1"
  Group = -> [Sketch075,Pad052,Sketch257,Pad099]
  Origin = -> Origin230
  Placement = pos=(-41.8711,59.7981,-2) rot=(-0.217607,0.690162,-0.690162;2.71306rad)
  Tip = -> Pad099
FEATURE [Sketcher::SketchObject] Sketch258
  FullyConstrained = true
  MapMode = 5
  Placement = pos=(0,0,0) rot=(1,0,0;3.14159rad)
  Support = -> [Pad054]
  sketch-geometry (1):
    g0: Circle CenterX=0 CenterY=0 CenterZ=0 NormalX=0 NormalY=0 NormalZ=1 AngleXU=0 Radius=2
  constraints (2):
    c: Coincident(g0,g-1)
    c: Diameter(g0) = 4
FEATURE [PartDesign::Pad] Pad100
  BaseFeature = -> Pad054
  Direction = (0,0,-1)
  Length = 17.5
  Length2 = 10
  Profile = -> Sketch258
  ReferenceAxis = -> Sketch258 [N_Axis]
  Type = 0
FEATURE [PartDesign::Body] Body031  label="Moteur 2"
  Group = -> [Sketch077,Pad054,Sketch258,Pad100]
  Origin = -> Origin232
  Placement = pos=(41.8711,59.7981,-8) rot=(0.913318,-0.287968,-0.287968;1.66134rad)
  Tip = -> Pad100
FEATURE [Sketcher::SketchObject] Sketch259
  FullyConstrained = true
  MapMode = 5
  Placement = pos=(0,0,0) rot=(1,0,0;3.14159rad)
  Support = -> [Pad051]
  sketch-geometry (1):
    g0: Circle CenterX=0 CenterY=0 CenterZ=0 NormalX=0 NormalY=0 NormalZ=1 AngleXU=0 Radius=2
  constraints (2):
    c: Coincident(g0,g-1)
    c: Diameter(g0) = 4
FEATURE [PartDesign::Pad] Pad101
  BaseFeature = -> Pad051
  Direction = (0,0,-1)
  Length = 17.5
  Length2 = 10
  Profile = -> Sketch259
  ReferenceAxis = -> Sketch259 [N_Axis]
  Type = 0
FEATURE [PartDesign::Body] Body028  label="Moteur 4"
  Group = -> [Sketch074,Pad051,Sketch259,Pad101]
  Origin = -> Origin229
  Placement = pos=(-41.8711,-59.7981,-8) rot=(-0.913318,0.287968,-0.287968;1.66134rad)
  Tip = -> Pad101
FEATURE [Sketcher::SketchObject] Sketch260
  FullyConstrained = true
  MapMode = 5
  Placement = pos=(0,0,0) rot=(1,0,0;3.14159rad)
  Support = -> [Pad057]
  sketch-geometry (1):
    g0: Circle CenterX=0 CenterY=0 CenterZ=0 NormalX=0 NormalY=0 NormalZ=1 AngleXU=0 Radius=2
  constraints (2):
    c: Coincident(g0,g-1)
    c: Diameter(g0) = 4
FEATURE [PartDesign::Pad] Pad102
  BaseFeature = -> Pad057
  Direction = (0,0,-1)
  Length = 17.5
  Length2 = 10
  Profile = -> Sketch260
  ReferenceAxis = -> Sketch260 [N_Axis]
  Type = 0
FEATURE [PartDesign::Body] Body033  label="Moteur 3"
  Group = -> [Sketch081,Pad057,Sketch260,Pad102]
  Origin = -> Origin235
  Placement = pos=(41.8711,-59.7981,-8) rot=(-0.913318,-0.287968,0.287968;1.66134rad)
  Tip = -> Pad102
FEATURE [Sketcher::SketchObject] Sketch261
  FullyConstrained = true
  MapMode = 5
  Support = -> [XY_Plane357]
  sketch-geometry (1):
    g0: Circle CenterX=0 CenterY=0 CenterZ=0 NormalX=0 NormalY=0 NormalZ=1 AngleXU=0 Radius=17.5
  constraints (2):
    c: Coincident(g0,g-1)
    c: Diameter(g0) = 35
FEATURE [PartDesign::Pad] Pad103
  Direction = (0,0,1)
  Length = 12
  Length2 = 10
  Profile = -> Sketch261
  ReferenceAxis = -> Sketch261 [N_Axis]
  Type = 0
FEATURE [PartDesign::Body] Body095  label="Corps"
  Group = -> [Sketch261,Pad103]
  Origin = -> Origin357
  Placement = pos=(0,0,24) rot=(0,0,1;0rad)
  Tip = -> Pad103
FEATURE [App::Part] LD19  label="LIDAR LD19"
  Group = -> [Part__Feature1464,Part__Feature1465,Part__Feature1466,Body095]
  Origin = -> Origin258
  Placement = pos=(0,0,13) rot=(0,0,-1;4.71239rad)
FEATURE [Sketcher::SketchObject] Sketch262
  FullyConstrained = false
  MapMode = 5
  Placement = pos=(0,0,0) rot=(0.57735,0.57735,0.57735;2.0944rad)
  Support = -> [YZ_Plane009]
  sketch-geometry (2):
    g0: LineSegment StartX=0 StartY=75.6915 StartZ=0 EndX=-25.0741 EndY=123.858 EndZ=0
    g1: LineSegment StartX=0 StartY=75.6915 StartZ=0 EndX=25.0741 EndY=123.858 EndZ=0
  constraints (4):
    c: PointOnObject(g0,g-2)
    c: Coincident(g1,g0)
    c: Symmetric(g0,g1,g-2)
    c: Angle(g1,g0) = 0.959931
FEATURE [Part::Feature] Part__Feature1973  label="OmniBase_Predeterminado007"
  Placement = pos=(4.80373,-0.638646,40.5) rot=(0,0,1;0rad)
  shape: bbox 44 x 43.9 x 9 mm, 104 faces (baked)
FEATURE [Part::Feature] Part__Feature1974  label="Roller_Predeterminado126"
  Placement = pos=(4.80373,20.3614,41.6192) rot=(0,0,1;0rad)
  shape: bbox 2.6 x 8.659 x 8.659 mm, 10 faces (baked)
FEATURE [Part::Feature] Part__Feature1975  label="Roller_Predeterminado127"
  Placement = pos=(-2.3787,19.0949,41.6192) rot=(0,0,1;0.349066rad)
  shape: bbox 4.664 x 8.342 x 8.659 mm, 10 faces (baked)
FEATURE [Part::Feature] Part__Feature1976  label="Roller_Predeterminado128"
  Placement = pos=(-8.69481,15.4483,41.6192) rot=(0,0,1;0.698132rad)
  shape: bbox 6.71 x 7.451 x 8.659 mm, 10 faces (baked)
FEATURE [Part::Feature] Part__Feature1977  label="Roller_Predeterminado129"
  Placement = pos=(-13.3828,9.86135,41.6192) rot=(0,0,1;1.0472rad)
  shape: bbox 7.965 x 5.765 x 8.659 mm, 10 faces (baked)
FEATURE [Part::Feature] Part__Feature1978  label="Roller_Predeterminado130"
  Placement = pos=(-15.8772,3.00797,41.6192) rot=(0,0,1;1.39626rad)
  shape: bbox 8.632 x 3.688 x 8.659 mm, 10 faces (baked)
FEATURE [Part::Feature] Part__Feature1979  label="Roller_Predeterminado131"
  Placement = pos=(-15.8772,-4.28526,41.6192) rot=(0,0,1;1.74533rad)
  shape: bbox 8.632 x 3.688 x 8.659 mm, 10 faces (baked)
FEATURE [Part::Feature] Part__Feature1980  label="Roller_Predeterminado132"
  Placement = pos=(-13.3828,-11.1386,41.6192) rot=(0,0,1;2.0944rad)
  shape: bbox 7.965 x 5.765 x 8.659 mm, 10 faces (baked)
FEATURE [Part::Feature] Part__Feature1981  label="Roller_Predeterminado133"
  Placement = pos=(-8.69481,-16.7256,41.6192) rot=(0,0,1;2.44346rad)
  shape: bbox 6.71 x 7.451 x 8.659 mm, 10 faces (baked)
FEATURE [Part::Feature] Part__Feature1982  label="Roller_Predeterminado134"
  Placement = pos=(-2.3787,-20.3722,41.6192) rot=(0,0,1;2.79253rad)
  shape: bbox 4.664 x 8.342 x 8.659 mm, 10 faces (baked)
FEATURE [Part::Feature] Part__Feature1983  label="Roller_Predeterminado135"
  Placement = pos=(4.80373,-21.6386,41.6192) rot=(0,0,1;3.14159rad)
  shape: bbox 2.6 x 8.659 x 8.659 mm, 10 faces (baked)
FEATURE [Part::Feature] Part__Feature1984  label="Roller_Predeterminado136"
  Placement = pos=(11.9862,-20.3722,41.6192) rot=(0,0,1;3.49066rad)
  shape: bbox 4.664 x 8.342 x 8.659 mm, 10 faces (baked)
FEATURE [Part::Feature] Part__Feature1985  label="Roller_Predeterminado137"
  Placement = pos=(18.3023,-16.7256,41.6192) rot=(0,0,1;3.83972rad)
  shape: bbox 6.71 x 7.451 x 8.659 mm, 10 faces (baked)
FEATURE [Part::Feature] Part__Feature1986  label="Roller_Predeterminado138"
  Placement = pos=(22.9903,-11.1386,41.6192) rot=(0,0,-1;2.0944rad)
  shape: bbox 7.965 x 5.765 x 8.659 mm, 10 faces (baked)
FEATURE [Part::Feature] Part__Feature1987  label="Roller_Predeterminado139"
  Placement = pos=(25.4847,-4.28526,41.6192) rot=(0,0,-1;1.74533rad)
  shape: bbox 8.632 x 3.688 x 8.659 mm, 10 faces (baked)
FEATURE [Part::Feature] Part__Feature1988  label="Roller_Predeterminado140"
  Placement = pos=(25.4847,3.00797,41.6192) rot=(0,0,-1;1.39626rad)
  shape: bbox 8.632 x 3.688 x 8.659 mm, 10 faces (baked)
FEATURE [Part::Feature] Part__Feature1989  label="Roller_Predeterminado141"
  Placement = pos=(22.9903,9.86135,41.6192) rot=(0,0,-1;1.0472rad)
  shape: bbox 7.965 x 5.765 x 8.659 mm, 10 faces (baked)
FEATURE [Part::Feature] Part__Feature1990  label="Roller_Predeterminado142"
  Placement = pos=(18.3023,15.4483,41.6192) rot=(0,0,-1;0.698132rad)
  shape: bbox 6.71 x 7.451 x 8.659 mm, 10 faces (baked)
FEATURE [Part::Feature] Part__Feature1991  label="Roller_Predeterminado143"
  Placement = pos=(11.9862,19.0949,41.6192) rot=(0,0,-1;0.349066rad)
  shape: bbox 4.664 x 8.342 x 8.659 mm, 10 faces (baked)
FEATURE [Part::Feature] Part__Feature1992  label="Nut_Predeterminado007"
  Placement = pos=(4.80373,-0.638646,43.5) rot=(0,0,1;1.0472rad)
  shape: bbox 13.86 x 12.93 x 2 mm, 24 faces (baked)
FEATURE [App::Part] OmniWheel057  label="OmniWheel 2"
  Group = -> [Part__Feature1973,Part__Feature1974,Part__Feature1975,Part__Feature1976,Part__Feature1977,Part__Feature1978,Part__Feature1979,Part__Feature1980,Part__Feature1981,Part__Feature1982,Part__Feature1983,Part__Feature1984,Part__Feature1985,Part__Feature1986,Part__Feature1987,Part__Feature1988,Part__Feature1989,Part__Feature1990,Part__Feature1991,Part__Feature1992]
  Origin = -> Origin358
  Placement = pos=(20.4451,37.5671,-8.7) rot=(-0.913318,0.287968,-0.287968;1.66134rad)
FEATURE [App::Part] Part006  label="Motor assembly 2"
  Group = -> [Body031,Body039,OmniWheel057]
  Origin = -> Origin039
  Placement = pos=(1,-4,0) rot=(0,0,-1;6.24828rad)
FEATURE [Part::Feature] Part__Feature1993  label="OmniBase_Predeterminado008"
  Placement = pos=(4.80373,-0.638646,40.5) rot=(0,0,1;0rad)
  shape: bbox 44 x 43.9 x 9 mm, 104 faces (baked)
FEATURE [Part::Feature] Part__Feature1994  label="Roller_Predeterminado144"
  Placement = pos=(4.80373,20.3614,41.6192) rot=(0,0,1;0rad)
  shape: bbox 2.6 x 8.659 x 8.659 mm, 10 faces (baked)
FEATURE [Part::Feature] Part__Feature1995  label="Roller_Predeterminado145"
  Placement = pos=(-2.3787,19.0949,41.6192) rot=(0,0,1;0.349066rad)
  shape: bbox 4.664 x 8.342 x 8.659 mm, 10 faces (baked)
FEATURE [Part::Feature] Part__Feature1996  label="Roller_Predeterminado146"
  Placement = pos=(-8.69481,15.4483,41.6192) rot=(0,0,1;0.698132rad)
  shape: bbox 6.71 x 7.451 x 8.659 mm, 10 faces (baked)
FEATURE [Part::Feature] Part__Feature1997  label="Roller_Predeterminado147"
  Placement = pos=(-13.3828,9.86135,41.6192) rot=(0,0,1;1.0472rad)
  shape: bbox 7.965 x 5.765 x 8.659 mm, 10 faces (baked)
FEATURE [Part::Feature] Part__Feature1998  label="Roller_Predeterminado148"
  Placement = pos=(-15.8772,3.00797,41.6192) rot=(0,0,1;1.39626rad)
  shape: bbox 8.632 x 3.688 x 8.659 mm, 10 faces (baked)
FEATURE [Part::Feature] Part__Feature1999  label="Roller_Predeterminado149"
  Placement = pos=(-15.8772,-4.28526,41.6192) rot=(0,0,1;1.74533rad)
  shape: bbox 8.632 x 3.688 x 8.659 mm, 10 faces (baked)
FEATURE [Part::Feature] Part__Feature2000  label="Roller_Predeterminado150"
  Placement = pos=(-13.3828,-11.1386,41.6192) rot=(0,0,1;2.0944rad)
  shape: bbox 7.965 x 5.765 x 8.659 mm, 10 faces (baked)
FEATURE [Part::Feature] Part__Feature2001  label="Roller_Predeterminado151"
  Placement = pos=(-8.69481,-16.7256,41.6192) rot=(0,0,1;2.44346rad)
  shape: bbox 6.71 x 7.451 x 8.659 mm, 10 faces (baked)
FEATURE [Part::Feature] Part__Feature2002  label="Roller_Predeterminado152"
  Placement = pos=(-2.3787,-20.3722,41.6192) rot=(0,0,1;2.79253rad)
  shape: bbox 4.664 x 8.342 x 8.659 mm, 10 faces (baked)
FEATURE [Part::Feature] Part__Feature2003  label="Roller_Predeterminado153"
  Placement = pos=(4.80373,-21.6386,41.6192) rot=(0,0,1;3.14159rad)
  shape: bbox 2.6 x 8.659 x 8.659 mm, 10 faces (baked)
FEATURE [Part::Feature] Part__Feature2004  label="Roller_Predeterminado154"
  Placement = pos=(11.9862,-20.3722,41.6192) rot=(0,0,1;3.49066rad)
  shape: bbox 4.664 x 8.342 x 8.659 mm, 10 faces (baked)
FEATURE [Part::Feature] Part__Feature2005  label="Roller_Predeterminado155"
  Placement = pos=(18.3023,-16.7256,41.6192) rot=(0,0,1;3.83972rad)
  shape: bbox 6.71 x 7.451 x 8.659 mm, 10 faces (baked)
FEATURE [Part::Feature] Part__Feature2006  label="Roller_Predeterminado156"
  Placement = pos=(22.9903,-11.1386,41.6192) rot=(0,0,-1;2.0944rad)
  shape: bbox 7.965 x 5.765 x 8.659 mm, 10 faces (baked)
FEATURE [Part::Feature] Part__Feature2007  label="Roller_Predeterminado157"
  Placement = pos=(25.4847,-4.28526,41.6192) rot=(0,0,-1;1.74533rad)
  shape: bbox 8.632 x 3.688 x 8.659 mm, 10 faces (baked)
FEATURE [Part::Feature] Part__Feature2008  label="Roller_Predeterminado158"
  Placement = pos=(25.4847,3.00797,41.6192) rot=(0,0,-1;1.39626rad)
  shape: bbox 8.632 x 3.688 x 8.659 mm, 10 faces (baked)
FEATURE [Part::Feature] Part__Feature2009  label="Roller_Predeterminado159"
  Placement = pos=(22.9903,9.86135,41.6192) rot=(0,0,-1;1.0472rad)
  shape: bbox 7.965 x 5.765 x 8.659 mm, 10 faces (baked)
FEATURE [Part::Feature] Part__Feature2010  label="Roller_Predeterminado160"
  Placement = pos=(18.3023,15.4483,41.6192) rot=(0,0,-1;0.698132rad)
  shape: bbox 6.71 x 7.451 x 8.659 mm, 10 faces (baked)
FEATURE [Part::Feature] Part__Feature2011  label="Roller_Predeterminado161"
  Placement = pos=(11.9862,19.0949,41.6192) rot=(0,0,-1;0.349066rad)
  shape: bbox 4.664 x 8.342 x 8.659 mm, 10 faces (baked)
FEATURE [Part::Feature] Part__Feature2012  label="Nut_Predeterminado008"
  Placement = pos=(4.80373,-0.638646,43.5) rot=(0,0,1;1.0472rad)
  shape: bbox 13.86 x 12.93 x 2 mm, 24 faces (baked)
FEATURE [App::Part] OmniWheel058  label="OmniWheel 3"
  Group = -> [Part__Feature1993,Part__Feature1994,Part__Feature1995,Part__Feature1996,Part__Feature1997,Part__Feature1998,Part__Feature1999,Part__Feature2000,Part__Feature2001,Part__Feature2002,Part__Feature2003,Part__Feature2004,Part__Feature2005,Part__Feature2006,Part__Feature2007,Part__Feature2008,Part__Feature2009,Part__Feature2010,Part__Feature2011,Part__Feature2012]
  Origin = -> Origin359
  Placement = pos=(20.4451,-37.5671,-7.4) rot=(0.913318,0.287968,0.287968;1.66134rad)
FEATURE [App::Part] Part007  label="Motor assembly 3"
  Group = -> [Body033,Body040,OmniWheel058]
  Origin = -> Origin040
  Placement = pos=(1,4,0) rot=(0,0,1;6.24828rad)
FEATURE [Part::Feature] Part__Feature2013  label="OmniBase_Predeterminado009"
  Placement = pos=(4.80373,-0.638646,40.5) rot=(0,0,1;0rad)
  shape: bbox 44 x 43.9 x 9 mm, 104 faces (baked)
FEATURE [Part::Feature] Part__Feature2014  label="Roller_Predeterminado162"
  Placement = pos=(4.80373,20.3614,41.6192) rot=(0,0,1;0rad)
  shape: bbox 2.6 x 8.659 x 8.659 mm, 10 faces (baked)
FEATURE [Part::Feature] Part__Feature2015  label="Roller_Predeterminado163"
  Placement = pos=(-2.3787,19.0949,41.6192) rot=(0,0,1;0.349066rad)
  shape: bbox 4.664 x 8.342 x 8.659 mm, 10 faces (baked)
FEATURE [Part::Feature] Part__Feature2016  label="Roller_Predeterminado164"
  Placement = pos=(-8.69481,15.4483,41.6192) rot=(0,0,1;0.698132rad)
  shape: bbox 6.71 x 7.451 x 8.659 mm, 10 faces (baked)
FEATURE [Part::Feature] Part__Feature2017  label="Roller_Predeterminado165"
  Placement = pos=(-13.3828,9.86135,41.6192) rot=(0,0,1;1.0472rad)
  shape: bbox 7.965 x 5.765 x 8.659 mm, 10 faces (baked)
FEATURE [Part::Feature] Part__Feature2018  label="Roller_Predeterminado166"
  Placement = pos=(-15.8772,3.00797,41.6192) rot=(0,0,1;1.39626rad)
  shape: bbox 8.632 x 3.688 x 8.659 mm, 10 faces (baked)
FEATURE [Part::Feature] Part__Feature2019  label="Roller_Predeterminado167"
  Placement = pos=(-15.8772,-4.28526,41.6192) rot=(0,0,1;1.74533rad)
  shape: bbox 8.632 x 3.688 x 8.659 mm, 10 faces (baked)
FEATURE [Part::Feature] Part__Feature2020  label="Roller_Predeterminado168"
  Placement = pos=(-13.3828,-11.1386,41.6192) rot=(0,0,1;2.0944rad)
  shape: bbox 7.965 x 5.765 x 8.659 mm, 10 faces (baked)
FEATURE [Part::Feature] Part__Feature2021  label="Roller_Predeterminado169"
  Placement = pos=(-8.69481,-16.7256,41.6192) rot=(0,0,1;2.44346rad)
  shape: bbox 6.71 x 7.451 x 8.659 mm, 10 faces (baked)
FEATURE [Part::Feature] Part__Feature2022  label="Roller_Predeterminado170"
  Placement = pos=(-2.3787,-20.3722,41.6192) rot=(0,0,1;2.79253rad)
  shape: bbox 4.664 x 8.342 x 8.659 mm, 10 faces (baked)
FEATURE [Part::Feature] Part__Feature2023  label="Roller_Predeterminado171"
  Placement = pos=(4.80373,-21.6386,41.6192) rot=(0,0,1;3.14159rad)
  shape: bbox 2.6 x 8.659 x 8.659 mm, 10 faces (baked)
FEATURE [Part::Feature] Part__Feature2024  label="Roller_Predeterminado172"
  Placement = pos=(11.9862,-20.3722,41.6192) rot=(0,0,1;3.49066rad)
  shape: bbox 4.664 x 8.342 x 8.659 mm, 10 faces (baked)
FEATURE [Part::Feature] Part__Feature2025  label="Roller_Predeterminado173"
  Placement = pos=(18.3023,-16.7256,41.6192) rot=(0,0,1;3.83972rad)
  shape: bbox 6.71 x 7.451 x 8.659 mm, 10 faces (baked)
FEATURE [Part::Feature] Part__Feature2026  label="Roller_Predeterminado174"
  Placement = pos=(22.9903,-11.1386,41.6192) rot=(0,0,-1;2.0944rad)
  shape: bbox 7.965 x 5.765 x 8.659 mm, 10 faces (baked)
FEATURE [Part::Feature] Part__Feature2027  label="Roller_Predeterminado175"
  Placement = pos=(25.4847,-4.28526,41.6192) rot=(0,0,-1;1.74533rad)
  shape: bbox 8.632 x 3.688 x 8.659 mm, 10 faces (baked)
FEATURE [Part::Feature] Part__Feature2028  label="Roller_Predeterminado176"
  Placement = pos=(25.4847,3.00797,41.6192) rot=(0,0,-1;1.39626rad)
  shape: bbox 8.632 x 3.688 x 8.659 mm, 10 faces (baked)
FEATURE [Part::Feature] Part__Feature2029  label="Roller_Predeterminado177"
  Placement = pos=(22.9903,9.86135,41.6192) rot=(0,0,-1;1.0472rad)
  shape: bbox 7.965 x 5.765 x 8.659 mm, 10 faces (baked)
FEATURE [Part::Feature] Part__Feature2030  label="Roller_Predeterminado178"
  Placement = pos=(18.3023,15.4483,41.6192) rot=(0,0,-1;0.698132rad)
  shape: bbox 6.71 x 7.451 x 8.659 mm, 10 faces (baked)
FEATURE [Part::Feature] Part__Feature2031  label="Roller_Predeterminado179"
  Placement = pos=(11.9862,19.0949,41.6192) rot=(0,0,-1;0.349066rad)
  shape: bbox 4.664 x 8.342 x 8.659 mm, 10 faces (baked)
FEATURE [Part::Feature] Part__Feature2032  label="Nut_Predeterminado009"
  Placement = pos=(4.80373,-0.638646,43.5) rot=(0,0,1;1.0472rad)
  shape: bbox 13.86 x 12.93 x 2 mm, 24 faces (baked)
FEATURE [App::Part] OmniWheel059  label="OmniWheel 4"
  Group = -> [Part__Feature2013,Part__Feature2014,Part__Feature2015,Part__Feature2016,Part__Feature2017,Part__Feature2018,Part__Feature2019,Part__Feature2020,Part__Feature2021,Part__Feature2022,Part__Feature2023,Part__Feature2024,Part__Feature2025,Part__Feature2026,Part__Feature2027,Part__Feature2028,Part__Feature2029,Part__Feature2030,Part__Feature2031,Part__Feature2032]
  Origin = -> Origin360
  Placement = pos=(-28.3089,-32.0608,-7.4) rot=(-0.913318,0.287968,0.287968;4.62184rad)
FEATURE [App::Part] Part008  label="Motor assembly 4"
  Group = -> [Body028,Body041,OmniWheel059]
  Origin = -> Origin041
  Placement = pos=(-1,4,0) rot=(0,0,1;0.034907rad)
FEATURE [Sketcher::SketchObject] Sketch263
  ExternalGeometry = -> [PolarPattern012]
  FullyConstrained = true
  MapMode = 5
  Placement = pos=(-13,0,0) rot=(0.707107,0,-0.707107;3.14159rad)
  Support = -> [PolarPattern012]
  sketch-geometry (5):
    g0: LineSegment StartX=0 StartY=0 StartZ=0 EndX=-18 EndY=0 EndZ=0
    g1: LineSegment StartX=-18 StartY=0 StartZ=0 EndX=-18 EndY=20 EndZ=0
    g2: LineSegment StartX=0 StartY=0 StartZ=0 EndX=3.6e-15 EndY=3 EndZ=0
    g3: LineSegment StartX=3.6e-15 StartY=3 StartZ=0 EndX=-14 EndY=20 EndZ=0
    g4: LineSegment StartX=-14 StartY=20 StartZ=0 EndX=-18 EndY=20 EndZ=0
  constraints (12):
    c: Coincident(g0,g-1)
    c: Coincident(g0,g-3)
    c: Coincident(g1,g0)
    c: Vertical(g1)
    c: Coincident(g2,g0)
    c: Coincident(g2,g-4)
    c: Coincident(g3,g2)
    c: Coincident(g4,g3)
    c: Coincident(g4,g1)
    c: Horizontal(g4)
    c: DistanceY(g1,g1) = 20
    c: PointOnObject(g3,g-5)
FEATURE [PartDesign::Pad] Pad104
  BaseFeature = -> PolarPattern012
  Direction = (-1,0,-2e-16)
  Length = 3
  Length2 = 10
  Placement = pos=(0,0,0) rot=(1,0,0;1.5708rad)
  Profile = -> Sketch263
  ReferenceAxis = -> Sketch263 [N_Axis]
  Type = 0
FEATURE [Sketcher::SketchObject] Sketch264
  ExternalGeometry = -> [Pad104]
  FullyConstrained = true
  MapMode = 5
  Placement = pos=(13,0,0) rot=(0.707107,0,0.707107;3.14159rad)
  Support = -> [Pad104]
  sketch-geometry (5):
    g0: LineSegment StartX=0 StartY=0 StartZ=0 EndX=18 EndY=-2e-15 EndZ=0
    g1: LineSegment StartX=18 StartY=-2e-15 StartZ=0 EndX=18 EndY=20 EndZ=0
    g2: LineSegment StartX=0 StartY=0 StartZ=0 EndX=0 EndY=3 EndZ=0
    g3: LineSegment StartX=0 StartY=3 StartZ=0 EndX=14 EndY=20 EndZ=0
    g4: LineSegment StartX=14 StartY=20 StartZ=0 EndX=18 EndY=20 EndZ=0
  constraints (12):
    c: Coincident(g0,g-1)
    c: Coincident(g0,g-5)
    c: Coincident(g1,g0)
    c: Vertical(g1)
    c: Coincident(g2,g0)
    c: Coincident(g2,g-3)
    c: Coincident(g3,g2)
    c: PointOnObject(g3,g-4)
    c: Coincident(g4,g3)
    c: Coincident(g4,g1)
    c: Horizontal(g4)
    c: DistanceY(g1,g1) = 20
FEATURE [PartDesign::Pad] Pad105
  BaseFeature = -> Pad104
  Direction = (1,0,-2e-16)
  Length = 3
  Length2 = 10
  Placement = pos=(0,0,0) rot=(1,0,0;1.5708rad)
  Profile = -> Sketch264
  ReferenceAxis = -> Sketch264 [N_Axis]
  Type = 0
FEATURE [PartDesign::Body] Body038  label="Moteur support 1"
  Group = -> [Sketch084,Pad062,Sketch085,Pad063,Sketch086,Pocket029,Sketch087,Pocket030,PolarPattern012,Sketch263,Pad104,Sketch264,Pad105]
  Origin = -> Origin241
  Placement = pos=(-43.5918,62.2556,-2) rot=(0,0,1;0.610865rad)
  Tip = -> Pad105
FEATURE [App::Part] Part005  label="Motor assembly 1"
  Group = -> [OmniWheel054,Body029,Body038]
  Origin = -> Origin038
  Placement = pos=(-1,-4,-6) rot=(0,0,-1;0.034907rad)
FEATURE [App::Part] Part003  label="Powertrain"
  Group = -> [Part005,Part006,Part007,Part008]
  Origin = -> Origin034
  Placement = pos=(0,0,-11) rot=(0,0,1;0rad)
FEATURE [Sketcher::SketchObject] Sketch021
  FullyConstrained = true
  MapMode = 5
  Support = -> [XY_Plane023]
  sketch-geometry (2):
    g0: Circle CenterX=0 CenterY=0 CenterZ=0 NormalX=0 NormalY=0 NormalZ=1 AngleXU=0 Radius=23
    g1: Circle CenterX=0 CenterY=0 CenterZ=0 NormalX=0 NormalY=0 NormalZ=1 AngleXU=0 Radius=25
  constraints (4):
    c: Coincident(g0,g-1)
    c: Diameter(g0) = 46
    c: Coincident(g1,g0)
    c: Diameter(g1) = 50
FEATURE [PartDesign::Pad] Pad006
  Direction = (0,0,1)
  Length = 63.4
  Length2 = 10
  Profile = -> Sketch021
  ReferenceAxis = -> Sketch021 [N_Axis]
  Reversed = true
  Type = 0
FEATURE [PartDesign::Body] Body006  label="Mirror protection"
  Group = -> [Sketch021,Pad006]
  Origin = -> Origin023
  Placement = pos=(0,0,123.4) rot=(0,0,1;0rad)
  Tip = -> Pad006
FEATURE [Sketcher::SketchObject] Sketch265
  FullyConstrained = true
  MapMode = 5
  Placement = pos=(0,2.71e-14,122) rot=(0,0,1;3.14159rad)
  Support = -> [Revolution]
  sketch-geometry (1):
    g0: Circle CenterX=0 CenterY=0 CenterZ=0 NormalX=0 NormalY=0 NormalZ=1 AngleXU=0 Radius=60
  constraints (2):
    c: Coincident(g0,g-1)
    c: Diameter(g0) = 120
FEATURE [PartDesign::Pad] Pad106
  BaseFeature = -> Revolution
  Direction = (0,-2e-16,1)
  Length = 3
  Length2 = 10
  Placement = pos=(0,0,0) rot=(1,0,0;1.5708rad)
  Profile = -> Sketch265
  ReferenceAxis = -> Sketch265 [N_Axis]
  Type = 0
FEATURE [Sketcher::SketchObject] Sketch266
  FullyConstrained = true
  MapMode = 5
  Placement = pos=(0,-6e-15,125) rot=(0,0,1;3.14159rad)
  Support = -> [Pad106]
  sketch-geometry (5):
    g0: Circle CenterX=0 CenterY=0 CenterZ=0 NormalX=0 NormalY=0 NormalZ=1 AngleXU=0 Radius=3
    g1: Circle CenterX=-32 CenterY=0 CenterZ=0 NormalX=0 NormalY=0 NormalZ=1 AngleXU=0 Radius=3
    g2: Circle CenterX=32 CenterY=0 CenterZ=0 NormalX=0 NormalY=0 NormalZ=1 AngleXU=0 Radius=3
    g3: Circle CenterX=-44 CenterY=0 CenterZ=0 NormalX=0 NormalY=0 NormalZ=1 AngleXU=0 Radius=2
    g4: Circle CenterX=44 CenterY=0 CenterZ=0 NormalX=0 NormalY=0 NormalZ=1 AngleXU=0 Radius=2
  constraints (12):
    c: Coincident(g0,g-1)
    c: Diameter(g0) = 6
    c: PointOnObject(g1,g-1)
    c: Symmetric(g1,g2,g-2)
    c: Diameter(g1) = 6
    c: Diameter(g2) = 6
    c: DistanceX(g1,g0) = 32
    c: PointOnObject(g3,g-1)
    c: Diameter(g3) = 4
    c: Diameter(g4) = 4
    c: DistanceX(g3,g0) = 44
    c: Symmetric(g3,g4,g-2)
FEATURE [PartDesign::Pocket] Pocket129
  BaseFeature = -> Pad106
  Direction = (0,3e-16,-1)
  Length = 3
  Length2 = 5
  Placement = pos=(0,0,0) rot=(1,0,0;1.5708rad)
  Profile = -> Sketch266
  ReferenceAxis = -> Sketch266 [N_Axis]
  Type = 0
FEATURE [Sketcher::SketchObject] Sketch267
  FullyConstrained = true
  MapMode = 5
  Placement = pos=(0,-6e-15,125) rot=(0,0,1;3.14159rad)
  Support = -> [Pocket129]
  sketch-geometry (1):
    g0: Circle CenterX=0 CenterY=0 CenterZ=0 NormalX=0 NormalY=0 NormalZ=1 AngleXU=0 Radius=1.5
  constraints (2):
    c: Coincident(g0,g-1)
    c: Diameter(g0) = 3
FEATURE [PartDesign::Pocket] Pocket130
  BaseFeature = -> Pocket129
  Direction = (0,3e-16,-1)
  Length = 5
  Length2 = 5
  Placement = pos=(0,0,0) rot=(1,0,0;1.5708rad)
  Profile = -> Sketch267
  ReferenceAxis = -> Sketch267 [N_Axis]
  Type = 1
FEATURE [Sketcher::SketchObject] Sketch268
  FullyConstrained = true
  MapMode = 5
  Support = -> [XY_Plane361]
  sketch-geometry (3):
    g0: Circle CenterX=0 CenterY=0 CenterZ=0 NormalX=0 NormalY=0 NormalZ=1 AngleXU=0 Radius=4
    g1: LineSegment StartX=-1.36015 StartY=1.6 StartZ=0 EndX=1.36015 EndY=1.6 EndZ=0
    g2: ArcOfCircle CenterX=0 CenterY=0 CenterZ=0 NormalX=0 NormalY=0 NormalZ=1 AngleXU=0 Radius=2.1 StartAngle=2.27534 EndAngle=7.14943
  constraints (8):
    c: Coincident(g0,g-1)
    c: Diameter(g0) = 8
    c: Horizontal(g1)
    c: Coincident(g2,g0)
    c: Coincident(g2,g1)
    c: Coincident(g2,g1)
    c: Diameter(g2) = 4.2
    c: DistanceY(g0,g1) = 1.6
FEATURE [PartDesign::Pad] Pad107
  Direction = (0,0,1)
  Length = 10
  Length2 = 10
  Profile = -> Sketch268
  ReferenceAxis = -> Sketch268 [N_Axis]
  Type = 0
FEATURE [Sketcher::SketchObject] Sketch269
  ExternalGeometry = -> [Pad107]
  FullyConstrained = true
  MapMode = 5
  Placement = pos=(0,0,10) rot=(0,0,1;0rad)
  Support = -> [Pad107]
  sketch-geometry (2):
    g0: Circle CenterX=0 CenterY=0 CenterZ=0 NormalX=0 NormalY=0 NormalZ=1 AngleXU=0 Radius=4
    g1: Circle CenterX=0 CenterY=0 CenterZ=0 NormalX=0 NormalY=0 NormalZ=1 AngleXU=0 Radius=2.1
  constraints (4):
    c: Coincident(g0,g-3)
    c: Tangent(g0,g-3)
    c: Coincident(g1,g0)
    c: Tangent(g1,g-4)
FEATURE [PartDesign::Pad] Pad108
  BaseFeature = -> Pad107
  Direction = (0,0,1)
  Length = 2
  Length2 = 10
  Profile = -> Sketch269
  ReferenceAxis = -> Sketch269 [N_Axis]
  Type = 0
FEATURE [Sketcher::SketchObject] Sketch270
  FullyConstrained = true
  MapMode = 5
  Placement = pos=(0,0,0) rot=(1,0,0;1.5708rad)
  Support = -> [XZ_Plane361]
  sketch-geometry (1):
    g0: Circle CenterX=0 CenterY=3 CenterZ=0 NormalX=0 NormalY=0 NormalZ=1 AngleXU=0 Radius=1.5
  constraints (3):
    c: PointOnObject(g0,g-2)
    c: Diameter(g0) = 3
    c: DistanceY(g-1,g0) = 3
FEATURE [PartDesign::Pocket] Pocket131
  BaseFeature = -> Pad108
  Direction = (0,1,-2e-16)
  Length = 5
  Length2 = 5
  Profile = -> Sketch270
  ReferenceAxis = -> Sketch270 [N_Axis]
  Type = 1
FEATURE [PartDesign::Body] Body096  label="Adaptateur 1"
  Group = -> [Sketch268,Pad107,Sketch269,Pad108,Sketch270,Pocket131]
  Origin = -> Origin361
  Tip = -> Pocket131
FEATURE [Sketcher::SketchObject] Sketch271
  FullyConstrained = true
  MapMode = 5
  Support = -> [XY_Plane362]
  sketch-geometry (3):
    g0: Circle CenterX=0 CenterY=0 CenterZ=0 NormalX=0 NormalY=0 NormalZ=1 AngleXU=0 Radius=4
    g1: LineSegment StartX=-1.36015 StartY=1.6 StartZ=0 EndX=1.36015 EndY=1.6 EndZ=0
    g2: ArcOfCircle CenterX=0 CenterY=0 CenterZ=0 NormalX=0 NormalY=0 NormalZ=1 AngleXU=0 Radius=2.1 StartAngle=2.27534 EndAngle=7.14943
  constraints (8):
    c: Coincident(g0,g-1)
    c: Diameter(g0) = 8
    c: Horizontal(g1)
    c: Coincident(g2,g0)
    c: Coincident(g2,g1)
    c: Coincident(g2,g1)
    c: Diameter(g2) = 4.2
    c: DistanceY(g0,g1) = 1.6
FEATURE [PartDesign::Pad] Pad109
  Direction = (0,0,1)
  Length = 10
  Length2 = 10
  Profile = -> Sketch271
  ReferenceAxis = -> Sketch271 [N_Axis]
  Type = 0
FEATURE [Sketcher::SketchObject] Sketch272
  ExternalGeometry = -> [Pad109]
  FullyConstrained = true
  MapMode = 5
  Placement = pos=(0,0,10) rot=(0,0,1;0rad)
  Support = -> [Pad109]
  sketch-geometry (2):
    g0: Circle CenterX=0 CenterY=0 CenterZ=0 NormalX=0 NormalY=0 NormalZ=1 AngleXU=0 Radius=4
    g1: Circle CenterX=0 CenterY=0 CenterZ=0 NormalX=0 NormalY=0 NormalZ=1 AngleXU=0 Radius=2.1
  constraints (4):
    c: Coincident(g0,g-3)
    c: Tangent(g0,g-3)
    c: Coincident(g1,g0)
    c: Tangent(g1,g-4)
FEATURE [PartDesign::Pad] Pad110
  BaseFeature = -> Pad109
  Direction = (0,0,1)
  Length = 2
  Length2 = 10
  Profile = -> Sketch272
  ReferenceAxis = -> Sketch272 [N_Axis]
  Type = 0
FEATURE [Sketcher::SketchObject] Sketch273
  FullyConstrained = true
  MapMode = 5
  Placement = pos=(0,0,0) rot=(1,0,0;1.5708rad)
  Support = -> [XZ_Plane362]
  sketch-geometry (1):
    g0: Circle CenterX=0 CenterY=8.5 CenterZ=0 NormalX=0 NormalY=0 NormalZ=1 AngleXU=0 Radius=1.5
  constraints (3):
    c: PointOnObject(g0,g-2)
    c: Diameter(g0) = 3
    c: DistanceY(g-1,g0) = 8.5
FEATURE [PartDesign::Pocket] Pocket132
  BaseFeature = -> Pad110
  Direction = (0,1,2e-16)
  Length = 5
  Length2 = 5
  Profile = -> Sketch273
  ReferenceAxis = -> Sketch273 [N_Axis]
  Type = 1
FEATURE [PartDesign::Body] Body097  label="Adaptateur 2"
  Group = -> [Sketch271,Pad109,Sketch272,Pad110,Sketch273,Pocket132]
  Origin = -> Origin362
  Placement = pos=(0,11,0) rot=(0,0,1;0rad)
  Tip = -> Pocket132
FEATURE [Sketcher::SketchObject] Sketch274
  ExternalGeometry = -> [Pocket130]
  FullyConstrained = false
  MapMode = 5
  Placement = pos=(0,-5.9e-15,122) rot=(1,0,0;3.14159rad)
  Support = -> [Pocket130]
  sketch-geometry (14):
    g0: LineSegment StartX=-29.1045 StartY=-0.958487 StartZ=0 EndX=-29.7222 EndY=2.02832 EndZ=0
    g1: LineSegment StartX=-29.7222 StartY=2.02832 StartZ=0 EndX=-32.6177 EndY=2.9868 EndZ=0
    g2: LineSegment StartX=-32.6177 StartY=2.9868 StartZ=0 EndX=-34.8955 EndY=0.958487 EndZ=0
    g3: LineSegment StartX=-34.8955 StartY=0.958487 StartZ=0 EndX=-34.2778 EndY=-2.02832 EndZ=0
    g4: LineSegment StartX=-34.2778 StartY=-2.02832 StartZ=0 EndX=-31.3823 EndY=-2.9868 EndZ=0
    g5: LineSegment StartX=-31.3823 StartY=-2.9868 StartZ=0 EndX=-29.1045 EndY=-0.958487 EndZ=0
    g6: Circle CenterX=-32 CenterY=0 CenterZ=0 NormalX=0 NormalY=0 NormalZ=1 AngleXU=0 Radius=3.05
    g7: LineSegment StartX=34.4331 StartY=-1.8391 StartZ=0 EndX=34.8093 EndY=1.18762 EndZ=0
    g8: LineSegment StartX=34.8093 StartY=1.18762 StartZ=0 EndX=32.3761 EndY=3.02672 EndZ=0
    g9: LineSegment StartX=32.3761 StartY=3.02672 StartZ=0 EndX=29.5669 EndY=1.8391 EndZ=0
    g10: LineSegment StartX=29.5669 StartY=1.8391 StartZ=0 EndX=29.1907 EndY=-1.18762 EndZ=0
    g11: LineSegment StartX=29.1907 StartY=-1.18762 StartZ=0 EndX=31.6239 EndY=-3.02672 EndZ=0
    g12: LineSegment StartX=31.6239 StartY=-3.02672 StartZ=0 EndX=34.4331 EndY=-1.8391 EndZ=0
    g13: Circle CenterX=32 CenterY=0 CenterZ=0 NormalX=0 NormalY=0 NormalZ=1 AngleXU=0 Radius=3.05
  constraints (30):
    c: Coincident(g0,g1)
    c: Coincident(g1,g2)
    c: Coincident(g2,g3)
    c: Coincident(g3,g4)
    c: Coincident(g4,g5)
    c: Coincident(g5,g0)
    c: Equal(g0, g1-g5) x5
    c: PointOnObject(g0,g6)
    c: PointOnObject(g1,g6)
    c: PointOnObject(g2,g6)
    c: PointOnObject(g3,g6)
    c: PointOnObject(g4,g6)
    c: PointOnObject(g5,g6)
    c: Coincident(g6,g-3)
    c: Coincident(g7,g8)
    c: Coincident(g8,g9)
    c: Coincident(g9,g10)
    c: Coincident(g10,g11)
    c: Coincident(g11,g12)
    c: Coincident(g12,g7)
    c: Equal(g7, g8-g12) x5
    c: PointOnObject(g7,g13)
    c: PointOnObject(g8,g13)
    c: PointOnObject(g9,g13)
    c: PointOnObject(g10,g13)
    c: PointOnObject(g11,g13)
    c: PointOnObject(g12,g13)
    c: Coincident(g13,g-4)
    c: Diameter(g6) = 6.1
    c: Diameter(g13) = 6.1
FEATURE [PartDesign::Pad] Pad111
  BaseFeature = -> Pocket130
  Direction = (0,3e-16,-1)
  Length = 73.4
  Length2 = 10
  Placement = pos=(0,0,0) rot=(1,0,0;1.5708rad)
  Profile = -> Sketch274
  ReferenceAxis = -> Sketch274 [N_Axis]
  Type = 0
FEATURE [PartDesign::Body] Body001  label="Mirror"
  Group = -> [Sketch005,Revolution,Sketch262,Sketch265,Pad106,Sketch266,Pocket129,Sketch267,Pocket130,Sketch274,Pad111]
  Origin = -> Origin009
  Placement = pos=(0,0,-0.6) rot=(0,0,1;0rad)
  Tip = -> Pad111
FEATURE [App::Part] Part001  label="Mirror assembly"
  Group = -> [Body007,Body001,Body006]
  Origin = -> Origin025
  Placement = pos=(0,0,10) rot=(0,0,1;4.71239rad)
